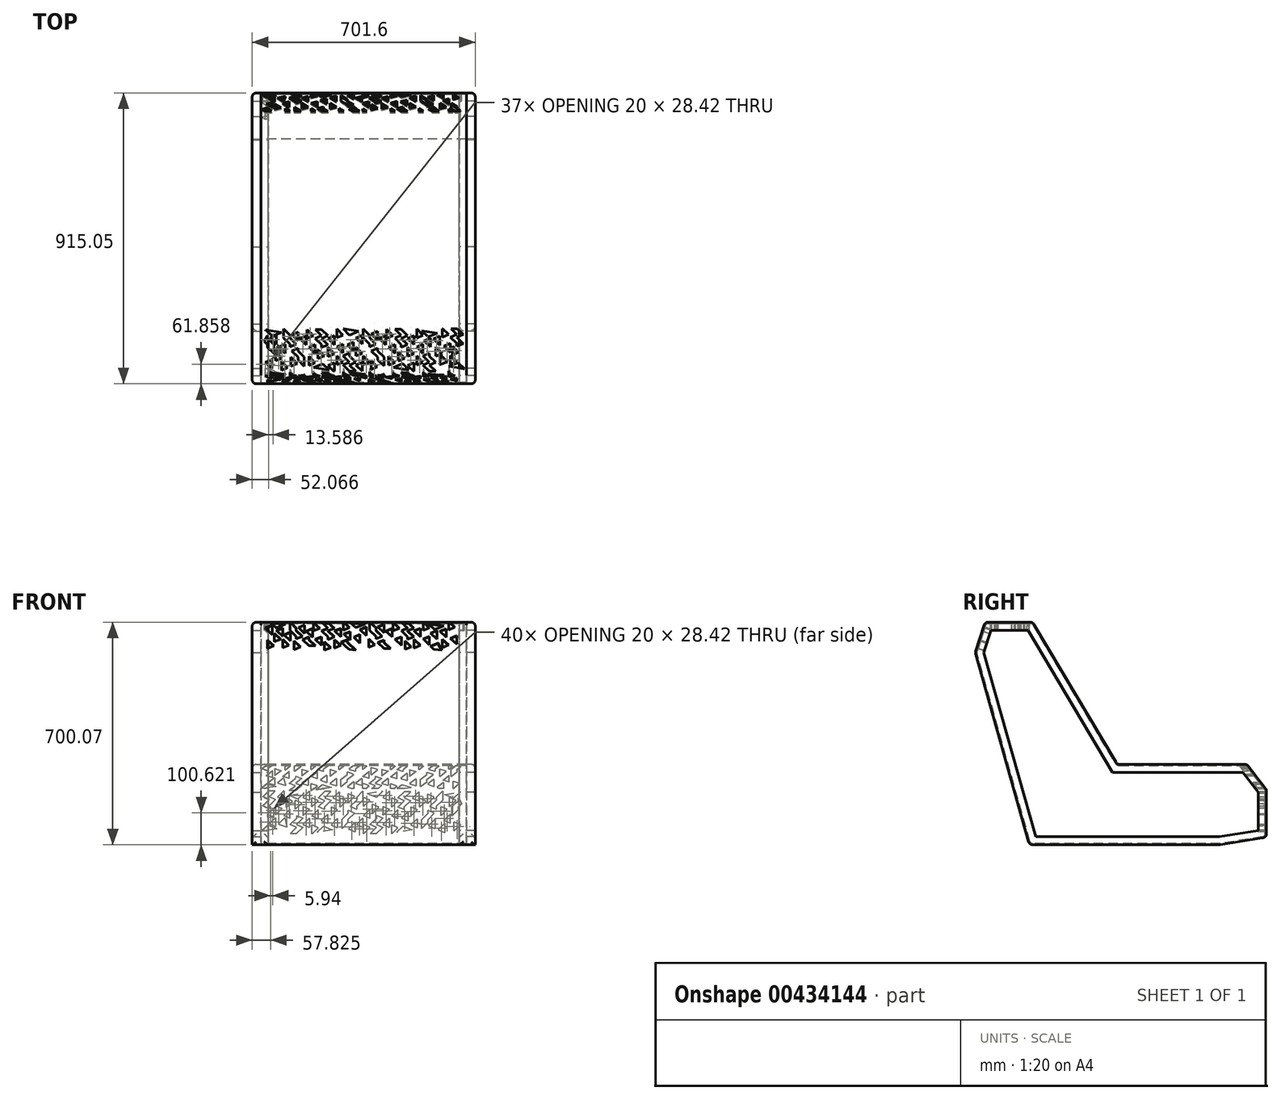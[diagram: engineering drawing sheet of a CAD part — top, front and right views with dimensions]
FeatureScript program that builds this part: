
annotation { "Feature Type Name" : "Feature", "Feature Type Description" : "" }
export const myFeature = defineFeature(function(context is Context, id is Id, definition is map)
    precondition{}
    {
        {
            var Q0;
            Q0=qCreatedBy(makeId("Right.planeOp"),FACE);
            var sketch = newSketch(context, id + "F0", { "sketchPlane" : qUnion([Q0])});
            skLineSegment(sketch, "E0", {"start": v(0, 0) * mm, "end": v(408.05, 0) * mm});
            skLineSegment(sketch, "E1", {"start": v(408.05, 0) * mm, "end": v(469.31, -79.04) * mm});
            skLineSegment(sketch, "E2", {"start": v(469.31, -79.04) * mm, "end": v(469.31, -229.04) * mm});
            skLineSegment(sketch, "E3", {"start": v(469.31, -229.04) * mm, "end": v(324.12, -252.64) * mm});
            skLineSegment(sketch, "E4", {"start": v(324.12, -252.64) * mm, "end": v(-275.88, -252.64) * mm});
            skLineSegment(sketch, "E5", {"start": v(-275.88, -252.64) * mm, "end": v(-446.19, 352.12) * mm});
            skLineSegment(sketch, "E6", {"start": v(-446.19, 352.12) * mm, "end": v(-415.7, 447.36) * mm});
            skLineSegment(sketch, "E7", {"start": v(-415.7, 447.36) * mm, "end": v(-265.7, 447.36) * mm});
            skLineSegment(sketch, "E8", {"start": v(-265.7, 447.36) * mm, "end": v(0, 0) * mm});
            skLineSegment(sketch, "E9.0", {"start": v(-419.67, 351.65) * mm, "end": v(-397.17, 421.96) * mm});
            skLineSegment(sketch, "E9.1", {"start": v(-256.64, -227.24) * mm, "end": v(-419.67, 351.65) * mm});
            skLineSegment(sketch, "E9.2", {"start": v(-397.17, 421.96) * mm, "end": v(-280.17, 421.96) * mm});
            skLineSegment(sketch, "E9.3", {"start": v(322.07, -227.24) * mm, "end": v(-256.64, -227.24) * mm});
            skLineSegment(sketch, "E9.4", {"start": v(443.91, -207.43) * mm, "end": v(322.07, -227.24) * mm});
            skLineSegment(sketch, "E9.5", {"start": v(-280.17, 421.96) * mm, "end": v(-14.46, -25.4) * mm});
            skLineSegment(sketch, "E9.6", {"start": v(-14.46, -25.4) * mm, "end": v(395.6, -25.4) * mm});
            skLineSegment(sketch, "E9.7", {"start": v(395.6, -25.4) * mm, "end": v(443.91, -87.73) * mm});
            skLineSegment(sketch, "E9.8", {"start": v(443.91, -87.73) * mm, "end": v(443.91, -207.43) * mm});
            skSolve(sketch);
        }
        {
            var Q0;
            Q0=makeQuery(id+"F0.imprint","IMPRINT",FACE,{"disambiguationData":[TD([[makeQuery(id+"F0.imprint","IMPRINT",EDGE,{"derivedFrom":sQuery(id+"F0.wireOp",EDGE,"E0")}),-1.0]])]});
            extrude(context, id + "F1", {"entities" : qUnion([Q0]), "depth" : 50.8 * mm});
        }
        {
            var Q0;
            Q0=makeQuery(id+"F1.opExtrude","SWEPT_FACE",FACE,{"disambiguationData":[OSD([sQuery(id+"F0.wireOp",EDGE,"E7")])]});
            var Q1;
            Q1=makeQuery(id+"F1.opExtrude","SWEPT_FACE",FACE,{"disambiguationData":[OSD([sQuery(id+"F0.wireOp",EDGE,"E8")])]});
            var Q2;
            Q2=makeQuery(id+"F1.opExtrude","SWEPT_FACE",FACE,{"disambiguationData":[OSD([sQuery(id+"F0.wireOp",EDGE,"E0")])]});
            var Q3;
            Q3=makeQuery(id+"F1.opExtrude","SWEPT_FACE",FACE,{"disambiguationData":[OSD([sQuery(id+"F0.wireOp",EDGE,"E1")])]});
            var Q4;
            Q4=makeQuery(id+"F1.opExtrude","SWEPT_FACE",FACE,{"disambiguationData":[OSD([sQuery(id+"F0.wireOp",EDGE,"E2")])]});
            var Q5;
            Q5=makeQuery(id+"F1.opExtrude","SWEPT_FACE",FACE,{"disambiguationData":[OSD([sQuery(id+"F0.wireOp",EDGE,"E5")])]});
            var Q6;
            Q6=makeQuery(id+"F1.opExtrude","SWEPT_FACE",FACE,{"disambiguationData":[OSD([sQuery(id+"F0.wireOp",EDGE,"E6")])]});
            fillet(context, id + "F2", {"entities" : qUnion([Q0, Q1, Q2, Q3, Q4, Q5, Q6]), "radius" : 12.7 * mm, "tangentPropagation" : true, "allowEdgeOverflow" : false});
        }
        {
            var Q0;
            Q0=qCreatedBy(makeId("Right.planeOp"),FACE);
            cPlane(context, id + "F3", {"entities" : qUnion([Q0]), "cplaneType" : CPlaneType.OFFSET, "offset" : 300 * mm, "oppositeDirection" : true, "width" : 152.4 * mm, "height" : 152.4 * mm});
        }
        {
            var Q0;
            Q0=makeQuery(id+"F1.opExtrude","SWEPT_BODY",BODY,{"disambiguationData":[OSD([sQuery(id+"F0.wireOp",EDGE,"E0"),sQuery(id+"F0.wireOp",EDGE,"E1"),sQuery(id+"F0.wireOp",EDGE,"E2"),sQuery(id+"F0.wireOp",EDGE,"E3"),sQuery(id+"F0.wireOp",EDGE,"E4"),sQuery(id+"F0.wireOp",EDGE,"E5"),sQuery(id+"F0.wireOp",EDGE,"E6"),sQuery(id+"F0.wireOp",EDGE,"E7"),sQuery(id+"F0.wireOp",EDGE,"E8"),sQuery(id+"F0.wireOp",EDGE,"E9.0"),sQuery(id+"F0.wireOp",EDGE,"E9.1"),sQuery(id+"F0.wireOp",EDGE,"E9.2"),sQuery(id+"F0.wireOp",EDGE,"E9.3"),sQuery(id+"F0.wireOp",EDGE,"E9.4"),sQuery(id+"F0.wireOp",EDGE,"E9.5"),sQuery(id+"F0.wireOp",EDGE,"E9.6"),sQuery(id+"F0.wireOp",EDGE,"E9.7"),sQuery(id+"F0.wireOp",EDGE,"E9.8")])]});
            var Q1;
            Q1=qCreatedBy(id+"F3.planeOp",FACE);
            mirror(context, id + "F4", {"entities" : qUnion([Q0]), "mirrorPlane" : qUnion([Q1])});
        }
        {
            var Q0;
            Q0=qCreatedBy(id+"F3.planeOp",FACE);
            var sketch = newSketch(context, id + "F5", { "sketchPlane" : qUnion([Q0])});
            skLineSegment(sketch, "E10.0", {"start": v(-406.34, 447.43) * mm, "end": v(-272.84, 447.43) * mm});
            skArc(sketch, "E11.0", {"start": v(-272.84, 447.43) * mm, "mid": v(-266.55, 445.77) * mm, "end": v(-261.92, 441.22) * mm});
            skLineSegment(sketch, "E12.0", {"start": v(-261.92, 441.22) * mm, "end": v(-3.59, 6.29) * mm});
            skArc(sketch, "E13.0", {"start": v(7.33, 0.07) * mm, "mid": v(1.05, 1.73) * mm, "end": v(-3.59, 6.29) * mm});
            skLineSegment(sketch, "E14.0", {"start": v(7.33, 0.07) * mm, "end": v(401.93, 0.07) * mm});
            skArc(sketch, "E15.0", {"start": v(411.97, -4.85) * mm, "mid": v(407.52, -1.23) * mm, "end": v(401.93, 0.07) * mm});
            skLineSegment(sketch, "E16.0", {"start": v(411.97, -4.85) * mm, "end": v(466.75, -75.53) * mm});
            skArc(sketch, "E17.0", {"start": v(469.42, -83.31) * mm, "mid": v(468.73, -79.2) * mm, "end": v(466.75, -75.53) * mm});
            skLineSegment(sketch, "E18.0", {"start": v(469.42, -83.31) * mm, "end": v(469.42, -218.16) * mm});
            skArc(sketch, "E19.0", {"start": v(458.75, -230.7) * mm, "mid": v(466.39, -226.4) * mm, "end": v(469.42, -218.16) * mm});
            skLineSegment(sketch, "E20.0", {"start": v(458.75, -230.7) * mm, "end": v(456.72, -231.03) * mm});
            skLineSegment(sketch, "E21.0", {"start": v(456.72, -231.03) * mm, "end": v(324.22, -252.57) * mm});
            skLineSegment(sketch, "E22.0", {"start": v(324.22, -252.57) * mm, "end": v(-262.58, -252.57) * mm});
            skLineSegment(sketch, "E23.0", {"start": v(-262.58, -252.57) * mm, "end": v(-266.16, -252.57) * mm});
            skArc(sketch, "E24.0", {"start": v(-278.38, -243.31) * mm, "mid": v(-273.83, -250) * mm, "end": v(-266.16, -252.57) * mm});
            skLineSegment(sketch, "E25.0", {"start": v(-278.38, -243.31) * mm, "end": v(-445.05, 348.51) * mm});
            skArc(sketch, "E26.0", {"start": v(-444.92, 355.83) * mm, "mid": v(-445.52, 352.18) * mm, "end": v(-445.05, 348.51) * mm});
            skLineSegment(sketch, "E27.0", {"start": v(-444.92, 355.83) * mm, "end": v(-418.43, 438.6) * mm});
            skArc(sketch, "E28.0", {"start": v(-406.34, 447.43) * mm, "mid": v(-413.82, 444.99) * mm, "end": v(-418.43, 438.6) * mm});
            skArc(sketch, "E29.0", {"start": v(-406.34, 443.62) * mm, "mid": v(-411.58, 441.91) * mm, "end": v(-414.8, 437.44) * mm});
            skLineSegment(sketch, "E29.1", {"start": v(-441.3, 354.67) * mm, "end": v(-414.8, 437.44) * mm});
            skArc(sketch, "E29.2", {"start": v(-441.3, 354.67) * mm, "mid": v(-441.71, 352.11) * mm, "end": v(-441.38, 349.55) * mm});
            skLineSegment(sketch, "E29.3", {"start": v(-274.72, -242.28) * mm, "end": v(-441.38, 349.55) * mm});
            skArc(sketch, "E29.4", {"start": v(-274.72, -242.28) * mm, "mid": v(-271.53, -246.96) * mm, "end": v(-266.16, -248.76) * mm});
            skLineSegment(sketch, "E29.5", {"start": v(-406.34, 443.62) * mm, "end": v(-272.84, 443.62) * mm});
            skLineSegment(sketch, "E29.6", {"start": v(-262.58, -248.76) * mm, "end": v(-266.16, -248.76) * mm});
            skLineSegment(sketch, "E29.7", {"start": v(323.92, -248.76) * mm, "end": v(-262.58, -248.76) * mm});
            skLineSegment(sketch, "E29.8", {"start": v(456.1, -227.27) * mm, "end": v(323.92, -248.76) * mm});
            skLineSegment(sketch, "E29.9", {"start": v(7.33, -3.74) * mm, "end": v(401.93, -3.74) * mm});
            skArc(sketch, "E29.10", {"start": v(7.33, -3.74) * mm, "mid": v(-0.84, -1.58) * mm, "end": v(-6.87, 4.34) * mm});
            skLineSegment(sketch, "E29.11", {"start": v(-265.2, 439.27) * mm, "end": v(-6.87, 4.34) * mm});
            skArc(sketch, "E29.12", {"start": v(-272.84, 443.62) * mm, "mid": v(-268.44, 442.46) * mm, "end": v(-265.2, 439.27) * mm});
            skArc(sketch, "E29.13", {"start": v(408.95, -7.18) * mm, "mid": v(405.84, -4.65) * mm, "end": v(401.93, -3.74) * mm});
            skLineSegment(sketch, "E29.14", {"start": v(408.95, -7.18) * mm, "end": v(463.74, -77.87) * mm});
            skArc(sketch, "E29.15", {"start": v(465.6, -83.31) * mm, "mid": v(465.13, -80.43) * mm, "end": v(463.74, -77.87) * mm});
            skLineSegment(sketch, "E29.16", {"start": v(465.6, -83.31) * mm, "end": v(465.6, -218.16) * mm});
            skArc(sketch, "E29.17", {"start": v(458.14, -226.94) * mm, "mid": v(463.49, -223.92) * mm, "end": v(465.6, -218.16) * mm});
            skLineSegment(sketch, "E29.18", {"start": v(458.14, -226.94) * mm, "end": v(456.1, -227.27) * mm});
            skSolve(sketch);
        }
        {
            var Q0;
            Q0 = qSketchRegion(id + "F5", true);
            extrude(context, id + "F6", {"entities" : qUnion([Q0]), "endBound" : BoundingType.SYMMETRIC, "depth" : 645.67 * mm});
        }
        {
            var Q0;
            Q0=makeQuery(id+"F6.opExtrude","SWEPT_FACE",FACE,{"disambiguationData":[OSD([sQuery(id+"F5.wireOp",EDGE,"E10.0")])]});
            var sketch = newSketch(context, id + "F7", { "sketchPlane" : qUnion([Q0])});
            skLineSegment(sketch, "E30", {"start": v(-607.6, -275.94) * mm, "end": v(-587.6, -295.74) * mm});
            skLineSegment(sketch, "E31", {"start": v(-588.73, -397.98) * mm, "end": v(-608.73, -378.18) * mm});
            skLineSegment(sketch, "E32", {"start": v(-608.73, -378.18) * mm, "end": v(-588.73, -369.56) * mm});
            skLineSegment(sketch, "E33", {"start": v(-576.96, -373.41) * mm, "end": v(-556.96, -364.79) * mm});
            skLineSegment(sketch, "E34", {"start": v(-556.96, -364.79) * mm, "end": v(-576.96, -344.99) * mm});
            skLineSegment(sketch, "E35", {"start": v(-547.5, -349.65) * mm, "end": v(-567.5, -329.84) * mm});
            skLineSegment(sketch, "E36", {"start": v(-567.5, -329.84) * mm, "end": v(-547.5, -321.22) * mm});
            skLineSegment(sketch, "E37", {"start": v(-588.73, -397.98) * mm, "end": v(-588.73, -369.56) * mm});
            skLineSegment(sketch, "E38", {"start": v(-576.96, -373.41) * mm, "end": v(-576.96, -344.99) * mm});
            skLineSegment(sketch, "E39", {"start": v(-547.5, -349.65) * mm, "end": v(-547.5, -321.22) * mm});
            skLineSegment(sketch, "E40", {"start": v(-575.15, -321.5) * mm, "end": v(-595.15, -301.7) * mm});
            skLineSegment(sketch, "E41", {"start": v(-595.15, -301.7) * mm, "end": v(-575.15, -293.08) * mm});
            skLineSegment(sketch, "E42", {"start": v(-575.15, -321.5) * mm, "end": v(-575.15, -293.08) * mm});
            skLineSegment(sketch, "E43", {"start": v(-552.39, -272.84) * mm, "end": v(-532.39, -292.64) * mm});
            skLineSegment(sketch, "E44", {"start": v(-552.39, -301.26) * mm, "end": v(-532.39, -321.06) * mm});
            skLineSegment(sketch, "E45", {"start": v(-558.92, -374.38) * mm, "end": v(-538.92, -394.19) * mm});
            skLineSegment(sketch, "E46", {"start": v(-538.92, -394.19) * mm, "end": v(-558.92, -402.8) * mm});
            skLineSegment(sketch, "E47", {"start": v(-552.39, -272.84) * mm, "end": v(-552.39, -301.26) * mm});
            skLineSegment(sketch, "E48", {"start": v(-532.39, -321.06) * mm, "end": v(-532.39, -329.68) * mm});
            skLineSegment(sketch, "E49", {"start": v(-558.92, -374.38) * mm, "end": v(-558.92, -402.8) * mm});
            skLineSegment(sketch, "E50", {"start": v(-532.39, -301.26) * mm, "end": v(-512.39, -321.06) * mm});
            skLineSegment(sketch, "E51", {"start": v(-512.39, -321.06) * mm, "end": v(-532.39, -329.68) * mm});
            skLineSegment(sketch, "E52", {"start": v(-528.78, -361.72) * mm, "end": v(-508.78, -381.52) * mm});
            skLineSegment(sketch, "E53", {"start": v(-508.78, -381.52) * mm, "end": v(-528.78, -390.14) * mm});
            skLineSegment(sketch, "E54", {"start": v(-532.39, -292.64) * mm, "end": v(-532.39, -301.26) * mm});
            skLineSegment(sketch, "E55", {"start": v(-528.78, -361.72) * mm, "end": v(-528.78, -390.14) * mm});
            skLineSegment(sketch, "E56", {"start": v(-587.6, -295.74) * mm, "end": v(-558.27, -283.53) * mm});
            skLineSegment(sketch, "E57", {"start": v(-558.27, -283.53) * mm, "end": v(-607.6, -275.94) * mm});
            skLineSegment(sketch, "E58", {"start": v(-392.44, -407.94) * mm, "end": v(-412.44, -388.14) * mm});
            skLineSegment(sketch, "E59", {"start": v(-412.44, -388.14) * mm, "end": v(-392.44, -379.52) * mm});
            skLineSegment(sketch, "E60", {"start": v(-412.44, -359.71) * mm, "end": v(-392.44, -351.1) * mm});
            skLineSegment(sketch, "E61", {"start": v(-392.44, -351.1) * mm, "end": v(-412.44, -331.29) * mm});
            skLineSegment(sketch, "E62", {"start": v(-392.44, -322.67) * mm, "end": v(-412.44, -302.86) * mm});
            skLineSegment(sketch, "E63", {"start": v(-412.44, -302.86) * mm, "end": v(-392.44, -294.24) * mm});
            skLineSegment(sketch, "E64", {"start": v(-392.44, -407.94) * mm, "end": v(-392.44, -379.52) * mm});
            skLineSegment(sketch, "E65", {"start": v(-412.44, -359.71) * mm, "end": v(-412.44, -331.29) * mm});
            skLineSegment(sketch, "E66", {"start": v(-392.44, -322.67) * mm, "end": v(-392.44, -294.24) * mm});
            skLineSegment(sketch, "E67", {"start": v(-408.39, -402.37) * mm, "end": v(-428.39, -382.57) * mm});
            skLineSegment(sketch, "E68", {"start": v(-432.44, -331.29) * mm, "end": v(-412.44, -322.67) * mm});
            skLineSegment(sketch, "E69", {"start": v(-412.44, -322.67) * mm, "end": v(-432.44, -302.86) * mm});
            skLineSegment(sketch, "E70", {"start": v(-432.44, -302.86) * mm, "end": v(-412.44, -294.24) * mm});
            skLineSegment(sketch, "E71", {"start": v(-412.44, -294.24) * mm, "end": v(-432.44, -274.44) * mm});
            skLineSegment(sketch, "E72", {"start": v(-478.2, -274.68) * mm, "end": v(-458.2, -294.48) * mm});
            skLineSegment(sketch, "E73", {"start": v(-458.2, -294.48) * mm, "end": v(-478.2, -303.1) * mm});
            skLineSegment(sketch, "E74", {"start": v(-452.57, -322.23) * mm, "end": v(-472.57, -330.85) * mm});
            skLineSegment(sketch, "E75", {"start": v(-472.57, -330.85) * mm, "end": v(-452.57, -350.65) * mm});
            skLineSegment(sketch, "E76", {"start": v(-472.57, -359.27) * mm, "end": v(-452.57, -379.08) * mm});
            skLineSegment(sketch, "E77", {"start": v(-452.57, -379.08) * mm, "end": v(-472.57, -387.7) * mm});
            skLineSegment(sketch, "E78", {"start": v(-478.2, -274.68) * mm, "end": v(-478.2, -303.1) * mm});
            skLineSegment(sketch, "E79", {"start": v(-452.57, -322.23) * mm, "end": v(-452.57, -350.65) * mm});
            skLineSegment(sketch, "E80", {"start": v(-472.57, -359.27) * mm, "end": v(-472.57, -387.7) * mm});
            skLineSegment(sketch, "E81", {"start": v(-452.16, -274.4) * mm, "end": v(-432.57, -293.8) * mm});
            skLineSegment(sketch, "E82", {"start": v(-432.57, -293.8) * mm, "end": v(-452.57, -302.43) * mm});
            skLineSegment(sketch, "E83", {"start": v(-452.57, -302.43) * mm, "end": v(-432.57, -322.23) * mm});
            skLineSegment(sketch, "E84", {"start": v(-444, -338.07) * mm, "end": v(-424, -357.88) * mm});
            skLineSegment(sketch, "E85", {"start": v(-424, -357.88) * mm, "end": v(-444, -366.5) * mm});
            skLineSegment(sketch, "E86", {"start": v(-444, -338.07) * mm, "end": v(-444, -366.5) * mm});
            skLineSegment(sketch, "E87", {"start": v(-486.83, -390.35) * mm, "end": v(-506.83, -370.54) * mm});
            skLineSegment(sketch, "E88", {"start": v(-486.83, -361.92) * mm, "end": v(-506.83, -342.12) * mm});
            skLineSegment(sketch, "E89", {"start": v(-480.97, -323.34) * mm, "end": v(-500.97, -303.54) * mm});
            skLineSegment(sketch, "E90", {"start": v(-500.97, -303.54) * mm, "end": v(-480.97, -294.92) * mm});
            skLineSegment(sketch, "E91", {"start": v(-486.83, -390.35) * mm, "end": v(-486.83, -361.92) * mm});
            skLineSegment(sketch, "E92", {"start": v(-506.83, -342.12) * mm, "end": v(-506.83, -333.5) * mm});
            skLineSegment(sketch, "E93", {"start": v(-480.97, -323.34) * mm, "end": v(-480.97, -294.92) * mm});
            skLineSegment(sketch, "E94", {"start": v(-506.83, -361.92) * mm, "end": v(-526.83, -342.12) * mm});
            skLineSegment(sketch, "E95", {"start": v(-526.83, -342.12) * mm, "end": v(-506.83, -333.5) * mm});
            skLineSegment(sketch, "E96", {"start": v(-505.93, -311.16) * mm, "end": v(-525.93, -291.36) * mm});
            skLineSegment(sketch, "E97", {"start": v(-525.93, -291.36) * mm, "end": v(-505.93, -282.74) * mm});
            skLineSegment(sketch, "E98", {"start": v(-506.83, -370.54) * mm, "end": v(-506.83, -361.92) * mm});
            skLineSegment(sketch, "E99", {"start": v(-505.93, -311.16) * mm, "end": v(-505.93, -282.74) * mm});
            skLineSegment(sketch, "E100", {"start": v(-452.16, -274.4) * mm, "end": v(-432.44, -274.44) * mm});
            skLineSegment(sketch, "E101", {"start": v(-432.44, -331.29) * mm, "end": v(-432.57, -322.23) * mm});
            skLineSegment(sketch, "E102", {"start": v(-428.39, -382.57) * mm, "end": v(-457.7, -394.78) * mm});
            skLineSegment(sketch, "E103", {"start": v(-457.7, -394.78) * mm, "end": v(-408.39, -402.37) * mm});
            skLineSegment(sketch, "E104", {"start": v(-384.82, -272.4) * mm, "end": v(-364.82, -292.21) * mm});
            skLineSegment(sketch, "E105", {"start": v(-364.82, -292.21) * mm, "end": v(-384.82, -300.83) * mm});
            skLineSegment(sketch, "E106", {"start": v(-364.82, -320.64) * mm, "end": v(-384.82, -329.26) * mm});
            skLineSegment(sketch, "E107", {"start": v(-384.82, -329.26) * mm, "end": v(-364.82, -349.06) * mm});
            skLineSegment(sketch, "E108", {"start": v(-384.82, -357.68) * mm, "end": v(-364.82, -377.49) * mm});
            skLineSegment(sketch, "E109", {"start": v(-364.82, -377.49) * mm, "end": v(-384.82, -386.1) * mm});
            skLineSegment(sketch, "E110", {"start": v(-384.82, -272.4) * mm, "end": v(-384.82, -300.83) * mm});
            skLineSegment(sketch, "E111", {"start": v(-364.82, -320.64) * mm, "end": v(-364.82, -349.06) * mm});
            skLineSegment(sketch, "E112", {"start": v(-384.82, -357.68) * mm, "end": v(-384.82, -386.1) * mm});
            skLineSegment(sketch, "E113", {"start": v(-364.82, -272.4) * mm, "end": v(-344.82, -292.21) * mm});
            skLineSegment(sketch, "E114", {"start": v(-344.82, -349.06) * mm, "end": v(-364.82, -357.68) * mm});
            skLineSegment(sketch, "E115", {"start": v(-364.82, -357.68) * mm, "end": v(-344.82, -377.49) * mm});
            skLineSegment(sketch, "E116", {"start": v(-344.82, -377.49) * mm, "end": v(-364.82, -386.1) * mm});
            skLineSegment(sketch, "E117", {"start": v(-364.82, -386.1) * mm, "end": v(-344.82, -405.91) * mm});
            skLineSegment(sketch, "E118", {"start": v(-364.82, -272.4) * mm, "end": v(-364.82, -272.42) * mm});
            skLineSegment(sketch, "E119", {"start": v(-304.68, -406.35) * mm, "end": v(-324.68, -386.55) * mm});
            skLineSegment(sketch, "E120", {"start": v(-324.68, -386.55) * mm, "end": v(-304.68, -377.92) * mm});
            skLineSegment(sketch, "E121", {"start": v(-324.68, -358.12) * mm, "end": v(-304.68, -349.5) * mm});
            skLineSegment(sketch, "E122", {"start": v(-304.68, -349.5) * mm, "end": v(-324.68, -329.7) * mm});
            skLineSegment(sketch, "E123", {"start": v(-304.68, -321.07) * mm, "end": v(-324.68, -301.27) * mm});
            skLineSegment(sketch, "E124", {"start": v(-324.68, -301.27) * mm, "end": v(-304.68, -292.65) * mm});
            skLineSegment(sketch, "E125", {"start": v(-304.68, -406.35) * mm, "end": v(-304.68, -377.92) * mm});
            skLineSegment(sketch, "E126", {"start": v(-324.68, -358.12) * mm, "end": v(-324.68, -329.7) * mm});
            skLineSegment(sketch, "E127", {"start": v(-304.68, -321.07) * mm, "end": v(-304.68, -292.65) * mm});
            skLineSegment(sketch, "E128", {"start": v(-325.1, -405.94) * mm, "end": v(-344.68, -386.55) * mm});
            skLineSegment(sketch, "E129", {"start": v(-344.68, -386.55) * mm, "end": v(-324.68, -377.92) * mm});
            skLineSegment(sketch, "E130", {"start": v(-324.68, -377.92) * mm, "end": v(-344.68, -358.12) * mm});
            skLineSegment(sketch, "E131", {"start": v(-331.9, -343.18) * mm, "end": v(-351.9, -323.37) * mm});
            skLineSegment(sketch, "E132", {"start": v(-351.9, -323.37) * mm, "end": v(-331.9, -314.75) * mm});
            skLineSegment(sketch, "E133", {"start": v(-331.9, -343.18) * mm, "end": v(-331.9, -314.75) * mm});
            skLineSegment(sketch, "E134", {"start": v(-301.93, -272.4) * mm, "end": v(-281.93, -292.21) * mm});
            skLineSegment(sketch, "E135", {"start": v(-301.93, -300.83) * mm, "end": v(-281.93, -320.64) * mm});
            skLineSegment(sketch, "E136", {"start": v(-301.93, -357.68) * mm, "end": v(-281.93, -377.49) * mm});
            skLineSegment(sketch, "E137", {"start": v(-281.93, -377.49) * mm, "end": v(-301.93, -386.1) * mm});
            skLineSegment(sketch, "E138", {"start": v(-301.93, -272.4) * mm, "end": v(-301.93, -300.83) * mm});
            skLineSegment(sketch, "E139", {"start": v(-281.93, -320.64) * mm, "end": v(-281.93, -329.26) * mm});
            skLineSegment(sketch, "E140", {"start": v(-301.93, -357.68) * mm, "end": v(-301.93, -386.1) * mm});
            skLineSegment(sketch, "E141", {"start": v(-281.93, -300.83) * mm, "end": v(-261.93, -320.64) * mm});
            skLineSegment(sketch, "E142", {"start": v(-261.93, -320.64) * mm, "end": v(-281.93, -329.26) * mm});
            skLineSegment(sketch, "E143", {"start": v(-276.96, -371.67) * mm, "end": v(-256.96, -391.47) * mm});
            skLineSegment(sketch, "E144", {"start": v(-256.96, -391.47) * mm, "end": v(-276.96, -400.1) * mm});
            skLineSegment(sketch, "E145", {"start": v(-281.93, -292.21) * mm, "end": v(-281.93, -300.83) * mm});
            skLineSegment(sketch, "E146", {"start": v(-276.96, -371.67) * mm, "end": v(-276.96, -400.1) * mm});
            skLineSegment(sketch, "E147", {"start": v(-325.1, -405.94) * mm, "end": v(-344.82, -405.91) * mm});
            skLineSegment(sketch, "E148", {"start": v(-344.82, -349.06) * mm, "end": v(-344.68, -358.12) * mm});
            skLineSegment(sketch, "E149", {"start": v(-344.82, -292.21) * mm, "end": v(-315.5, -280) * mm});
            skLineSegment(sketch, "E150", {"start": v(-315.5, -280) * mm, "end": v(-364.82, -272.4) * mm});
            skLineSegment(sketch, "E151", {"start": v(-141.97, -407.51) * mm, "end": v(-161.97, -387.71) * mm});
            skLineSegment(sketch, "E152", {"start": v(-161.97, -387.71) * mm, "end": v(-141.97, -379.09) * mm});
            skLineSegment(sketch, "E153", {"start": v(-161.97, -359.29) * mm, "end": v(-141.97, -350.66) * mm});
            skLineSegment(sketch, "E154", {"start": v(-141.97, -350.66) * mm, "end": v(-161.97, -330.86) * mm});
            skLineSegment(sketch, "E155", {"start": v(-141.97, -322.24) * mm, "end": v(-161.97, -302.44) * mm});
            skLineSegment(sketch, "E156", {"start": v(-161.97, -302.44) * mm, "end": v(-141.97, -293.82) * mm});
            skLineSegment(sketch, "E157", {"start": v(-141.97, -407.51) * mm, "end": v(-141.97, -379.09) * mm});
            skLineSegment(sketch, "E158", {"start": v(-161.97, -359.29) * mm, "end": v(-161.97, -330.86) * mm});
            skLineSegment(sketch, "E159", {"start": v(-141.97, -322.24) * mm, "end": v(-141.97, -293.82) * mm});
            skLineSegment(sketch, "E160", {"start": v(-157.92, -401.94) * mm, "end": v(-177.92, -382.14) * mm});
            skLineSegment(sketch, "E161", {"start": v(-181.97, -330.86) * mm, "end": v(-161.97, -322.24) * mm});
            skLineSegment(sketch, "E162", {"start": v(-161.97, -322.24) * mm, "end": v(-181.97, -302.44) * mm});
            skLineSegment(sketch, "E163", {"start": v(-181.97, -302.44) * mm, "end": v(-161.97, -293.82) * mm});
            skLineSegment(sketch, "E164", {"start": v(-161.97, -293.82) * mm, "end": v(-181.97, -274.01) * mm});
            skLineSegment(sketch, "E165", {"start": v(-227.74, -274.25) * mm, "end": v(-207.74, -294.05) * mm});
            skLineSegment(sketch, "E166", {"start": v(-207.74, -294.05) * mm, "end": v(-227.74, -302.68) * mm});
            skLineSegment(sketch, "E167", {"start": v(-202.1, -321.8) * mm, "end": v(-222.1, -330.42) * mm});
            skLineSegment(sketch, "E168", {"start": v(-222.1, -330.42) * mm, "end": v(-202.1, -350.23) * mm});
            skLineSegment(sketch, "E169", {"start": v(-222.1, -358.85) * mm, "end": v(-202.1, -378.65) * mm});
            skLineSegment(sketch, "E170", {"start": v(-202.1, -378.65) * mm, "end": v(-222.1, -387.27) * mm});
            skLineSegment(sketch, "E171", {"start": v(-227.74, -274.25) * mm, "end": v(-227.74, -302.68) * mm});
            skLineSegment(sketch, "E172", {"start": v(-202.1, -321.8) * mm, "end": v(-202.1, -350.23) * mm});
            skLineSegment(sketch, "E173", {"start": v(-222.1, -358.85) * mm, "end": v(-222.1, -387.27) * mm});
            skLineSegment(sketch, "E174", {"start": v(-201.7, -273.98) * mm, "end": v(-182.1, -293.38) * mm});
            skLineSegment(sketch, "E175", {"start": v(-182.1, -293.38) * mm, "end": v(-202.1, -302) * mm});
            skLineSegment(sketch, "E176", {"start": v(-202.1, -302) * mm, "end": v(-182.1, -321.8) * mm});
            skLineSegment(sketch, "E177", {"start": v(-191.28, -345.32) * mm, "end": v(-171.28, -365.12) * mm});
            skLineSegment(sketch, "E178", {"start": v(-171.28, -365.12) * mm, "end": v(-191.28, -373.74) * mm});
            skLineSegment(sketch, "E179", {"start": v(-191.28, -345.32) * mm, "end": v(-191.28, -373.74) * mm});
            skLineSegment(sketch, "E180", {"start": v(-236.37, -389.92) * mm, "end": v(-256.37, -370.12) * mm});
            skLineSegment(sketch, "E181", {"start": v(-236.37, -361.5) * mm, "end": v(-256.37, -341.7) * mm});
            skLineSegment(sketch, "E182", {"start": v(-230.5, -322.92) * mm, "end": v(-250.5, -303.11) * mm});
            skLineSegment(sketch, "E183", {"start": v(-250.5, -303.11) * mm, "end": v(-230.5, -294.5) * mm});
            skLineSegment(sketch, "E184", {"start": v(-236.37, -389.92) * mm, "end": v(-236.37, -361.5) * mm});
            skLineSegment(sketch, "E185", {"start": v(-256.37, -341.7) * mm, "end": v(-256.37, -333.07) * mm});
            skLineSegment(sketch, "E186", {"start": v(-230.5, -322.92) * mm, "end": v(-230.5, -294.5) * mm});
            skLineSegment(sketch, "E187", {"start": v(-256.37, -361.5) * mm, "end": v(-276.37, -341.7) * mm});
            skLineSegment(sketch, "E188", {"start": v(-276.37, -341.7) * mm, "end": v(-256.37, -333.07) * mm});
            skLineSegment(sketch, "E189", {"start": v(-256.37, -308.93) * mm, "end": v(-276.37, -289.13) * mm});
            skLineSegment(sketch, "E190", {"start": v(-276.37, -289.13) * mm, "end": v(-256.37, -280.5) * mm});
            skLineSegment(sketch, "E191", {"start": v(-256.37, -370.12) * mm, "end": v(-256.37, -361.5) * mm});
            skLineSegment(sketch, "E192", {"start": v(-256.37, -308.93) * mm, "end": v(-256.37, -280.5) * mm});
            skLineSegment(sketch, "E193", {"start": v(-201.7, -273.98) * mm, "end": v(-181.97, -274.01) * mm});
            skLineSegment(sketch, "E194", {"start": v(-181.97, -330.86) * mm, "end": v(-182.1, -321.8) * mm});
            skLineSegment(sketch, "E195", {"start": v(-177.92, -382.14) * mm, "end": v(-207.24, -394.35) * mm});
            skLineSegment(sketch, "E196", {"start": v(-207.24, -394.35) * mm, "end": v(-157.92, -401.94) * mm});
            skLineSegment(sketch, "E197", {"start": v(-133.47, -272.64) * mm, "end": v(-113.47, -292.45) * mm});
            skLineSegment(sketch, "E198", {"start": v(-113.47, -292.45) * mm, "end": v(-133.47, -301.07) * mm});
            skLineSegment(sketch, "E199", {"start": v(-113.47, -320.87) * mm, "end": v(-133.47, -329.5) * mm});
            skLineSegment(sketch, "E200", {"start": v(-133.47, -329.5) * mm, "end": v(-113.47, -349.3) * mm});
            skLineSegment(sketch, "E201", {"start": v(-133.47, -357.92) * mm, "end": v(-113.47, -377.72) * mm});
            skLineSegment(sketch, "E202", {"start": v(-113.47, -377.72) * mm, "end": v(-133.47, -386.34) * mm});
            skLineSegment(sketch, "E203", {"start": v(-133.47, -272.64) * mm, "end": v(-133.47, -301.07) * mm});
            skLineSegment(sketch, "E204", {"start": v(-113.47, -320.87) * mm, "end": v(-113.47, -349.3) * mm});
            skLineSegment(sketch, "E205", {"start": v(-133.47, -357.92) * mm, "end": v(-133.47, -386.34) * mm});
            skLineSegment(sketch, "E206", {"start": v(-117.52, -278.21) * mm, "end": v(-97.52, -298.01) * mm});
            skLineSegment(sketch, "E207", {"start": v(-93.47, -349.3) * mm, "end": v(-113.47, -357.92) * mm});
            skLineSegment(sketch, "E208", {"start": v(-113.47, -357.92) * mm, "end": v(-93.47, -377.72) * mm});
            skLineSegment(sketch, "E209", {"start": v(-93.47, -377.72) * mm, "end": v(-113.47, -386.34) * mm});
            skLineSegment(sketch, "E210", {"start": v(-113.47, -386.34) * mm, "end": v(-93.47, -406.14) * mm});
            skLineSegment(sketch, "E211", {"start": v(-73.34, -358.35) * mm, "end": v(-53.34, -349.73) * mm});
            skLineSegment(sketch, "E212", {"start": v(-53.34, -349.73) * mm, "end": v(-73.34, -329.93) * mm});
            skLineSegment(sketch, "E213", {"start": v(-61, -324.01) * mm, "end": v(-81, -304.21) * mm});
            skLineSegment(sketch, "E214", {"start": v(-81, -304.21) * mm, "end": v(-61, -295.59) * mm});
            skLineSegment(sketch, "E215", {"start": v(-73.34, -358.35) * mm, "end": v(-73.34, -329.93) * mm});
            skLineSegment(sketch, "E216", {"start": v(-61, -324.01) * mm, "end": v(-61, -295.59) * mm});
            skLineSegment(sketch, "E217", {"start": v(-73.75, -406.17) * mm, "end": v(-93.34, -386.78) * mm});
            skLineSegment(sketch, "E218", {"start": v(-93.34, -386.78) * mm, "end": v(-73.34, -378.16) * mm});
            skLineSegment(sketch, "E219", {"start": v(-73.34, -378.16) * mm, "end": v(-93.34, -358.35) * mm});
            skLineSegment(sketch, "E220", {"start": v(-90.03, -329.88) * mm, "end": v(-110.03, -310.08) * mm});
            skLineSegment(sketch, "E221", {"start": v(-110.03, -310.08) * mm, "end": v(-90.03, -301.45) * mm});
            skLineSegment(sketch, "E222", {"start": v(-90.03, -329.88) * mm, "end": v(-90.03, -301.45) * mm});
            skLineSegment(sketch, "E223", {"start": v(-73.75, -406.17) * mm, "end": v(-93.47, -406.14) * mm});
            skLineSegment(sketch, "E224", {"start": v(-93.47, -349.3) * mm, "end": v(-93.34, -358.35) * mm});
            skLineSegment(sketch, "E225", {"start": v(-97.52, -298.01) * mm, "end": v(-68.2, -285.8) * mm});
            skLineSegment(sketch, "E226", {"start": v(-68.2, -285.8) * mm, "end": v(-117.52, -278.21) * mm});
            skLineSegment(sketch, "E227", {"start": v(-21.76, -354.94) * mm, "end": v(-1.76, -346.32) * mm});
            skLineSegment(sketch, "E228", {"start": v(-1.76, -346.32) * mm, "end": v(-21.76, -326.52) * mm});
            skLineSegment(sketch, "E229", {"start": v(-21.76, -354.94) * mm, "end": v(-21.76, -326.52) * mm});
            skLineSegment(sketch, "E230", {"start": v(16.48, -398.74) * mm, "end": v(-3.52, -378.94) * mm});
            skLineSegment(sketch, "E231", {"start": v(-7.57, -327.66) * mm, "end": v(12.43, -319.04) * mm});
            skLineSegment(sketch, "E232", {"start": v(12.43, -319.04) * mm, "end": v(-7.57, -299.24) * mm});
            skLineSegment(sketch, "E233", {"start": v(-7.57, -299.24) * mm, "end": v(12.43, -290.62) * mm});
            skLineSegment(sketch, "E234", {"start": v(12.43, -290.62) * mm, "end": v(-7.57, -270.81) * mm});
            skLineSegment(sketch, "E235", {"start": v(-53.34, -271.05) * mm, "end": v(-33.34, -290.85) * mm});
            skLineSegment(sketch, "E236", {"start": v(-33.34, -290.85) * mm, "end": v(-53.34, -299.48) * mm});
            skLineSegment(sketch, "E237", {"start": v(-27.7, -318.6) * mm, "end": v(-47.7, -327.22) * mm});
            skLineSegment(sketch, "E238", {"start": v(-47.7, -327.22) * mm, "end": v(-27.7, -347.03) * mm});
            skLineSegment(sketch, "E239", {"start": v(-56.27, -356.55) * mm, "end": v(-36.27, -376.35) * mm});
            skLineSegment(sketch, "E240", {"start": v(-36.27, -376.35) * mm, "end": v(-62.14, -384.97) * mm});
            skLineSegment(sketch, "E241", {"start": v(-53.34, -271.05) * mm, "end": v(-53.34, -299.48) * mm});
            skLineSegment(sketch, "E242", {"start": v(-27.7, -318.6) * mm, "end": v(-27.7, -347.03) * mm});
            skLineSegment(sketch, "E243", {"start": v(-56.27, -356.55) * mm, "end": v(-62.14, -384.97) * mm});
            skLineSegment(sketch, "E244", {"start": v(-27.29, -270.78) * mm, "end": v(-7.7, -290.18) * mm});
            skLineSegment(sketch, "E245", {"start": v(-7.7, -290.18) * mm, "end": v(-27.7, -298.8) * mm});
            skLineSegment(sketch, "E246", {"start": v(-27.7, -298.8) * mm, "end": v(-7.7, -318.6) * mm});
            skLineSegment(sketch, "E247", {"start": v(-27.7, -355.65) * mm, "end": v(-7.7, -375.45) * mm});
            skLineSegment(sketch, "E248", {"start": v(-7.7, -375.45) * mm, "end": v(-27.7, -384.07) * mm});
            skLineSegment(sketch, "E249", {"start": v(-27.7, -355.65) * mm, "end": v(-27.7, -384.07) * mm});
            skLineSegment(sketch, "E250", {"start": v(-27.29, -270.78) * mm, "end": v(-7.57, -270.81) * mm});
            skLineSegment(sketch, "E251", {"start": v(-7.57, -327.66) * mm, "end": v(-7.7, -318.6) * mm});
            skLineSegment(sketch, "E252", {"start": v(-3.52, -378.94) * mm, "end": v(-32.84, -391.15) * mm});
            skLineSegment(sketch, "E253", {"start": v(-32.84, -391.15) * mm, "end": v(16.48, -398.74) * mm});
            skLineSegment(sketch, "E254", {"start": v(-582.7, -350.4) * mm, "end": v(-602.7, -330.6) * mm});
            skLineSegment(sketch, "E255", {"start": v(-582.7, -321.98) * mm, "end": v(-602.7, -302.18) * mm});
            skLineSegment(sketch, "E256", {"start": v(-582.7, -350.4) * mm, "end": v(-582.7, -321.98) * mm});
            skLineSegment(sketch, "E257", {"start": v(-602.7, -302.18) * mm, "end": v(-602.7, -293.55) * mm});
            skLineSegment(sketch, "E258", {"start": v(-602.7, -321.98) * mm, "end": v(-612.7, -312.08) * mm});
            skLineSegment(sketch, "E259", {"start": v(-602.7, -330.6) * mm, "end": v(-602.7, -321.98) * mm});
            skLineSegment(sketch, "E260", {"start": v(-602.7, -293.55) * mm, "end": v(-612.7, -312.08) * mm});
            skPoint(sketch, "E261.orphan", {"position": v(-622.7, -302.18) * mm});
            skSolve(sketch);
        }
        {
            var Q0;
            Q0=makeQuery(id+"F6.opExtrude","SWEPT_FACE",FACE,{"disambiguationData":[OSD([sQuery(id+"F5.wireOp",EDGE,"E27.0")])]});
            var sketch = newSketch(context, id + "F8", { "sketchPlane" : qUnion([Q0])});
            skLineSegment(sketch, "E262", {"start": v(-595.1, 300.96) * mm, "end": v(-575.1, 281.16) * mm});
            skLineSegment(sketch, "E263", {"start": v(-595.1, 300.96) * mm, "end": v(-595.1, 300.94) * mm});
            skLineSegment(sketch, "E264", {"start": v(-554.96, 215.25) * mm, "end": v(-534.96, 223.87) * mm});
            skLineSegment(sketch, "E265", {"start": v(-534.96, 223.87) * mm, "end": v(-554.96, 243.67) * mm});
            skLineSegment(sketch, "E266", {"start": v(-530.9, 238.3) * mm, "end": v(-550.9, 258.11) * mm});
            skLineSegment(sketch, "E267", {"start": v(-550.9, 258.11) * mm, "end": v(-530.9, 266.73) * mm});
            skLineSegment(sketch, "E268", {"start": v(-554.96, 215.25) * mm, "end": v(-554.96, 243.67) * mm});
            skLineSegment(sketch, "E269", {"start": v(-530.9, 238.3) * mm, "end": v(-530.9, 266.73) * mm});
            skLineSegment(sketch, "E270", {"start": v(-554.96, 252.3) * mm, "end": v(-574.96, 272.1) * mm});
            skLineSegment(sketch, "E271", {"start": v(-574.96, 272.1) * mm, "end": v(-554.96, 280.72) * mm});
            skLineSegment(sketch, "E272", {"start": v(-554.96, 252.3) * mm, "end": v(-554.96, 280.72) * mm});
            skLineSegment(sketch, "E273", {"start": v(-532.2, 300.96) * mm, "end": v(-512.2, 281.16) * mm});
            skLineSegment(sketch, "E274", {"start": v(-532.2, 272.53) * mm, "end": v(-512.2, 252.73) * mm});
            skLineSegment(sketch, "E275", {"start": v(-532.2, 300.96) * mm, "end": v(-532.2, 272.53) * mm});
            skLineSegment(sketch, "E276", {"start": v(-512.2, 252.73) * mm, "end": v(-512.2, 244.1) * mm});
            skLineSegment(sketch, "E277", {"start": v(-512.2, 272.53) * mm, "end": v(-492.2, 252.73) * mm});
            skLineSegment(sketch, "E278", {"start": v(-492.2, 252.73) * mm, "end": v(-512.2, 244.1) * mm});
            skLineSegment(sketch, "E279", {"start": v(-581.25, 263.28) * mm, "end": v(-561.25, 243.48) * mm});
            skLineSegment(sketch, "E280", {"start": v(-561.25, 243.48) * mm, "end": v(-581.25, 234.86) * mm});
            skLineSegment(sketch, "E281", {"start": v(-512.2, 281.16) * mm, "end": v(-512.2, 272.53) * mm});
            skLineSegment(sketch, "E282", {"start": v(-581.25, 263.28) * mm, "end": v(-581.25, 234.86) * mm});
            skLineSegment(sketch, "E283", {"start": v(-575.1, 281.16) * mm, "end": v(-545.77, 293.37) * mm});
            skLineSegment(sketch, "E284", {"start": v(-545.77, 293.37) * mm, "end": v(-595.1, 300.96) * mm});
            skLineSegment(sketch, "E285", {"start": v(-392.25, 214.08) * mm, "end": v(-372.25, 222.7) * mm});
            skLineSegment(sketch, "E286", {"start": v(-372.25, 222.7) * mm, "end": v(-392.25, 242.5) * mm});
            skLineSegment(sketch, "E287", {"start": v(-372.25, 251.13) * mm, "end": v(-392.25, 270.93) * mm});
            skLineSegment(sketch, "E288", {"start": v(-392.25, 270.93) * mm, "end": v(-372.25, 279.55) * mm});
            skLineSegment(sketch, "E289", {"start": v(-392.25, 214.08) * mm, "end": v(-392.25, 242.5) * mm});
            skLineSegment(sketch, "E290", {"start": v(-372.25, 251.13) * mm, "end": v(-372.25, 279.55) * mm});
            skLineSegment(sketch, "E291", {"start": v(-412.25, 242.5) * mm, "end": v(-392.25, 251.13) * mm});
            skLineSegment(sketch, "E292", {"start": v(-392.25, 251.13) * mm, "end": v(-412.25, 270.93) * mm});
            skLineSegment(sketch, "E293", {"start": v(-412.25, 270.93) * mm, "end": v(-392.25, 279.55) * mm});
            skLineSegment(sketch, "E294", {"start": v(-392.25, 279.55) * mm, "end": v(-412.25, 299.36) * mm});
            skLineSegment(sketch, "E295", {"start": v(-458.02, 299.12) * mm, "end": v(-438.02, 279.31) * mm});
            skLineSegment(sketch, "E296", {"start": v(-438.02, 279.31) * mm, "end": v(-458.02, 270.7) * mm});
            skLineSegment(sketch, "E297", {"start": v(-432.38, 251.57) * mm, "end": v(-452.38, 242.94) * mm});
            skLineSegment(sketch, "E298", {"start": v(-452.38, 242.94) * mm, "end": v(-432.38, 223.14) * mm});
            skLineSegment(sketch, "E299", {"start": v(-518.82, 237.54) * mm, "end": v(-498.82, 217.74) * mm});
            skLineSegment(sketch, "E300", {"start": v(-498.82, 217.74) * mm, "end": v(-518.82, 209.12) * mm});
            skLineSegment(sketch, "E301", {"start": v(-458.02, 299.12) * mm, "end": v(-458.02, 270.7) * mm});
            skLineSegment(sketch, "E302", {"start": v(-432.38, 251.57) * mm, "end": v(-432.38, 223.14) * mm});
            skLineSegment(sketch, "E303", {"start": v(-518.82, 237.54) * mm, "end": v(-518.82, 209.12) * mm});
            skLineSegment(sketch, "E304", {"start": v(-431.97, 299.39) * mm, "end": v(-412.38, 280) * mm});
            skLineSegment(sketch, "E305", {"start": v(-412.38, 280) * mm, "end": v(-432.38, 271.37) * mm});
            skLineSegment(sketch, "E306", {"start": v(-432.38, 271.37) * mm, "end": v(-412.38, 251.57) * mm});
            skLineSegment(sketch, "E307", {"start": v(-423.8, 235.72) * mm, "end": v(-403.8, 215.92) * mm});
            skLineSegment(sketch, "E308", {"start": v(-403.8, 215.92) * mm, "end": v(-423.8, 207.3) * mm});
            skLineSegment(sketch, "E309", {"start": v(-423.8, 235.72) * mm, "end": v(-423.8, 207.3) * mm});
            skLineSegment(sketch, "E310", {"start": v(-452.24, 222.52) * mm, "end": v(-472.24, 242.33) * mm});
            skLineSegment(sketch, "E311", {"start": v(-460.78, 250.45) * mm, "end": v(-480.78, 270.25) * mm});
            skLineSegment(sketch, "E312", {"start": v(-480.78, 270.25) * mm, "end": v(-460.78, 278.88) * mm});
            skLineSegment(sketch, "E313", {"start": v(-472.24, 242.33) * mm, "end": v(-472.24, 250.95) * mm});
            skLineSegment(sketch, "E314", {"start": v(-460.78, 250.45) * mm, "end": v(-460.78, 278.88) * mm});
            skLineSegment(sketch, "E315", {"start": v(-472.24, 222.52) * mm, "end": v(-492.24, 242.33) * mm});
            skLineSegment(sketch, "E316", {"start": v(-492.24, 242.33) * mm, "end": v(-472.24, 250.95) * mm});
            skLineSegment(sketch, "E317", {"start": v(-485.74, 262.63) * mm, "end": v(-505.74, 282.43) * mm});
            skLineSegment(sketch, "E318", {"start": v(-505.74, 282.43) * mm, "end": v(-485.74, 291.06) * mm});
            skLineSegment(sketch, "E319", {"start": v(-485.74, 262.63) * mm, "end": v(-485.74, 291.06) * mm});
            skLineSegment(sketch, "E320", {"start": v(-431.97, 299.39) * mm, "end": v(-412.25, 299.36) * mm});
            skLineSegment(sketch, "E321", {"start": v(-412.25, 242.5) * mm, "end": v(-412.38, 251.57) * mm});
            skLineSegment(sketch, "E322", {"start": v(-364.63, 301.39) * mm, "end": v(-344.63, 281.58) * mm});
            skLineSegment(sketch, "E323", {"start": v(-344.63, 281.58) * mm, "end": v(-364.63, 272.96) * mm});
            skLineSegment(sketch, "E324", {"start": v(-343.16, 268.97) * mm, "end": v(-363.16, 260.35) * mm});
            skLineSegment(sketch, "E325", {"start": v(-363.16, 260.35) * mm, "end": v(-343.16, 240.55) * mm});
            skLineSegment(sketch, "E326", {"start": v(-364.63, 301.39) * mm, "end": v(-364.63, 272.96) * mm});
            skLineSegment(sketch, "E327", {"start": v(-343.16, 268.97) * mm, "end": v(-343.16, 240.55) * mm});
            skLineSegment(sketch, "E328", {"start": v(-344.63, 301.39) * mm, "end": v(-324.63, 281.58) * mm});
            skLineSegment(sketch, "E329", {"start": v(-351.45, 242.48) * mm, "end": v(-371.45, 233.86) * mm});
            skLineSegment(sketch, "E330", {"start": v(-371.45, 233.86) * mm, "end": v(-346.71, 209.37) * mm});
            skLineSegment(sketch, "E331", {"start": v(-344.63, 301.39) * mm, "end": v(-344.63, 301.37) * mm});
            skLineSegment(sketch, "E332", {"start": v(-284.73, 216.04) * mm, "end": v(-264.73, 224.66) * mm});
            skLineSegment(sketch, "E333", {"start": v(-264.73, 224.66) * mm, "end": v(-284.73, 244.46) * mm});
            skLineSegment(sketch, "E334", {"start": v(-292.13, 255.63) * mm, "end": v(-312.13, 275.44) * mm});
            skLineSegment(sketch, "E335", {"start": v(-312.13, 275.44) * mm, "end": v(-292.13, 284.06) * mm});
            skLineSegment(sketch, "E336", {"start": v(-284.73, 216.04) * mm, "end": v(-284.73, 244.46) * mm});
            skLineSegment(sketch, "E337", {"start": v(-292.13, 255.63) * mm, "end": v(-292.13, 284.06) * mm});
            skLineSegment(sketch, "E338", {"start": v(-311.71, 230.62) * mm, "end": v(-331.71, 250.42) * mm});
            skLineSegment(sketch, "E339", {"start": v(-331.71, 250.42) * mm, "end": v(-311.71, 259.04) * mm});
            skLineSegment(sketch, "E340", {"start": v(-311.71, 230.62) * mm, "end": v(-311.71, 259.04) * mm});
            skLineSegment(sketch, "E341", {"start": v(-281.74, 301.39) * mm, "end": v(-261.74, 281.58) * mm});
            skLineSegment(sketch, "E342", {"start": v(-281.74, 272.96) * mm, "end": v(-261.74, 253.16) * mm});
            skLineSegment(sketch, "E343", {"start": v(-281.74, 301.39) * mm, "end": v(-281.74, 272.96) * mm});
            skLineSegment(sketch, "E344", {"start": v(-261.74, 253.16) * mm, "end": v(-261.74, 244.54) * mm});
            skLineSegment(sketch, "E345", {"start": v(-261.74, 272.96) * mm, "end": v(-241.74, 253.16) * mm});
            skLineSegment(sketch, "E346", {"start": v(-241.74, 253.16) * mm, "end": v(-261.74, 244.54) * mm});
            skLineSegment(sketch, "E347", {"start": v(-261.74, 281.58) * mm, "end": v(-261.74, 272.96) * mm});
            skLineSegment(sketch, "E348", {"start": v(-351.45, 242.48) * mm, "end": v(-351.32, 233.42) * mm});
            skLineSegment(sketch, "E349", {"start": v(-324.63, 281.58) * mm, "end": v(-295.3, 293.8) * mm});
            skLineSegment(sketch, "E350", {"start": v(-295.3, 293.8) * mm, "end": v(-344.63, 301.39) * mm});
            skLineSegment(sketch, "E351", {"start": v(-141.78, 214.5) * mm, "end": v(-121.78, 223.13) * mm});
            skLineSegment(sketch, "E352", {"start": v(-121.78, 223.13) * mm, "end": v(-141.78, 242.93) * mm});
            skLineSegment(sketch, "E353", {"start": v(-121.78, 251.55) * mm, "end": v(-141.78, 271.36) * mm});
            skLineSegment(sketch, "E354", {"start": v(-141.78, 271.36) * mm, "end": v(-121.78, 279.98) * mm});
            skLineSegment(sketch, "E355", {"start": v(-141.78, 214.5) * mm, "end": v(-141.78, 242.93) * mm});
            skLineSegment(sketch, "E356", {"start": v(-121.78, 251.55) * mm, "end": v(-121.78, 279.98) * mm});
            skLineSegment(sketch, "E357", {"start": v(-161.78, 242.93) * mm, "end": v(-141.78, 251.55) * mm});
            skLineSegment(sketch, "E358", {"start": v(-141.78, 251.55) * mm, "end": v(-161.78, 271.36) * mm});
            skLineSegment(sketch, "E359", {"start": v(-161.78, 271.36) * mm, "end": v(-141.78, 279.98) * mm});
            skLineSegment(sketch, "E360", {"start": v(-141.78, 279.98) * mm, "end": v(-161.78, 299.78) * mm});
            skLineSegment(sketch, "E361", {"start": v(-207.56, 299.54) * mm, "end": v(-187.56, 279.74) * mm});
            skLineSegment(sketch, "E362", {"start": v(-187.56, 279.74) * mm, "end": v(-207.56, 271.12) * mm});
            skLineSegment(sketch, "E363", {"start": v(-181.92, 252) * mm, "end": v(-201.92, 243.37) * mm});
            skLineSegment(sketch, "E364", {"start": v(-201.92, 243.37) * mm, "end": v(-181.92, 223.57) * mm});
            skLineSegment(sketch, "E365", {"start": v(-207.56, 299.54) * mm, "end": v(-207.56, 271.12) * mm});
            skLineSegment(sketch, "E366", {"start": v(-181.92, 252) * mm, "end": v(-181.92, 223.57) * mm});
            skLineSegment(sketch, "E367", {"start": v(-181.5, 299.81) * mm, "end": v(-161.92, 280.42) * mm});
            skLineSegment(sketch, "E368", {"start": v(-161.92, 280.42) * mm, "end": v(-181.92, 271.8) * mm});
            skLineSegment(sketch, "E369", {"start": v(-181.92, 271.8) * mm, "end": v(-161.92, 252) * mm});
            skLineSegment(sketch, "E370", {"start": v(-170.4, 238.3) * mm, "end": v(-150.4, 218.5) * mm});
            skLineSegment(sketch, "E371", {"start": v(-150.4, 218.5) * mm, "end": v(-170.4, 209.88) * mm});
            skLineSegment(sketch, "E372", {"start": v(-170.4, 238.3) * mm, "end": v(-170.4, 209.88) * mm});
            skLineSegment(sketch, "E373", {"start": v(-216.18, 212.3) * mm, "end": v(-236.18, 232.1) * mm});
            skLineSegment(sketch, "E374", {"start": v(-210.31, 250.88) * mm, "end": v(-230.31, 270.68) * mm});
            skLineSegment(sketch, "E375", {"start": v(-230.31, 270.68) * mm, "end": v(-210.31, 279.3) * mm});
            skLineSegment(sketch, "E376", {"start": v(-236.18, 232.1) * mm, "end": v(-236.18, 240.72) * mm});
            skLineSegment(sketch, "E377", {"start": v(-210.31, 250.88) * mm, "end": v(-210.31, 279.3) * mm});
            skLineSegment(sketch, "E378", {"start": v(-236.18, 212.3) * mm, "end": v(-256.18, 232.1) * mm});
            skLineSegment(sketch, "E379", {"start": v(-256.18, 232.1) * mm, "end": v(-236.18, 240.72) * mm});
            skLineSegment(sketch, "E380", {"start": v(-236.18, 264.86) * mm, "end": v(-256.18, 284.66) * mm});
            skLineSegment(sketch, "E381", {"start": v(-256.18, 284.66) * mm, "end": v(-236.18, 293.29) * mm});
            skLineSegment(sketch, "E382", {"start": v(-236.18, 264.86) * mm, "end": v(-236.18, 293.29) * mm});
            skLineSegment(sketch, "E383", {"start": v(-181.5, 299.81) * mm, "end": v(-161.78, 299.78) * mm});
            skLineSegment(sketch, "E384", {"start": v(-161.78, 242.93) * mm, "end": v(-161.92, 252) * mm});
            skLineSegment(sketch, "E385", {"start": v(-113.28, 301.15) * mm, "end": v(-93.28, 281.35) * mm});
            skLineSegment(sketch, "E386", {"start": v(-93.28, 281.35) * mm, "end": v(-113.28, 272.73) * mm});
            skLineSegment(sketch, "E387", {"start": v(-93.28, 252.92) * mm, "end": v(-113.28, 244.3) * mm});
            skLineSegment(sketch, "E388", {"start": v(-113.28, 244.3) * mm, "end": v(-93.28, 224.5) * mm});
            skLineSegment(sketch, "E389", {"start": v(-113.28, 301.15) * mm, "end": v(-113.28, 272.73) * mm});
            skLineSegment(sketch, "E390", {"start": v(-93.28, 252.92) * mm, "end": v(-93.28, 224.5) * mm});
            skLineSegment(sketch, "E391", {"start": v(-97.33, 295.58) * mm, "end": v(-77.33, 275.78) * mm});
            skLineSegment(sketch, "E392", {"start": v(-64.96, 231.42) * mm, "end": v(-90.34, 220.48) * mm});
            skLineSegment(sketch, "E393", {"start": v(-53.15, 215.44) * mm, "end": v(-33.15, 224.06) * mm});
            skLineSegment(sketch, "E394", {"start": v(-33.15, 224.06) * mm, "end": v(-53.15, 243.87) * mm});
            skLineSegment(sketch, "E395", {"start": v(-40.82, 249.78) * mm, "end": v(-60.82, 269.58) * mm});
            skLineSegment(sketch, "E396", {"start": v(-60.82, 269.58) * mm, "end": v(-40.82, 278.2) * mm});
            skLineSegment(sketch, "E397", {"start": v(-53.15, 215.44) * mm, "end": v(-53.15, 243.87) * mm});
            skLineSegment(sketch, "E398", {"start": v(-40.82, 249.78) * mm, "end": v(-40.82, 278.2) * mm});
            skLineSegment(sketch, "E399", {"start": v(-69.84, 243.92) * mm, "end": v(-89.84, 263.72) * mm});
            skLineSegment(sketch, "E400", {"start": v(-89.84, 263.72) * mm, "end": v(-69.84, 272.34) * mm});
            skLineSegment(sketch, "E401", {"start": v(-69.84, 243.92) * mm, "end": v(-69.84, 272.34) * mm});
            skLineSegment(sketch, "E402", {"start": v(-64.96, 231.42) * mm, "end": v(-64.87, 225.38) * mm});
            skLineSegment(sketch, "E403", {"start": v(-77.33, 275.78) * mm, "end": v(-48.01, 287.99) * mm});
            skLineSegment(sketch, "E404", {"start": v(-48.01, 287.99) * mm, "end": v(-97.33, 295.58) * mm});
            skLineSegment(sketch, "E405", {"start": v(-33.15, 302.74) * mm, "end": v(-13.15, 282.94) * mm});
            skLineSegment(sketch, "E406", {"start": v(-13.15, 282.94) * mm, "end": v(-33.15, 274.32) * mm});
            skLineSegment(sketch, "E407", {"start": v(-7.51, 255.2) * mm, "end": v(-27.51, 246.57) * mm});
            skLineSegment(sketch, "E408", {"start": v(-27.51, 246.57) * mm, "end": v(-7.51, 226.77) * mm});
            skLineSegment(sketch, "E409", {"start": v(-33.15, 302.74) * mm, "end": v(-33.15, 274.32) * mm});
            skLineSegment(sketch, "E410", {"start": v(-7.51, 255.2) * mm, "end": v(-7.51, 226.77) * mm});
            skLineSegment(sketch, "E411", {"start": v(-602.62, 212.74) * mm, "end": v(-582.62, 221.36) * mm});
            skLineSegment(sketch, "E412", {"start": v(-582.62, 221.36) * mm, "end": v(-602.62, 241.17) * mm});
            skLineSegment(sketch, "E413", {"start": v(-602.62, 212.74) * mm, "end": v(-602.62, 241.17) * mm});
            skLineSegment(sketch, "E414", {"start": v(-588, 258.17) * mm, "end": v(-610.21, 280.17) * mm});
            skLineSegment(sketch, "E415", {"start": v(-610.21, 280.17) * mm, "end": v(-588, 289.74) * mm});
            skLineSegment(sketch, "E416", {"start": v(-588, 258.17) * mm, "end": v(-588, 289.74) * mm});
            skLineSegment(sketch, "E417", {"start": v(-346.71, 209.37) * mm, "end": v(-324.85, 207.2) * mm});
            skLineSegment(sketch, "E418", {"start": v(-351.32, 233.42) * mm, "end": v(-324.85, 207.2) * mm});
            skLineSegment(sketch, "E419", {"start": v(-472.24, 222.52) * mm, "end": v(-452.24, 222.52) * mm});
            skLineSegment(sketch, "E420", {"start": v(-236.18, 212.3) * mm, "end": v(-216.18, 212.3) * mm});
            skLineSegment(sketch, "E421", {"start": v(-90.34, 220.48) * mm, "end": v(-80.03, 209.7) * mm});
            skLineSegment(sketch, "E422", {"start": v(-80.03, 209.7) * mm, "end": v(-54.02, 206.8) * mm});
            skLineSegment(sketch, "E423", {"start": v(-54.02, 206.8) * mm, "end": v(-64.87, 225.38) * mm});
            skSolve(sketch);
        }
        {
            var Q0;
            Q0=makeQuery(id+"F8.imprint","IMPRINT",FACE,{"disambiguationData":[TD([[makeQuery(id+"F8.imprint","IMPRINT",EDGE,{"derivedFrom":sQuery(id+"F8.wireOp",EDGE,"E414")}),-1.0]])]});
            var Q1;
            {var subQ0=sQuery(id+"F8.wireOp",EDGE,"E283");var subQ1=sQuery(id+"F8.wireOp",EDGE,"E262");var subQ2=makeQuery(id+"F8.imprint","INTERSECT",VERTEX,{"derivedFrom":[subQ1,subQ0]});Q1=makeQuery(id+"F8.imprint","IMPRINT",FACE,{"disambiguationData":[TD([[makeQuery(id+"F8.imprint","IMPRINT",EDGE,{"disambiguationData":[TD([[subQ2,1.0]])],"derivedFrom":subQ1}),1.0]])]});}
            var Q2;
            {var subQ0=sQuery(id+"F8.wireOp",EDGE,"E284");Q2=makeQuery(id+"F8.imprint","IMPRINT",FACE,{"disambiguationData":[TD([[makeQuery(id+"F8.imprint","IMPRINT",EDGE,{"derivedFrom":subQ0}),1.0]])]});}
            var Q3;
            Q3=makeQuery(id+"F8.imprint","IMPRINT",FACE,{"disambiguationData":[TD([[makeQuery(id+"F8.imprint","IMPRINT",EDGE,{"derivedFrom":sQuery(id+"F8.wireOp",EDGE,"E270")}),-1.0]])]});
            var Q4;
            Q4=makeQuery(id+"F8.imprint","IMPRINT",FACE,{"disambiguationData":[TD([[makeQuery(id+"F8.imprint","IMPRINT",EDGE,{"derivedFrom":sQuery(id+"F8.wireOp",EDGE,"E279")}),-1.0]])]});
            var Q5;
            Q5=makeQuery(id+"F8.imprint","IMPRINT",FACE,{"disambiguationData":[TD([[makeQuery(id+"F8.imprint","IMPRINT",EDGE,{"derivedFrom":sQuery(id+"F8.wireOp",EDGE,"E411")}),1.0]])]});
            var Q6;
            Q6=makeQuery(id+"F8.imprint","IMPRINT",FACE,{"disambiguationData":[TD([[makeQuery(id+"F8.imprint","IMPRINT",EDGE,{"derivedFrom":sQuery(id+"F8.wireOp",EDGE,"E264")}),1.0]])]});
            var Q7;
            Q7=makeQuery(id+"F8.imprint","IMPRINT",FACE,{"disambiguationData":[TD([[makeQuery(id+"F8.imprint","IMPRINT",EDGE,{"derivedFrom":sQuery(id+"F8.wireOp",EDGE,"E266")}),-1.0]])]});
            var Q8;
            {var subQ1=sQuery(id+"F8.wireOp",EDGE,"E274");Q8=makeQuery(id+"F8.imprint","IMPRINT",FACE,{"disambiguationData":[TD([[makeQuery(id+"F8.imprint","IMPRINT",EDGE,{"derivedFrom":subQ1}),1.0]])]});}
            var Q9;
            {var subQ0=sQuery(id+"F8.wireOp",EDGE,"E275");var subQ1=sQuery(id+"F8.wireOp",EDGE,"E273");var subQ2=makeQuery(id+"F8.imprint","INTERSECT",VERTEX,{"derivedFrom":[subQ1,subQ0]});Q9=makeQuery(id+"F8.imprint","IMPRINT",FACE,{"disambiguationData":[TD([[makeQuery(id+"F8.imprint","IMPRINT",EDGE,{"disambiguationData":[TD([[subQ2,-1.0]])],"derivedFrom":subQ1}),-1.0]])]});}
            var Q10;
            {var subQ0=sQuery(id+"F8.wireOp",EDGE,"E317");Q10=makeQuery(id+"F8.imprint","IMPRINT",FACE,{"disambiguationData":[TD([[makeQuery(id+"F8.imprint","IMPRINT",EDGE,{"derivedFrom":subQ0}),-1.0]])]});}
            var Q11;
            Q11=makeQuery(id+"F8.imprint","IMPRINT",FACE,{"disambiguationData":[TD([[makeQuery(id+"F8.imprint","IMPRINT",EDGE,{"derivedFrom":sQuery(id+"F8.wireOp",EDGE,"E299")}),-1.0]])]});
            var Q12;
            Q12=makeQuery(id+"F8.imprint","IMPRINT",FACE,{"disambiguationData":[TD([[makeQuery(id+"F8.imprint","IMPRINT",EDGE,{"derivedFrom":sQuery(id+"F8.wireOp",EDGE,"E310")}),1.0]])]});
            var Q13;
            Q13=makeQuery(id+"F8.imprint","IMPRINT",FACE,{"disambiguationData":[TD([[makeQuery(id+"F8.imprint","IMPRINT",EDGE,{"derivedFrom":sQuery(id+"F8.wireOp",EDGE,"E311")}),-1.0]])]});
            var Q14;
            {var subQ0=sQuery(id+"F8.wireOp",EDGE,"E296");Q14=makeQuery(id+"F8.imprint","IMPRINT",FACE,{"disambiguationData":[TD([[makeQuery(id+"F8.imprint","IMPRINT",EDGE,{"derivedFrom":subQ0}),-1.0]])]});}
            var Q15;
            {var subQ0=sQuery(id+"F8.wireOp",EDGE,"E301");var subQ1=sQuery(id+"F8.wireOp",EDGE,"E295");var subQ2=makeQuery(id+"F8.imprint","INTERSECT",VERTEX,{"derivedFrom":[subQ1,subQ0]});Q15=makeQuery(id+"F8.imprint","IMPRINT",FACE,{"disambiguationData":[TD([[makeQuery(id+"F8.imprint","IMPRINT",EDGE,{"disambiguationData":[TD([[subQ2,-1.0]])],"derivedFrom":subQ1}),-1.0]])]});}
            var Q16;
            {var subQ0=sQuery(id+"F8.wireOp",EDGE,"E320");Q16=makeQuery(id+"F8.imprint","IMPRINT",FACE,{"disambiguationData":[TD([[makeQuery(id+"F8.imprint","IMPRINT",EDGE,{"derivedFrom":subQ0}),-1.0]])]});}
            var Q17;
            Q17=makeQuery(id+"F8.imprint","IMPRINT",FACE,{"disambiguationData":[TD([[makeQuery(id+"F8.imprint","IMPRINT",EDGE,{"derivedFrom":sQuery(id+"F8.wireOp",EDGE,"E291")}),1.0]])]});
            var Q18;
            Q18=makeQuery(id+"F8.imprint","IMPRINT",FACE,{"disambiguationData":[TD([[makeQuery(id+"F8.imprint","IMPRINT",EDGE,{"derivedFrom":sQuery(id+"F8.wireOp",EDGE,"E297")}),1.0]])]});
            var Q19;
            Q19=makeQuery(id+"F8.imprint","IMPRINT",FACE,{"disambiguationData":[TD([[makeQuery(id+"F8.imprint","IMPRINT",EDGE,{"derivedFrom":sQuery(id+"F8.wireOp",EDGE,"E307")}),-1.0]])]});
            var Q20;
            Q20=makeQuery(id+"F8.imprint","IMPRINT",FACE,{"disambiguationData":[TD([[makeQuery(id+"F8.imprint","IMPRINT",EDGE,{"derivedFrom":sQuery(id+"F8.wireOp",EDGE,"E285")}),1.0]])]});
            var Q21;
            Q21=makeQuery(id+"F8.imprint","IMPRINT",FACE,{"disambiguationData":[TD([[makeQuery(id+"F8.imprint","IMPRINT",EDGE,{"derivedFrom":sQuery(id+"F8.wireOp",EDGE,"E287")}),-1.0]])]});
            var Q22;
            {var subQ0=sQuery(id+"F8.wireOp",EDGE,"E323");Q22=makeQuery(id+"F8.imprint","IMPRINT",FACE,{"disambiguationData":[TD([[makeQuery(id+"F8.imprint","IMPRINT",EDGE,{"derivedFrom":subQ0}),-1.0]])]});}
            var Q23;
            {var subQ0=sQuery(id+"F8.wireOp",EDGE,"E326");var subQ1=sQuery(id+"F8.wireOp",EDGE,"E322");var subQ2=makeQuery(id+"F8.imprint","INTERSECT",VERTEX,{"derivedFrom":[subQ1,subQ0]});Q23=makeQuery(id+"F8.imprint","IMPRINT",FACE,{"disambiguationData":[TD([[makeQuery(id+"F8.imprint","IMPRINT",EDGE,{"disambiguationData":[TD([[subQ2,-1.0]])],"derivedFrom":subQ1}),-1.0]])]});}
            var Q24;
            {var subQ0=sQuery(id+"F8.wireOp",EDGE,"E350");Q24=makeQuery(id+"F8.imprint","IMPRINT",FACE,{"disambiguationData":[TD([[makeQuery(id+"F8.imprint","IMPRINT",EDGE,{"derivedFrom":subQ0}),1.0]])]});}
            var Q25;
            {var subQ0=sQuery(id+"F8.wireOp",EDGE,"E349");var subQ1=sQuery(id+"F8.wireOp",EDGE,"E328");var subQ2=makeQuery(id+"F8.imprint","INTERSECT",VERTEX,{"derivedFrom":[subQ1,subQ0]});Q25=makeQuery(id+"F8.imprint","IMPRINT",FACE,{"disambiguationData":[TD([[makeQuery(id+"F8.imprint","IMPRINT",EDGE,{"disambiguationData":[TD([[subQ2,1.0]])],"derivedFrom":subQ1}),1.0]])]});}
            var Q26;
            Q26=makeQuery(id+"F8.imprint","IMPRINT",FACE,{"disambiguationData":[TD([[makeQuery(id+"F8.imprint","IMPRINT",EDGE,{"derivedFrom":sQuery(id+"F8.wireOp",EDGE,"E324")}),1.0]])]});
            var Q27;
            Q27=makeQuery(id+"F8.imprint","IMPRINT",FACE,{"disambiguationData":[TD([[makeQuery(id+"F8.imprint","IMPRINT",EDGE,{"derivedFrom":sQuery(id+"F8.wireOp",EDGE,"E329")}),1.0]])]});
            var Q28;
            Q28=makeQuery(id+"F8.imprint","IMPRINT",FACE,{"disambiguationData":[TD([[makeQuery(id+"F8.imprint","IMPRINT",EDGE,{"derivedFrom":sQuery(id+"F8.wireOp",EDGE,"E338")}),-1.0]])]});
            var Q29;
            Q29=makeQuery(id+"F8.imprint","IMPRINT",FACE,{"disambiguationData":[TD([[makeQuery(id+"F8.imprint","IMPRINT",EDGE,{"derivedFrom":sQuery(id+"F8.wireOp",EDGE,"E334")}),-1.0]])]});
            var Q30;
            {var subQ1=sQuery(id+"F8.wireOp",EDGE,"E342");Q30=makeQuery(id+"F8.imprint","IMPRINT",FACE,{"disambiguationData":[TD([[makeQuery(id+"F8.imprint","IMPRINT",EDGE,{"derivedFrom":subQ1}),1.0]])]});}
            var Q31;
            {var subQ0=sQuery(id+"F8.wireOp",EDGE,"E343");var subQ1=sQuery(id+"F8.wireOp",EDGE,"E341");var subQ2=makeQuery(id+"F8.imprint","INTERSECT",VERTEX,{"derivedFrom":[subQ1,subQ0]});Q31=makeQuery(id+"F8.imprint","IMPRINT",FACE,{"disambiguationData":[TD([[makeQuery(id+"F8.imprint","IMPRINT",EDGE,{"disambiguationData":[TD([[subQ2,-1.0]])],"derivedFrom":subQ1}),-1.0]])]});}
            var Q32;
            Q32=makeQuery(id+"F8.imprint","IMPRINT",FACE,{"disambiguationData":[TD([[makeQuery(id+"F8.imprint","IMPRINT",EDGE,{"derivedFrom":sQuery(id+"F8.wireOp",EDGE,"E332")}),1.0]])]});
            var Q33;
            Q33=makeQuery(id+"F8.imprint","IMPRINT",FACE,{"disambiguationData":[TD([[makeQuery(id+"F8.imprint","IMPRINT",EDGE,{"derivedFrom":sQuery(id+"F8.wireOp",EDGE,"E373")}),1.0]])]});
            var Q34;
            {var subQ0=sQuery(id+"F8.wireOp",EDGE,"E380");Q34=makeQuery(id+"F8.imprint","IMPRINT",FACE,{"disambiguationData":[TD([[makeQuery(id+"F8.imprint","IMPRINT",EDGE,{"derivedFrom":subQ0}),-1.0]])]});}
            var Q35;
            {var subQ0=sQuery(id+"F8.wireOp",EDGE,"E382");var subQ1=sQuery(id+"F8.wireOp",EDGE,"E381");var subQ2=makeQuery(id+"F8.imprint","INTERSECT",VERTEX,{"derivedFrom":[subQ1,subQ0]});Q35=makeQuery(id+"F8.imprint","IMPRINT",FACE,{"disambiguationData":[TD([[makeQuery(id+"F8.imprint","IMPRINT",EDGE,{"disambiguationData":[TD([[subQ2,1.0]])],"derivedFrom":subQ1}),-1.0]])]});}
            var Q36;
            {var subQ0=sQuery(id+"F8.wireOp",EDGE,"E365");var subQ1=sQuery(id+"F8.wireOp",EDGE,"E361");var subQ2=makeQuery(id+"F8.imprint","INTERSECT",VERTEX,{"derivedFrom":[subQ1,subQ0]});Q36=makeQuery(id+"F8.imprint","IMPRINT",FACE,{"disambiguationData":[TD([[makeQuery(id+"F8.imprint","IMPRINT",EDGE,{"disambiguationData":[TD([[subQ2,-1.0]])],"derivedFrom":subQ1}),-1.0]])]});}
            var Q37;
            {var subQ0=sQuery(id+"F8.wireOp",EDGE,"E362");Q37=makeQuery(id+"F8.imprint","IMPRINT",FACE,{"disambiguationData":[TD([[makeQuery(id+"F8.imprint","IMPRINT",EDGE,{"derivedFrom":subQ0}),-1.0]])]});}
            var Q38;
            Q38=makeQuery(id+"F8.imprint","IMPRINT",FACE,{"disambiguationData":[TD([[makeQuery(id+"F8.imprint","IMPRINT",EDGE,{"derivedFrom":sQuery(id+"F8.wireOp",EDGE,"E374")}),-1.0]])]});
            var Q39;
            Q39=makeQuery(id+"F8.imprint","IMPRINT",FACE,{"disambiguationData":[TD([[makeQuery(id+"F8.imprint","IMPRINT",EDGE,{"derivedFrom":sQuery(id+"F8.wireOp",EDGE,"E363")}),1.0]])]});
            var Q40;
            Q40=makeQuery(id+"F8.imprint","IMPRINT",FACE,{"disambiguationData":[TD([[makeQuery(id+"F8.imprint","IMPRINT",EDGE,{"derivedFrom":sQuery(id+"F8.wireOp",EDGE,"E370")}),-1.0]])]});
            var Q41;
            Q41=makeQuery(id+"F8.imprint","IMPRINT",FACE,{"disambiguationData":[TD([[makeQuery(id+"F8.imprint","IMPRINT",EDGE,{"derivedFrom":sQuery(id+"F8.wireOp",EDGE,"E357")}),1.0]])]});
            var Q42;
            {var subQ0=sQuery(id+"F8.wireOp",EDGE,"E383");Q42=makeQuery(id+"F8.imprint","IMPRINT",FACE,{"disambiguationData":[TD([[makeQuery(id+"F8.imprint","IMPRINT",EDGE,{"derivedFrom":subQ0}),-1.0]])]});}
            var Q43;
            {var subQ0=sQuery(id+"F8.wireOp",EDGE,"E389");var subQ1=sQuery(id+"F8.wireOp",EDGE,"E385");var subQ2=makeQuery(id+"F8.imprint","INTERSECT",VERTEX,{"derivedFrom":[subQ1,subQ0]});Q43=makeQuery(id+"F8.imprint","IMPRINT",FACE,{"disambiguationData":[TD([[makeQuery(id+"F8.imprint","IMPRINT",EDGE,{"disambiguationData":[TD([[subQ2,-1.0]])],"derivedFrom":subQ1}),-1.0]])]});}
            var Q44;
            {var subQ0=sQuery(id+"F8.wireOp",EDGE,"E386");Q44=makeQuery(id+"F8.imprint","IMPRINT",FACE,{"disambiguationData":[TD([[makeQuery(id+"F8.imprint","IMPRINT",EDGE,{"derivedFrom":subQ0}),-1.0]])]});}
            var Q45;
            Q45=makeQuery(id+"F8.imprint","IMPRINT",FACE,{"disambiguationData":[TD([[makeQuery(id+"F8.imprint","IMPRINT",EDGE,{"derivedFrom":sQuery(id+"F8.wireOp",EDGE,"E353")}),-1.0]])]});
            var Q46;
            Q46=makeQuery(id+"F8.imprint","IMPRINT",FACE,{"disambiguationData":[TD([[makeQuery(id+"F8.imprint","IMPRINT",EDGE,{"derivedFrom":sQuery(id+"F8.wireOp",EDGE,"E387")}),1.0]])]});
            var Q47;
            Q47=makeQuery(id+"F8.imprint","IMPRINT",FACE,{"disambiguationData":[TD([[makeQuery(id+"F8.imprint","IMPRINT",EDGE,{"derivedFrom":sQuery(id+"F8.wireOp",EDGE,"E351")}),1.0]])]});
            var Q48;
            Q48=makeQuery(id+"F8.imprint","IMPRINT",FACE,{"disambiguationData":[TD([[makeQuery(id+"F8.imprint","IMPRINT",EDGE,{"derivedFrom":sQuery(id+"F8.wireOp",EDGE,"E392")}),1.0]])]});
            var Q49;
            Q49=makeQuery(id+"F8.imprint","IMPRINT",FACE,{"disambiguationData":[TD([[makeQuery(id+"F8.imprint","IMPRINT",EDGE,{"derivedFrom":sQuery(id+"F8.wireOp",EDGE,"E393")}),1.0]])]});
            var Q50;
            Q50=makeQuery(id+"F8.imprint","IMPRINT",FACE,{"disambiguationData":[TD([[makeQuery(id+"F8.imprint","IMPRINT",EDGE,{"derivedFrom":sQuery(id+"F8.wireOp",EDGE,"E407")}),1.0]])]});
            var Q51;
            Q51=makeQuery(id+"F8.imprint","IMPRINT",FACE,{"disambiguationData":[TD([[makeQuery(id+"F8.imprint","IMPRINT",EDGE,{"derivedFrom":sQuery(id+"F8.wireOp",EDGE,"E395")}),-1.0]])]});
            var Q52;
            Q52=makeQuery(id+"F8.imprint","IMPRINT",FACE,{"disambiguationData":[TD([[makeQuery(id+"F8.imprint","IMPRINT",EDGE,{"derivedFrom":sQuery(id+"F8.wireOp",EDGE,"E399")}),-1.0]])]});
            var Q53;
            {var subQ0=sQuery(id+"F8.wireOp",EDGE,"E403");Q53=makeQuery(id+"F8.imprint","IMPRINT",FACE,{"disambiguationData":[TD([[makeQuery(id+"F8.imprint","IMPRINT",EDGE,{"derivedFrom":subQ0}),1.0]])]});}
            var Q54;
            {var subQ0=sQuery(id+"F8.wireOp",EDGE,"E404");var subQ1=sQuery(id+"F8.wireOp",EDGE,"E391");var subQ2=makeQuery(id+"F8.imprint","INTERSECT",VERTEX,{"derivedFrom":[subQ1,subQ0]});Q54=makeQuery(id+"F8.imprint","IMPRINT",FACE,{"disambiguationData":[TD([[makeQuery(id+"F8.imprint","IMPRINT",EDGE,{"disambiguationData":[TD([[subQ2,-1.0]])],"derivedFrom":subQ1}),1.0]])]});}
            var Q55;
            {var subQ0=sQuery(id+"F8.wireOp",EDGE,"E409");var subQ1=sQuery(id+"F8.wireOp",EDGE,"E405");var subQ2=makeQuery(id+"F8.imprint","INTERSECT",VERTEX,{"derivedFrom":[subQ1,subQ0]});Q55=makeQuery(id+"F8.imprint","IMPRINT",FACE,{"disambiguationData":[TD([[makeQuery(id+"F8.imprint","IMPRINT",EDGE,{"disambiguationData":[TD([[subQ2,-1.0]])],"derivedFrom":subQ1}),-1.0]])]});}
            var Q56;
            {var subQ0=sQuery(id+"F8.wireOp",EDGE,"E406");Q56=makeQuery(id+"F8.imprint","IMPRINT",FACE,{"disambiguationData":[TD([[makeQuery(id+"F8.imprint","IMPRINT",EDGE,{"derivedFrom":subQ0}),-1.0]])]});}
            extrude(context, id + "F9", {"entities" : qUnion([Q0, Q1, Q2, Q3, Q4, Q5, Q6, Q7, Q8, Q9, Q10, Q11, Q12, Q13, Q14, Q15, Q16, Q17, Q18, Q19, Q20, Q21, Q22, Q23, Q24, Q25, Q26, Q27, Q28, Q29, Q30, Q31, Q32, Q33, Q34, Q35, Q36, Q37, Q38, Q39, Q40, Q41, Q42, Q43, Q44, Q45, Q46, Q47, Q48, Q49, Q50, Q51, Q52, Q53, Q54, Q55, Q56]), "operationType" : NewBodyOperationType.REMOVE, "oppositeDirection" : true, "depth" : 25.4 * mm});
        }
        {
            var Q0;
            Q0=makeQuery(id+"F7.imprint","IMPRINT",FACE,{"disambiguationData":[TD([[makeQuery(id+"F7.imprint","IMPRINT",EDGE,{"derivedFrom":sQuery(id+"F7.wireOp",EDGE,"E30")}),1.0]])]});
            var Q1;
            Q1=makeQuery(id+"F7.imprint","IMPRINT",FACE,{"disambiguationData":[TD([[makeQuery(id+"F7.imprint","IMPRINT",EDGE,{"derivedFrom":sQuery(id+"F7.wireOp",EDGE,"E254")}),-1.0]])]});
            var Q2;
            Q2=makeQuery(id+"F7.imprint","IMPRINT",FACE,{"disambiguationData":[TD([[makeQuery(id+"F7.imprint","IMPRINT",EDGE,{"derivedFrom":sQuery(id+"F7.wireOp",EDGE,"E40")}),-1.0]])]});
            var Q3;
            Q3=makeQuery(id+"F7.imprint","IMPRINT",FACE,{"disambiguationData":[TD([[makeQuery(id+"F7.imprint","IMPRINT",EDGE,{"derivedFrom":sQuery(id+"F7.wireOp",EDGE,"E31")}),-1.0]])]});
            var Q4;
            Q4=makeQuery(id+"F7.imprint","IMPRINT",FACE,{"disambiguationData":[TD([[makeQuery(id+"F7.imprint","IMPRINT",EDGE,{"derivedFrom":sQuery(id+"F7.wireOp",EDGE,"E33")}),1.0]])]});
            var Q5;
            Q5=makeQuery(id+"F7.imprint","IMPRINT",FACE,{"disambiguationData":[TD([[makeQuery(id+"F7.imprint","IMPRINT",EDGE,{"derivedFrom":sQuery(id+"F7.wireOp",EDGE,"E45")}),-1.0]])]});
            var Q6;
            Q6=makeQuery(id+"F7.imprint","IMPRINT",FACE,{"disambiguationData":[TD([[makeQuery(id+"F7.imprint","IMPRINT",EDGE,{"derivedFrom":sQuery(id+"F7.wireOp",EDGE,"E35")}),-1.0]])]});
            var Q7;
            Q7=makeQuery(id+"F7.imprint","IMPRINT",FACE,{"disambiguationData":[TD([[makeQuery(id+"F7.imprint","IMPRINT",EDGE,{"derivedFrom":sQuery(id+"F7.wireOp",EDGE,"E43")}),-1.0]])]});
            var Q8;
            Q8=makeQuery(id+"F7.imprint","IMPRINT",FACE,{"disambiguationData":[TD([[makeQuery(id+"F7.imprint","IMPRINT",EDGE,{"derivedFrom":sQuery(id+"F7.wireOp",EDGE,"E96")}),-1.0]])]});
            var Q9;
            Q9=makeQuery(id+"F7.imprint","IMPRINT",FACE,{"disambiguationData":[TD([[makeQuery(id+"F7.imprint","IMPRINT",EDGE,{"derivedFrom":sQuery(id+"F7.wireOp",EDGE,"E89")}),-1.0]])]});
            var Q10;
            Q10=makeQuery(id+"F7.imprint","IMPRINT",FACE,{"disambiguationData":[TD([[makeQuery(id+"F7.imprint","IMPRINT",EDGE,{"derivedFrom":sQuery(id+"F7.wireOp",EDGE,"E87")}),-1.0]])]});
            var Q11;
            Q11=makeQuery(id+"F7.imprint","IMPRINT",FACE,{"disambiguationData":[TD([[makeQuery(id+"F7.imprint","IMPRINT",EDGE,{"derivedFrom":sQuery(id+"F7.wireOp",EDGE,"E52")}),-1.0]])]});
            var Q12;
            Q12=makeQuery(id+"F7.imprint","IMPRINT",FACE,{"disambiguationData":[TD([[makeQuery(id+"F7.imprint","IMPRINT",EDGE,{"derivedFrom":sQuery(id+"F7.wireOp",EDGE,"E74")}),1.0]])]});
            var Q13;
            Q13=makeQuery(id+"F7.imprint","IMPRINT",FACE,{"disambiguationData":[TD([[makeQuery(id+"F7.imprint","IMPRINT",EDGE,{"derivedFrom":sQuery(id+"F7.wireOp",EDGE,"E76")}),-1.0]])]});
            var Q14;
            Q14=makeQuery(id+"F7.imprint","IMPRINT",FACE,{"disambiguationData":[TD([[makeQuery(id+"F7.imprint","IMPRINT",EDGE,{"derivedFrom":sQuery(id+"F7.wireOp",EDGE,"E72")}),-1.0]])]});
            var Q15;
            Q15=makeQuery(id+"F7.imprint","IMPRINT",FACE,{"disambiguationData":[TD([[makeQuery(id+"F7.imprint","IMPRINT",EDGE,{"derivedFrom":sQuery(id+"F7.wireOp",EDGE,"E68")}),1.0]])]});
            var Q16;
            Q16=makeQuery(id+"F7.imprint","IMPRINT",FACE,{"disambiguationData":[TD([[makeQuery(id+"F7.imprint","IMPRINT",EDGE,{"derivedFrom":sQuery(id+"F7.wireOp",EDGE,"E84")}),-1.0]])]});
            var Q17;
            Q17=makeQuery(id+"F7.imprint","IMPRINT",FACE,{"disambiguationData":[TD([[makeQuery(id+"F7.imprint","IMPRINT",EDGE,{"derivedFrom":sQuery(id+"F7.wireOp",EDGE,"E67")}),1.0]])]});
            var Q18;
            {var subQ0=sQuery(id+"F7.wireOp",EDGE,"E59");Q18=makeQuery(id+"F7.imprint","IMPRINT",FACE,{"disambiguationData":[TD([[makeQuery(id+"F7.imprint","IMPRINT",EDGE,{"derivedFrom":subQ0}),-1.0]])]});}
            var Q19;
            Q19=makeQuery(id+"F7.imprint","IMPRINT",FACE,{"disambiguationData":[TD([[makeQuery(id+"F7.imprint","IMPRINT",EDGE,{"derivedFrom":sQuery(id+"F7.wireOp",EDGE,"E60")}),1.0]])]});
            var Q20;
            Q20=makeQuery(id+"F7.imprint","IMPRINT",FACE,{"disambiguationData":[TD([[makeQuery(id+"F7.imprint","IMPRINT",EDGE,{"derivedFrom":sQuery(id+"F7.wireOp",EDGE,"E62")}),-1.0]])]});
            var Q21;
            {var subQ0=sQuery(id+"F7.wireOp",EDGE,"E105");Q21=makeQuery(id+"F7.imprint","IMPRINT",FACE,{"disambiguationData":[TD([[makeQuery(id+"F7.imprint","IMPRINT",EDGE,{"derivedFrom":subQ0}),-1.0]])]});}
            var Q22;
            Q22=makeQuery(id+"F7.imprint","IMPRINT",FACE,{"disambiguationData":[TD([[makeQuery(id+"F7.imprint","IMPRINT",EDGE,{"derivedFrom":sQuery(id+"F7.wireOp",EDGE,"E106")}),1.0]])]});
            var Q23;
            Q23=makeQuery(id+"F7.imprint","IMPRINT",FACE,{"disambiguationData":[TD([[makeQuery(id+"F7.imprint","IMPRINT",EDGE,{"derivedFrom":sQuery(id+"F7.wireOp",EDGE,"E108")}),-1.0]])]});
            var Q24;
            Q24=makeQuery(id+"F7.imprint","IMPRINT",FACE,{"disambiguationData":[TD([[makeQuery(id+"F7.imprint","IMPRINT",EDGE,{"derivedFrom":sQuery(id+"F7.wireOp",EDGE,"E114")}),1.0]])]});
            var Q25;
            {var subQ0=sQuery(id+"F7.wireOp",EDGE,"E149");Q25=makeQuery(id+"F7.imprint","IMPRINT",FACE,{"disambiguationData":[TD([[makeQuery(id+"F7.imprint","IMPRINT",EDGE,{"derivedFrom":subQ0}),1.0]])]});}
            var Q26;
            Q26=makeQuery(id+"F7.imprint","IMPRINT",FACE,{"disambiguationData":[TD([[makeQuery(id+"F7.imprint","IMPRINT",EDGE,{"derivedFrom":sQuery(id+"F7.wireOp",EDGE,"E123")}),-1.0]])]});
            var Q27;
            Q27=makeQuery(id+"F7.imprint","IMPRINT",FACE,{"disambiguationData":[TD([[makeQuery(id+"F7.imprint","IMPRINT",EDGE,{"derivedFrom":sQuery(id+"F7.wireOp",EDGE,"E121")}),1.0]])]});
            var Q28;
            {var subQ0=sQuery(id+"F7.wireOp",EDGE,"E120");Q28=makeQuery(id+"F7.imprint","IMPRINT",FACE,{"disambiguationData":[TD([[makeQuery(id+"F7.imprint","IMPRINT",EDGE,{"derivedFrom":subQ0}),-1.0]])]});}
            var Q29;
            Q29=makeQuery(id+"F7.imprint","IMPRINT",FACE,{"disambiguationData":[TD([[makeQuery(id+"F7.imprint","IMPRINT",EDGE,{"derivedFrom":sQuery(id+"F7.wireOp",EDGE,"E136")}),-1.0]])]});
            var Q30;
            Q30=makeQuery(id+"F7.imprint","IMPRINT",FACE,{"disambiguationData":[TD([[makeQuery(id+"F7.imprint","IMPRINT",EDGE,{"derivedFrom":sQuery(id+"F7.wireOp",EDGE,"E143")}),-1.0]])]});
            var Q31;
            Q31=makeQuery(id+"F7.imprint","IMPRINT",FACE,{"disambiguationData":[TD([[makeQuery(id+"F7.imprint","IMPRINT",EDGE,{"derivedFrom":sQuery(id+"F7.wireOp",EDGE,"E180")}),-1.0]])]});
            var Q32;
            {var subQ0=sQuery(id+"F7.wireOp",EDGE,"E135");Q32=makeQuery(id+"F7.imprint","IMPRINT",FACE,{"disambiguationData":[TD([[makeQuery(id+"F7.imprint","IMPRINT",EDGE,{"derivedFrom":subQ0}),1.0]])]});}
            var Q33;
            Q33=makeQuery(id+"F7.imprint","IMPRINT",FACE,{"disambiguationData":[TD([[makeQuery(id+"F7.imprint","IMPRINT",EDGE,{"derivedFrom":sQuery(id+"F7.wireOp",EDGE,"E189")}),-1.0]])]});
            var Q34;
            Q34=makeQuery(id+"F7.imprint","IMPRINT",FACE,{"disambiguationData":[TD([[makeQuery(id+"F7.imprint","IMPRINT",EDGE,{"derivedFrom":sQuery(id+"F7.wireOp",EDGE,"E182")}),-1.0]])]});
            var Q35;
            Q35=makeQuery(id+"F7.imprint","IMPRINT",FACE,{"disambiguationData":[TD([[makeQuery(id+"F7.imprint","IMPRINT",EDGE,{"derivedFrom":sQuery(id+"F7.wireOp",EDGE,"E165")}),-1.0]])]});
            var Q36;
            Q36=makeQuery(id+"F7.imprint","IMPRINT",FACE,{"disambiguationData":[TD([[makeQuery(id+"F7.imprint","IMPRINT",EDGE,{"derivedFrom":sQuery(id+"F7.wireOp",EDGE,"E167")}),1.0]])]});
            var Q37;
            Q37=makeQuery(id+"F7.imprint","IMPRINT",FACE,{"disambiguationData":[TD([[makeQuery(id+"F7.imprint","IMPRINT",EDGE,{"derivedFrom":sQuery(id+"F7.wireOp",EDGE,"E169")}),-1.0]])]});
            var Q38;
            Q38=makeQuery(id+"F7.imprint","IMPRINT",FACE,{"disambiguationData":[TD([[makeQuery(id+"F7.imprint","IMPRINT",EDGE,{"derivedFrom":sQuery(id+"F7.wireOp",EDGE,"E177")}),-1.0]])]});
            var Q39;
            Q39=makeQuery(id+"F7.imprint","IMPRINT",FACE,{"disambiguationData":[TD([[makeQuery(id+"F7.imprint","IMPRINT",EDGE,{"derivedFrom":sQuery(id+"F7.wireOp",EDGE,"E160")}),1.0]])]});
            var Q40;
            Q40=makeQuery(id+"F7.imprint","IMPRINT",FACE,{"disambiguationData":[TD([[makeQuery(id+"F7.imprint","IMPRINT",EDGE,{"derivedFrom":sQuery(id+"F7.wireOp",EDGE,"E161")}),1.0]])]});
            var Q41;
            Q41=makeQuery(id+"F7.imprint","IMPRINT",FACE,{"disambiguationData":[TD([[makeQuery(id+"F7.imprint","IMPRINT",EDGE,{"derivedFrom":sQuery(id+"F7.wireOp",EDGE,"E155")}),-1.0]])]});
            var Q42;
            {var subQ0=sQuery(id+"F7.wireOp",EDGE,"E198");Q42=makeQuery(id+"F7.imprint","IMPRINT",FACE,{"disambiguationData":[TD([[makeQuery(id+"F7.imprint","IMPRINT",EDGE,{"derivedFrom":subQ0}),-1.0]])]});}
            var Q43;
            Q43=makeQuery(id+"F7.imprint","IMPRINT",FACE,{"disambiguationData":[TD([[makeQuery(id+"F7.imprint","IMPRINT",EDGE,{"derivedFrom":sQuery(id+"F7.wireOp",EDGE,"E199")}),1.0]])]});
            var Q44;
            Q44=makeQuery(id+"F7.imprint","IMPRINT",FACE,{"disambiguationData":[TD([[makeQuery(id+"F7.imprint","IMPRINT",EDGE,{"derivedFrom":sQuery(id+"F7.wireOp",EDGE,"E201")}),-1.0]])]});
            var Q45;
            Q45=makeQuery(id+"F7.imprint","IMPRINT",FACE,{"disambiguationData":[TD([[makeQuery(id+"F7.imprint","IMPRINT",EDGE,{"derivedFrom":sQuery(id+"F7.wireOp",EDGE,"E207")}),1.0]])]});
            var Q46;
            Q46=makeQuery(id+"F7.imprint","IMPRINT",FACE,{"disambiguationData":[TD([[makeQuery(id+"F7.imprint","IMPRINT",EDGE,{"derivedFrom":sQuery(id+"F7.wireOp",EDGE,"E220")}),-1.0]])]});
            var Q47;
            Q47=makeQuery(id+"F7.imprint","IMPRINT",FACE,{"disambiguationData":[TD([[makeQuery(id+"F7.imprint","IMPRINT",EDGE,{"derivedFrom":sQuery(id+"F7.wireOp",EDGE,"E206")}),1.0]])]});
            var Q48;
            Q48=makeQuery(id+"F7.imprint","IMPRINT",FACE,{"disambiguationData":[TD([[makeQuery(id+"F7.imprint","IMPRINT",EDGE,{"derivedFrom":sQuery(id+"F7.wireOp",EDGE,"E213")}),-1.0]])]});
            var Q49;
            Q49=makeQuery(id+"F7.imprint","IMPRINT",FACE,{"disambiguationData":[TD([[makeQuery(id+"F7.imprint","IMPRINT",EDGE,{"derivedFrom":sQuery(id+"F7.wireOp",EDGE,"E211")}),1.0]])]});
            var Q50;
            Q50=makeQuery(id+"F7.imprint","IMPRINT",FACE,{"disambiguationData":[TD([[makeQuery(id+"F7.imprint","IMPRINT",EDGE,{"derivedFrom":sQuery(id+"F7.wireOp",EDGE,"E239")}),-1.0]])]});
            var Q51;
            Q51=makeQuery(id+"F7.imprint","IMPRINT",FACE,{"disambiguationData":[TD([[makeQuery(id+"F7.imprint","IMPRINT",EDGE,{"derivedFrom":sQuery(id+"F7.wireOp",EDGE,"E247")}),-1.0]])]});
            var Q52;
            Q52=makeQuery(id+"F7.imprint","IMPRINT",FACE,{"disambiguationData":[TD([[makeQuery(id+"F7.imprint","IMPRINT",EDGE,{"derivedFrom":sQuery(id+"F7.wireOp",EDGE,"E230")}),1.0]])]});
            var Q53;
            Q53=makeQuery(id+"F7.imprint","IMPRINT",FACE,{"disambiguationData":[TD([[makeQuery(id+"F7.imprint","IMPRINT",EDGE,{"derivedFrom":sQuery(id+"F7.wireOp",EDGE,"E227")}),1.0]])]});
            var Q54;
            Q54=makeQuery(id+"F7.imprint","IMPRINT",FACE,{"disambiguationData":[TD([[makeQuery(id+"F7.imprint","IMPRINT",EDGE,{"derivedFrom":sQuery(id+"F7.wireOp",EDGE,"E237")}),1.0]])]});
            var Q55;
            {var subQ0=sQuery(id+"F7.wireOp",EDGE,"E236");Q55=makeQuery(id+"F7.imprint","IMPRINT",FACE,{"disambiguationData":[TD([[makeQuery(id+"F7.imprint","IMPRINT",EDGE,{"derivedFrom":subQ0}),-1.0]])]});}
            var Q56;
            Q56=makeQuery(id+"F7.imprint","IMPRINT",FACE,{"disambiguationData":[TD([[makeQuery(id+"F7.imprint","IMPRINT",EDGE,{"derivedFrom":sQuery(id+"F7.wireOp",EDGE,"E231")}),1.0]])]});
            var Q57;
            Q57=makeQuery(id+"F7.imprint","IMPRINT",FACE,{"disambiguationData":[TD([[makeQuery(id+"F7.imprint","IMPRINT",EDGE,{"derivedFrom":sQuery(id+"F7.wireOp",EDGE,"E131")}),-1.0]])]});
            var Q58;
            Q58=makeQuery(id+"F7.imprint","IMPRINT",FACE,{"disambiguationData":[TD([[makeQuery(id+"F7.imprint","IMPRINT",EDGE,{"derivedFrom":sQuery(id+"F7.wireOp",EDGE,"E153")}),1.0]])]});
            var Q59;
            {var subQ0=sQuery(id+"F7.wireOp",EDGE,"E152");Q59=makeQuery(id+"F7.imprint","IMPRINT",FACE,{"disambiguationData":[TD([[makeQuery(id+"F7.imprint","IMPRINT",EDGE,{"derivedFrom":subQ0}),-1.0]])]});}
            extrude(context, id + "F10", {"entities" : qUnion([Q0, Q1, Q2, Q3, Q4, Q5, Q6, Q7, Q8, Q9, Q10, Q11, Q12, Q13, Q14, Q15, Q16, Q17, Q18, Q19, Q20, Q21, Q22, Q23, Q24, Q25, Q26, Q27, Q28, Q29, Q30, Q31, Q32, Q33, Q34, Q35, Q36, Q37, Q38, Q39, Q40, Q41, Q42, Q43, Q44, Q45, Q46, Q47, Q48, Q49, Q50, Q51, Q52, Q53, Q54, Q55, Q56, Q57, Q58, Q59]), "operationType" : NewBodyOperationType.REMOVE, "oppositeDirection" : true, "depth" : 25.4 * mm});
        }
        {
            var Q0;
            Q0=makeQuery(id+"F6.opExtrude","SWEPT_FACE",FACE,{"disambiguationData":[OSD([sQuery(id+"F5.wireOp",EDGE,"E18.0")])]});
            var sketch = newSketch(context, id + "F11", { "sketchPlane" : qUnion([Q0])});
            skLineSegment(sketch, "E424", {"start": v(-2.86, -87.23) * mm, "end": v(17.14, -107.03) * mm});
            skLineSegment(sketch, "E425", {"start": v(16, -209.27) * mm, "end": v(-4, -189.47) * mm});
            skLineSegment(sketch, "E426", {"start": v(-4, -189.47) * mm, "end": v(16, -180.85) * mm});
            skLineSegment(sketch, "E427", {"start": v(27.78, -184.7) * mm, "end": v(47.78, -176.08) * mm});
            skLineSegment(sketch, "E428", {"start": v(47.78, -176.08) * mm, "end": v(27.78, -156.28) * mm});
            skLineSegment(sketch, "E429", {"start": v(57.24, -160.94) * mm, "end": v(37.24, -141.13) * mm});
            skLineSegment(sketch, "E430", {"start": v(37.24, -141.13) * mm, "end": v(57.24, -132.51) * mm});
            skLineSegment(sketch, "E431", {"start": v(16, -209.27) * mm, "end": v(16, -180.85) * mm});
            skLineSegment(sketch, "E432", {"start": v(27.78, -184.7) * mm, "end": v(27.78, -156.28) * mm});
            skLineSegment(sketch, "E433", {"start": v(57.24, -160.94) * mm, "end": v(57.24, -132.51) * mm});
            skLineSegment(sketch, "E434", {"start": v(29.59, -132.8) * mm, "end": v(9.59, -112.99) * mm});
            skLineSegment(sketch, "E435", {"start": v(9.59, -112.99) * mm, "end": v(29.59, -104.37) * mm});
            skLineSegment(sketch, "E436", {"start": v(29.59, -132.8) * mm, "end": v(29.59, -104.37) * mm});
            skLineSegment(sketch, "E437", {"start": v(52.35, -84.13) * mm, "end": v(72.35, -103.93) * mm});
            skLineSegment(sketch, "E438", {"start": v(52.35, -112.55) * mm, "end": v(72.35, -132.35) * mm});
            skLineSegment(sketch, "E439", {"start": v(45.82, -185.67) * mm, "end": v(65.82, -205.48) * mm});
            skLineSegment(sketch, "E440", {"start": v(65.82, -205.48) * mm, "end": v(45.82, -214.1) * mm});
            skLineSegment(sketch, "E441", {"start": v(52.35, -84.13) * mm, "end": v(52.35, -112.55) * mm});
            skLineSegment(sketch, "E442", {"start": v(72.35, -132.35) * mm, "end": v(72.35, -140.97) * mm});
            skLineSegment(sketch, "E443", {"start": v(45.82, -185.67) * mm, "end": v(45.82, -214.1) * mm});
            skLineSegment(sketch, "E444", {"start": v(72.35, -112.55) * mm, "end": v(92.35, -132.35) * mm});
            skLineSegment(sketch, "E445", {"start": v(92.35, -132.35) * mm, "end": v(72.35, -140.97) * mm});
            skLineSegment(sketch, "E446", {"start": v(75.96, -173) * mm, "end": v(95.96, -192.81) * mm});
            skLineSegment(sketch, "E447", {"start": v(95.96, -192.81) * mm, "end": v(75.96, -201.43) * mm});
            skLineSegment(sketch, "E448", {"start": v(72.35, -103.93) * mm, "end": v(72.35, -112.55) * mm});
            skLineSegment(sketch, "E449", {"start": v(75.96, -173) * mm, "end": v(75.96, -201.43) * mm});
            skLineSegment(sketch, "E450", {"start": v(17.14, -107.03) * mm, "end": v(46.46, -94.82) * mm});
            skLineSegment(sketch, "E451", {"start": v(46.46, -94.82) * mm, "end": v(-2.86, -87.23) * mm});
            skLineSegment(sketch, "E452", {"start": v(212.3, -219.23) * mm, "end": v(192.3, -199.43) * mm});
            skLineSegment(sketch, "E453", {"start": v(192.3, -199.43) * mm, "end": v(212.3, -190.8) * mm});
            skLineSegment(sketch, "E454", {"start": v(192.3, -171) * mm, "end": v(212.3, -162.38) * mm});
            skLineSegment(sketch, "E455", {"start": v(212.3, -162.38) * mm, "end": v(192.3, -142.58) * mm});
            skLineSegment(sketch, "E456", {"start": v(212.3, -133.96) * mm, "end": v(192.3, -114.15) * mm});
            skLineSegment(sketch, "E457", {"start": v(192.3, -114.15) * mm, "end": v(212.3, -105.53) * mm});
            skLineSegment(sketch, "E458", {"start": v(212.3, -219.23) * mm, "end": v(212.3, -190.8) * mm});
            skLineSegment(sketch, "E459", {"start": v(192.3, -171) * mm, "end": v(192.3, -142.58) * mm});
            skLineSegment(sketch, "E460", {"start": v(212.3, -133.96) * mm, "end": v(212.3, -105.53) * mm});
            skLineSegment(sketch, "E461", {"start": v(196.35, -213.66) * mm, "end": v(176.35, -193.86) * mm});
            skLineSegment(sketch, "E462", {"start": v(172.3, -142.58) * mm, "end": v(192.3, -133.96) * mm});
            skLineSegment(sketch, "E463", {"start": v(192.3, -133.96) * mm, "end": v(172.3, -114.15) * mm});
            skLineSegment(sketch, "E464", {"start": v(172.3, -114.15) * mm, "end": v(192.3, -105.53) * mm});
            skLineSegment(sketch, "E465", {"start": v(192.3, -105.53) * mm, "end": v(172.3, -85.73) * mm});
            skLineSegment(sketch, "E466", {"start": v(126.53, -85.97) * mm, "end": v(146.53, -105.77) * mm});
            skLineSegment(sketch, "E467", {"start": v(146.53, -105.77) * mm, "end": v(126.53, -114.4) * mm});
            skLineSegment(sketch, "E468", {"start": v(152.17, -133.52) * mm, "end": v(132.17, -142.14) * mm});
            skLineSegment(sketch, "E469", {"start": v(132.17, -142.14) * mm, "end": v(152.17, -161.94) * mm});
            skLineSegment(sketch, "E470", {"start": v(132.17, -170.56) * mm, "end": v(152.17, -190.37) * mm});
            skLineSegment(sketch, "E471", {"start": v(152.17, -190.37) * mm, "end": v(132.17, -198.99) * mm});
            skLineSegment(sketch, "E472", {"start": v(126.53, -85.97) * mm, "end": v(126.53, -114.4) * mm});
            skLineSegment(sketch, "E473", {"start": v(152.17, -133.52) * mm, "end": v(152.17, -161.94) * mm});
            skLineSegment(sketch, "E474", {"start": v(132.17, -170.56) * mm, "end": v(132.17, -198.99) * mm});
            skLineSegment(sketch, "E475", {"start": v(152.58, -85.7) * mm, "end": v(172.17, -105.1) * mm});
            skLineSegment(sketch, "E476", {"start": v(172.17, -105.1) * mm, "end": v(152.17, -113.72) * mm});
            skLineSegment(sketch, "E477", {"start": v(152.17, -113.72) * mm, "end": v(172.17, -133.52) * mm});
            skLineSegment(sketch, "E478", {"start": v(160.74, -149.36) * mm, "end": v(180.74, -169.17) * mm});
            skLineSegment(sketch, "E479", {"start": v(180.74, -169.17) * mm, "end": v(160.74, -177.79) * mm});
            skLineSegment(sketch, "E480", {"start": v(160.74, -149.36) * mm, "end": v(160.74, -177.79) * mm});
            skLineSegment(sketch, "E481", {"start": v(117.9, -201.64) * mm, "end": v(97.9, -181.83) * mm});
            skLineSegment(sketch, "E482", {"start": v(117.9, -173.21) * mm, "end": v(97.9, -153.41) * mm});
            skLineSegment(sketch, "E483", {"start": v(123.77, -134.63) * mm, "end": v(103.77, -114.83) * mm});
            skLineSegment(sketch, "E484", {"start": v(103.77, -114.83) * mm, "end": v(123.77, -106.2) * mm});
            skLineSegment(sketch, "E485", {"start": v(117.9, -201.64) * mm, "end": v(117.9, -173.21) * mm});
            skLineSegment(sketch, "E486", {"start": v(97.9, -153.41) * mm, "end": v(97.9, -144.79) * mm});
            skLineSegment(sketch, "E487", {"start": v(123.77, -134.63) * mm, "end": v(123.77, -106.2) * mm});
            skLineSegment(sketch, "E488", {"start": v(97.9, -173.21) * mm, "end": v(77.9, -153.41) * mm});
            skLineSegment(sketch, "E489", {"start": v(77.9, -153.41) * mm, "end": v(97.9, -144.79) * mm});
            skLineSegment(sketch, "E490", {"start": v(98.8, -122.45) * mm, "end": v(78.8, -102.65) * mm});
            skLineSegment(sketch, "E491", {"start": v(78.8, -102.65) * mm, "end": v(98.8, -94.03) * mm});
            skLineSegment(sketch, "E492", {"start": v(97.9, -181.83) * mm, "end": v(97.9, -173.21) * mm});
            skLineSegment(sketch, "E493", {"start": v(98.8, -122.45) * mm, "end": v(98.8, -94.03) * mm});
            skLineSegment(sketch, "E494", {"start": v(152.58, -85.7) * mm, "end": v(172.3, -85.73) * mm});
            skLineSegment(sketch, "E495", {"start": v(172.3, -142.58) * mm, "end": v(172.17, -133.52) * mm});
            skLineSegment(sketch, "E496", {"start": v(176.35, -193.86) * mm, "end": v(147.03, -206.07) * mm});
            skLineSegment(sketch, "E497", {"start": v(147.03, -206.07) * mm, "end": v(196.35, -213.66) * mm});
            skLineSegment(sketch, "E498", {"start": v(219.92, -83.7) * mm, "end": v(239.92, -103.5) * mm});
            skLineSegment(sketch, "E499", {"start": v(239.92, -103.5) * mm, "end": v(219.92, -112.12) * mm});
            skLineSegment(sketch, "E500", {"start": v(239.92, -131.93) * mm, "end": v(219.92, -140.55) * mm});
            skLineSegment(sketch, "E501", {"start": v(219.92, -140.55) * mm, "end": v(239.92, -160.35) * mm});
            skLineSegment(sketch, "E502", {"start": v(219.92, -168.97) * mm, "end": v(239.92, -188.78) * mm});
            skLineSegment(sketch, "E503", {"start": v(239.92, -188.78) * mm, "end": v(219.92, -197.4) * mm});
            skLineSegment(sketch, "E504", {"start": v(219.92, -83.7) * mm, "end": v(219.92, -112.12) * mm});
            skLineSegment(sketch, "E505", {"start": v(239.92, -131.93) * mm, "end": v(239.92, -160.35) * mm});
            skLineSegment(sketch, "E506", {"start": v(219.92, -168.97) * mm, "end": v(219.92, -197.4) * mm});
            skLineSegment(sketch, "E507", {"start": v(239.92, -83.7) * mm, "end": v(259.92, -103.5) * mm});
            skLineSegment(sketch, "E508", {"start": v(259.92, -160.35) * mm, "end": v(239.92, -168.97) * mm});
            skLineSegment(sketch, "E509", {"start": v(239.92, -168.97) * mm, "end": v(259.92, -188.78) * mm});
            skLineSegment(sketch, "E510", {"start": v(259.92, -188.78) * mm, "end": v(239.92, -197.4) * mm});
            skLineSegment(sketch, "E511", {"start": v(239.92, -197.4) * mm, "end": v(259.92, -217.2) * mm});
            skLineSegment(sketch, "E512", {"start": v(239.92, -83.7) * mm, "end": v(239.92, -83.71) * mm});
            skLineSegment(sketch, "E513", {"start": v(300.05, -217.64) * mm, "end": v(280.05, -197.84) * mm});
            skLineSegment(sketch, "E514", {"start": v(280.05, -197.84) * mm, "end": v(300.05, -189.21) * mm});
            skLineSegment(sketch, "E515", {"start": v(280.05, -169.41) * mm, "end": v(300.05, -160.79) * mm});
            skLineSegment(sketch, "E516", {"start": v(300.05, -160.79) * mm, "end": v(280.05, -140.99) * mm});
            skLineSegment(sketch, "E517", {"start": v(300.05, -132.36) * mm, "end": v(280.05, -112.56) * mm});
            skLineSegment(sketch, "E518", {"start": v(280.05, -112.56) * mm, "end": v(300.05, -103.94) * mm});
            skLineSegment(sketch, "E519", {"start": v(300.05, -217.64) * mm, "end": v(300.05, -189.21) * mm});
            skLineSegment(sketch, "E520", {"start": v(280.05, -169.41) * mm, "end": v(280.05, -140.99) * mm});
            skLineSegment(sketch, "E521", {"start": v(300.05, -132.36) * mm, "end": v(300.05, -103.94) * mm});
            skLineSegment(sketch, "E522", {"start": v(279.64, -217.23) * mm, "end": v(260.05, -197.84) * mm});
            skLineSegment(sketch, "E523", {"start": v(260.05, -197.84) * mm, "end": v(280.05, -189.21) * mm});
            skLineSegment(sketch, "E524", {"start": v(280.05, -189.21) * mm, "end": v(260.05, -169.41) * mm});
            skLineSegment(sketch, "E525", {"start": v(272.83, -154.47) * mm, "end": v(252.83, -134.66) * mm});
            skLineSegment(sketch, "E526", {"start": v(252.83, -134.66) * mm, "end": v(272.83, -126.04) * mm});
            skLineSegment(sketch, "E527", {"start": v(272.83, -154.47) * mm, "end": v(272.83, -126.04) * mm});
            skLineSegment(sketch, "E528", {"start": v(302.81, -83.7) * mm, "end": v(322.81, -103.5) * mm});
            skLineSegment(sketch, "E529", {"start": v(302.81, -112.12) * mm, "end": v(322.81, -131.93) * mm});
            skLineSegment(sketch, "E530", {"start": v(302.81, -168.97) * mm, "end": v(322.81, -188.78) * mm});
            skLineSegment(sketch, "E531", {"start": v(322.81, -188.78) * mm, "end": v(302.81, -197.4) * mm});
            skLineSegment(sketch, "E532", {"start": v(302.81, -83.7) * mm, "end": v(302.81, -112.12) * mm});
            skLineSegment(sketch, "E533", {"start": v(322.81, -131.93) * mm, "end": v(322.81, -140.55) * mm});
            skLineSegment(sketch, "E534", {"start": v(302.81, -168.97) * mm, "end": v(302.81, -197.4) * mm});
            skLineSegment(sketch, "E535", {"start": v(322.81, -112.12) * mm, "end": v(342.81, -131.93) * mm});
            skLineSegment(sketch, "E536", {"start": v(342.81, -131.93) * mm, "end": v(322.81, -140.55) * mm});
            skLineSegment(sketch, "E537", {"start": v(327.77, -182.96) * mm, "end": v(347.77, -202.76) * mm});
            skLineSegment(sketch, "E538", {"start": v(347.77, -202.76) * mm, "end": v(327.77, -211.38) * mm});
            skLineSegment(sketch, "E539", {"start": v(322.81, -103.5) * mm, "end": v(322.81, -112.12) * mm});
            skLineSegment(sketch, "E540", {"start": v(327.77, -182.96) * mm, "end": v(327.77, -211.38) * mm});
            skLineSegment(sketch, "E541", {"start": v(279.64, -217.23) * mm, "end": v(259.92, -217.2) * mm});
            skLineSegment(sketch, "E542", {"start": v(259.92, -160.35) * mm, "end": v(260.05, -169.41) * mm});
            skLineSegment(sketch, "E543", {"start": v(259.92, -103.5) * mm, "end": v(289.24, -91.3) * mm});
            skLineSegment(sketch, "E544", {"start": v(289.24, -91.3) * mm, "end": v(239.92, -83.7) * mm});
            skLineSegment(sketch, "E545", {"start": v(462.76, -218.8) * mm, "end": v(442.76, -199) * mm});
            skLineSegment(sketch, "E546", {"start": v(442.76, -199) * mm, "end": v(462.76, -190.38) * mm});
            skLineSegment(sketch, "E547", {"start": v(442.76, -170.58) * mm, "end": v(462.76, -161.95) * mm});
            skLineSegment(sketch, "E548", {"start": v(462.76, -161.95) * mm, "end": v(442.76, -142.15) * mm});
            skLineSegment(sketch, "E549", {"start": v(462.76, -133.53) * mm, "end": v(442.76, -113.73) * mm});
            skLineSegment(sketch, "E550", {"start": v(442.76, -113.73) * mm, "end": v(462.76, -105.1) * mm});
            skLineSegment(sketch, "E551", {"start": v(462.76, -218.8) * mm, "end": v(462.76, -190.38) * mm});
            skLineSegment(sketch, "E552", {"start": v(442.76, -170.58) * mm, "end": v(442.76, -142.15) * mm});
            skLineSegment(sketch, "E553", {"start": v(462.76, -133.53) * mm, "end": v(462.76, -105.1) * mm});
            skLineSegment(sketch, "E554", {"start": v(446.81, -213.23) * mm, "end": v(426.81, -193.43) * mm});
            skLineSegment(sketch, "E555", {"start": v(422.76, -142.15) * mm, "end": v(442.76, -133.53) * mm});
            skLineSegment(sketch, "E556", {"start": v(442.76, -133.53) * mm, "end": v(422.76, -113.73) * mm});
            skLineSegment(sketch, "E557", {"start": v(422.76, -113.73) * mm, "end": v(442.76, -105.1) * mm});
            skLineSegment(sketch, "E558", {"start": v(442.76, -105.1) * mm, "end": v(422.76, -85.3) * mm});
            skLineSegment(sketch, "E559", {"start": v(377, -85.54) * mm, "end": v(397, -105.34) * mm});
            skLineSegment(sketch, "E560", {"start": v(397, -105.34) * mm, "end": v(377, -113.97) * mm});
            skLineSegment(sketch, "E561", {"start": v(402.63, -133.1) * mm, "end": v(382.63, -141.71) * mm});
            skLineSegment(sketch, "E562", {"start": v(382.63, -141.71) * mm, "end": v(402.63, -161.52) * mm});
            skLineSegment(sketch, "E563", {"start": v(382.63, -170.14) * mm, "end": v(402.63, -189.94) * mm});
            skLineSegment(sketch, "E564", {"start": v(402.63, -189.94) * mm, "end": v(382.63, -198.56) * mm});
            skLineSegment(sketch, "E565", {"start": v(377, -85.54) * mm, "end": v(377, -113.97) * mm});
            skLineSegment(sketch, "E566", {"start": v(402.63, -133.1) * mm, "end": v(402.63, -161.52) * mm});
            skLineSegment(sketch, "E567", {"start": v(382.63, -170.14) * mm, "end": v(382.63, -198.56) * mm});
            skLineSegment(sketch, "E568", {"start": v(403.04, -85.27) * mm, "end": v(422.63, -104.67) * mm});
            skLineSegment(sketch, "E569", {"start": v(422.63, -104.67) * mm, "end": v(402.63, -113.29) * mm});
            skLineSegment(sketch, "E570", {"start": v(402.63, -113.29) * mm, "end": v(422.63, -133.1) * mm});
            skLineSegment(sketch, "E571", {"start": v(413.46, -156.6) * mm, "end": v(433.46, -176.4) * mm});
            skLineSegment(sketch, "E572", {"start": v(433.46, -176.4) * mm, "end": v(413.46, -185.03) * mm});
            skLineSegment(sketch, "E573", {"start": v(413.46, -156.6) * mm, "end": v(413.46, -185.03) * mm});
            skLineSegment(sketch, "E574", {"start": v(368.37, -201.21) * mm, "end": v(348.37, -181.4) * mm});
            skLineSegment(sketch, "E575", {"start": v(368.37, -172.79) * mm, "end": v(348.37, -152.98) * mm});
            skLineSegment(sketch, "E576", {"start": v(374.23, -134.2) * mm, "end": v(354.23, -114.4) * mm});
            skLineSegment(sketch, "E577", {"start": v(354.23, -114.4) * mm, "end": v(374.23, -105.78) * mm});
            skLineSegment(sketch, "E578", {"start": v(368.37, -201.21) * mm, "end": v(368.37, -172.79) * mm});
            skLineSegment(sketch, "E579", {"start": v(348.37, -152.98) * mm, "end": v(348.37, -144.36) * mm});
            skLineSegment(sketch, "E580", {"start": v(374.23, -134.2) * mm, "end": v(374.23, -105.78) * mm});
            skLineSegment(sketch, "E581", {"start": v(348.37, -172.79) * mm, "end": v(328.37, -152.98) * mm});
            skLineSegment(sketch, "E582", {"start": v(328.37, -152.98) * mm, "end": v(348.37, -144.36) * mm});
            skLineSegment(sketch, "E583", {"start": v(348.37, -120.22) * mm, "end": v(328.37, -100.42) * mm});
            skLineSegment(sketch, "E584", {"start": v(328.37, -100.42) * mm, "end": v(348.37, -91.8) * mm});
            skLineSegment(sketch, "E585", {"start": v(348.37, -181.4) * mm, "end": v(348.37, -172.79) * mm});
            skLineSegment(sketch, "E586", {"start": v(348.37, -120.22) * mm, "end": v(348.37, -91.8) * mm});
            skLineSegment(sketch, "E587", {"start": v(403.04, -85.27) * mm, "end": v(422.76, -85.3) * mm});
            skLineSegment(sketch, "E588", {"start": v(422.76, -142.15) * mm, "end": v(422.63, -133.1) * mm});
            skLineSegment(sketch, "E589", {"start": v(426.81, -193.43) * mm, "end": v(397.5, -205.64) * mm});
            skLineSegment(sketch, "E590", {"start": v(397.5, -205.64) * mm, "end": v(446.81, -213.23) * mm});
            skLineSegment(sketch, "E591", {"start": v(471.26, -83.93) * mm, "end": v(491.26, -103.74) * mm});
            skLineSegment(sketch, "E592", {"start": v(491.26, -103.74) * mm, "end": v(471.26, -112.36) * mm});
            skLineSegment(sketch, "E593", {"start": v(491.26, -132.16) * mm, "end": v(471.26, -140.78) * mm});
            skLineSegment(sketch, "E594", {"start": v(471.26, -140.78) * mm, "end": v(491.26, -160.58) * mm});
            skLineSegment(sketch, "E595", {"start": v(471.26, -169.2) * mm, "end": v(491.26, -189) * mm});
            skLineSegment(sketch, "E596", {"start": v(491.26, -189) * mm, "end": v(471.26, -197.63) * mm});
            skLineSegment(sketch, "E597", {"start": v(471.26, -83.93) * mm, "end": v(471.26, -112.36) * mm});
            skLineSegment(sketch, "E598", {"start": v(491.26, -132.16) * mm, "end": v(491.26, -160.58) * mm});
            skLineSegment(sketch, "E599", {"start": v(471.26, -169.2) * mm, "end": v(471.26, -197.63) * mm});
            skLineSegment(sketch, "E600", {"start": v(487.21, -89.5) * mm, "end": v(507.21, -109.3) * mm});
            skLineSegment(sketch, "E601", {"start": v(511.26, -160.58) * mm, "end": v(491.26, -169.2) * mm});
            skLineSegment(sketch, "E602", {"start": v(491.26, -169.2) * mm, "end": v(511.26, -189) * mm});
            skLineSegment(sketch, "E603", {"start": v(511.26, -189) * mm, "end": v(491.26, -197.63) * mm});
            skLineSegment(sketch, "E604", {"start": v(491.26, -197.63) * mm, "end": v(511.26, -217.43) * mm});
            skLineSegment(sketch, "E605", {"start": v(531.4, -169.64) * mm, "end": v(551.4, -161.02) * mm});
            skLineSegment(sketch, "E606", {"start": v(551.4, -161.02) * mm, "end": v(531.4, -141.22) * mm});
            skLineSegment(sketch, "E607", {"start": v(543.73, -135.3) * mm, "end": v(523.73, -115.5) * mm});
            skLineSegment(sketch, "E608", {"start": v(523.73, -115.5) * mm, "end": v(543.73, -106.88) * mm});
            skLineSegment(sketch, "E609", {"start": v(531.4, -169.64) * mm, "end": v(531.4, -141.22) * mm});
            skLineSegment(sketch, "E610", {"start": v(543.73, -135.3) * mm, "end": v(543.73, -106.88) * mm});
            skLineSegment(sketch, "E611", {"start": v(530.98, -217.46) * mm, "end": v(511.4, -198.07) * mm});
            skLineSegment(sketch, "E612", {"start": v(511.4, -198.07) * mm, "end": v(531.4, -189.45) * mm});
            skLineSegment(sketch, "E613", {"start": v(531.4, -189.45) * mm, "end": v(511.4, -169.64) * mm});
            skLineSegment(sketch, "E614", {"start": v(514.7, -141.17) * mm, "end": v(494.7, -121.37) * mm});
            skLineSegment(sketch, "E615", {"start": v(494.7, -121.37) * mm, "end": v(514.7, -112.74) * mm});
            skLineSegment(sketch, "E616", {"start": v(514.7, -141.17) * mm, "end": v(514.7, -112.74) * mm});
            skLineSegment(sketch, "E617", {"start": v(530.98, -217.46) * mm, "end": v(511.26, -217.43) * mm});
            skLineSegment(sketch, "E618", {"start": v(511.26, -160.58) * mm, "end": v(511.4, -169.64) * mm});
            skLineSegment(sketch, "E619", {"start": v(507.21, -109.3) * mm, "end": v(536.54, -97.1) * mm});
            skLineSegment(sketch, "E620", {"start": v(536.54, -97.1) * mm, "end": v(487.21, -89.5) * mm});
            skLineSegment(sketch, "E621", {"start": v(582.97, -166.23) * mm, "end": v(602.97, -157.6) * mm});
            skLineSegment(sketch, "E622", {"start": v(602.97, -157.6) * mm, "end": v(582.97, -137.8) * mm});
            skLineSegment(sketch, "E623", {"start": v(582.97, -166.23) * mm, "end": v(582.97, -137.8) * mm});
            skLineSegment(sketch, "E624", {"start": v(621.22, -210.03) * mm, "end": v(601.22, -190.23) * mm});
            skLineSegment(sketch, "E625", {"start": v(597.17, -138.95) * mm, "end": v(617.17, -130.33) * mm});
            skLineSegment(sketch, "E626", {"start": v(617.17, -130.33) * mm, "end": v(597.17, -110.53) * mm});
            skLineSegment(sketch, "E627", {"start": v(597.17, -110.53) * mm, "end": v(617.17, -101.9) * mm});
            skLineSegment(sketch, "E628", {"start": v(617.17, -101.9) * mm, "end": v(597.17, -82.1) * mm});
            skLineSegment(sketch, "E629", {"start": v(551.4, -82.34) * mm, "end": v(571.4, -102.14) * mm});
            skLineSegment(sketch, "E630", {"start": v(571.4, -102.14) * mm, "end": v(551.4, -110.77) * mm});
            skLineSegment(sketch, "E631", {"start": v(577.03, -129.9) * mm, "end": v(557.03, -138.51) * mm});
            skLineSegment(sketch, "E632", {"start": v(557.03, -138.51) * mm, "end": v(577.03, -158.32) * mm});
            skLineSegment(sketch, "E633", {"start": v(548.46, -167.84) * mm, "end": v(568.46, -187.64) * mm});
            skLineSegment(sketch, "E634", {"start": v(568.46, -187.64) * mm, "end": v(542.6, -196.26) * mm});
            skLineSegment(sketch, "E635", {"start": v(551.4, -82.34) * mm, "end": v(551.4, -110.77) * mm});
            skLineSegment(sketch, "E636", {"start": v(577.03, -129.9) * mm, "end": v(577.03, -158.32) * mm});
            skLineSegment(sketch, "E637", {"start": v(548.46, -167.84) * mm, "end": v(542.6, -196.26) * mm});
            skLineSegment(sketch, "E638", {"start": v(577.45, -82.07) * mm, "end": v(597.03, -101.47) * mm});
            skLineSegment(sketch, "E639", {"start": v(597.03, -101.47) * mm, "end": v(577.03, -110.09) * mm});
            skLineSegment(sketch, "E640", {"start": v(577.03, -110.09) * mm, "end": v(597.03, -129.9) * mm});
            skLineSegment(sketch, "E641", {"start": v(577.03, -166.94) * mm, "end": v(597.03, -186.74) * mm});
            skLineSegment(sketch, "E642", {"start": v(597.03, -186.74) * mm, "end": v(577.03, -195.36) * mm});
            skLineSegment(sketch, "E643", {"start": v(577.03, -166.94) * mm, "end": v(577.03, -195.36) * mm});
            skLineSegment(sketch, "E644", {"start": v(577.45, -82.07) * mm, "end": v(597.17, -82.1) * mm});
            skLineSegment(sketch, "E645", {"start": v(597.17, -138.95) * mm, "end": v(597.03, -129.9) * mm});
            skLineSegment(sketch, "E646", {"start": v(601.22, -190.23) * mm, "end": v(571.9, -202.44) * mm});
            skLineSegment(sketch, "E647", {"start": v(571.9, -202.44) * mm, "end": v(621.22, -210.03) * mm});
            skLineSegment(sketch, "E648", {"start": v(22.04, -161.7) * mm, "end": v(2.04, -141.89) * mm});
            skLineSegment(sketch, "E649", {"start": v(22.04, -133.27) * mm, "end": v(2.04, -113.47) * mm});
            skLineSegment(sketch, "E650", {"start": v(22.04, -161.7) * mm, "end": v(22.04, -133.27) * mm});
            skLineSegment(sketch, "E651", {"start": v(2.04, -113.47) * mm, "end": v(2.04, -104.84) * mm});
            skLineSegment(sketch, "E652", {"start": v(2.04, -133.27) * mm, "end": v(-7.96, -123.37) * mm});
            skLineSegment(sketch, "E653", {"start": v(2.04, -141.89) * mm, "end": v(2.04, -133.27) * mm});
            skLineSegment(sketch, "E654", {"start": v(2.04, -104.84) * mm, "end": v(-7.96, -123.37) * mm});
            skPoint(sketch, "E655.orphan", {"position": v(-17.96, -113.47) * mm});
            skSolve(sketch);
        }
        {
            var Q0;
            Q0=makeQuery(id+"F6.opExtrude","SWEPT_FACE",FACE,{"disambiguationData":[OSD([sQuery(id+"F5.wireOp",EDGE,"E16.0")])]});
            var sketch = newSketch(context, id + "F12", { "sketchPlane" : qUnion([Q0])});
            skLineSegment(sketch, "E656", {"start": v(0.47, -223.6) * mm, "end": v(20.47, -243.4) * mm});
            skLineSegment(sketch, "E657", {"start": v(19.33, -345.64) * mm, "end": v(-0.67, -325.84) * mm});
            skLineSegment(sketch, "E658", {"start": v(-0.67, -325.84) * mm, "end": v(19.33, -317.22) * mm});
            skLineSegment(sketch, "E659", {"start": v(31.1, -321.07) * mm, "end": v(51.1, -312.45) * mm});
            skLineSegment(sketch, "E660", {"start": v(51.1, -312.45) * mm, "end": v(31.1, -292.65) * mm});
            skLineSegment(sketch, "E661", {"start": v(60.57, -297.3) * mm, "end": v(40.57, -277.5) * mm});
            skLineSegment(sketch, "E662", {"start": v(40.57, -277.5) * mm, "end": v(60.57, -268.88) * mm});
            skLineSegment(sketch, "E663", {"start": v(19.33, -345.64) * mm, "end": v(19.33, -317.22) * mm});
            skLineSegment(sketch, "E664", {"start": v(31.1, -321.07) * mm, "end": v(31.1, -292.65) * mm});
            skLineSegment(sketch, "E665", {"start": v(60.57, -297.3) * mm, "end": v(60.57, -268.88) * mm});
            skLineSegment(sketch, "E666", {"start": v(32.92, -269.16) * mm, "end": v(12.92, -249.36) * mm});
            skLineSegment(sketch, "E667", {"start": v(12.92, -249.36) * mm, "end": v(32.92, -240.74) * mm});
            skLineSegment(sketch, "E668", {"start": v(32.92, -269.16) * mm, "end": v(32.92, -240.74) * mm});
            skLineSegment(sketch, "E669", {"start": v(55.68, -220.5) * mm, "end": v(75.68, -240.3) * mm});
            skLineSegment(sketch, "E670", {"start": v(55.68, -248.92) * mm, "end": v(75.68, -268.72) * mm});
            skLineSegment(sketch, "E671", {"start": v(49.15, -322.04) * mm, "end": v(69.15, -341.85) * mm});
            skLineSegment(sketch, "E672", {"start": v(69.15, -341.85) * mm, "end": v(49.15, -350.47) * mm});
            skLineSegment(sketch, "E673", {"start": v(55.68, -220.5) * mm, "end": v(55.68, -248.92) * mm});
            skLineSegment(sketch, "E674", {"start": v(75.68, -268.72) * mm, "end": v(75.68, -277.35) * mm});
            skLineSegment(sketch, "E675", {"start": v(49.15, -322.04) * mm, "end": v(49.15, -350.47) * mm});
            skLineSegment(sketch, "E676", {"start": v(75.68, -248.92) * mm, "end": v(95.68, -268.72) * mm});
            skLineSegment(sketch, "E677", {"start": v(95.68, -268.72) * mm, "end": v(75.68, -277.35) * mm});
            skLineSegment(sketch, "E678", {"start": v(79.28, -309.38) * mm, "end": v(99.28, -329.18) * mm});
            skLineSegment(sketch, "E679", {"start": v(99.28, -329.18) * mm, "end": v(79.28, -337.8) * mm});
            skLineSegment(sketch, "E680", {"start": v(75.68, -240.3) * mm, "end": v(75.68, -248.92) * mm});
            skLineSegment(sketch, "E681", {"start": v(79.28, -309.38) * mm, "end": v(79.28, -337.8) * mm});
            skLineSegment(sketch, "E682", {"start": v(20.47, -243.4) * mm, "end": v(49.8, -231.2) * mm});
            skLineSegment(sketch, "E683", {"start": v(49.8, -231.2) * mm, "end": v(0.47, -223.6) * mm});
            skLineSegment(sketch, "E684", {"start": v(215.63, -355.6) * mm, "end": v(195.63, -335.8) * mm});
            skLineSegment(sketch, "E685", {"start": v(195.63, -335.8) * mm, "end": v(215.63, -327.18) * mm});
            skLineSegment(sketch, "E686", {"start": v(195.63, -307.37) * mm, "end": v(215.63, -298.75) * mm});
            skLineSegment(sketch, "E687", {"start": v(215.63, -298.75) * mm, "end": v(195.63, -278.95) * mm});
            skLineSegment(sketch, "E688", {"start": v(215.63, -270.33) * mm, "end": v(195.63, -250.52) * mm});
            skLineSegment(sketch, "E689", {"start": v(195.63, -250.52) * mm, "end": v(215.63, -241.9) * mm});
            skLineSegment(sketch, "E690", {"start": v(215.63, -355.6) * mm, "end": v(215.63, -327.18) * mm});
            skLineSegment(sketch, "E691", {"start": v(195.63, -307.37) * mm, "end": v(195.63, -278.95) * mm});
            skLineSegment(sketch, "E692", {"start": v(215.63, -270.33) * mm, "end": v(215.63, -241.9) * mm});
            skLineSegment(sketch, "E693", {"start": v(199.68, -350.03) * mm, "end": v(179.68, -330.23) * mm});
            skLineSegment(sketch, "E694", {"start": v(175.63, -278.95) * mm, "end": v(195.63, -270.33) * mm});
            skLineSegment(sketch, "E695", {"start": v(195.63, -270.33) * mm, "end": v(175.63, -250.52) * mm});
            skLineSegment(sketch, "E696", {"start": v(175.63, -250.52) * mm, "end": v(195.63, -241.9) * mm});
            skLineSegment(sketch, "E697", {"start": v(195.63, -241.9) * mm, "end": v(175.63, -222.1) * mm});
            skLineSegment(sketch, "E698", {"start": v(129.86, -222.34) * mm, "end": v(149.86, -242.14) * mm});
            skLineSegment(sketch, "E699", {"start": v(149.86, -242.14) * mm, "end": v(129.86, -250.76) * mm});
            skLineSegment(sketch, "E700", {"start": v(155.5, -269.89) * mm, "end": v(135.5, -278.51) * mm});
            skLineSegment(sketch, "E701", {"start": v(135.5, -278.51) * mm, "end": v(155.5, -298.31) * mm});
            skLineSegment(sketch, "E702", {"start": v(135.5, -306.94) * mm, "end": v(155.5, -326.74) * mm});
            skLineSegment(sketch, "E703", {"start": v(155.5, -326.74) * mm, "end": v(135.5, -335.36) * mm});
            skLineSegment(sketch, "E704", {"start": v(129.86, -222.34) * mm, "end": v(129.86, -250.76) * mm});
            skLineSegment(sketch, "E705", {"start": v(155.5, -269.89) * mm, "end": v(155.5, -298.31) * mm});
            skLineSegment(sketch, "E706", {"start": v(135.5, -306.94) * mm, "end": v(135.5, -335.36) * mm});
            skLineSegment(sketch, "E707", {"start": v(155.9, -222.07) * mm, "end": v(175.5, -241.46) * mm});
            skLineSegment(sketch, "E708", {"start": v(175.5, -241.46) * mm, "end": v(155.5, -250.09) * mm});
            skLineSegment(sketch, "E709", {"start": v(155.5, -250.09) * mm, "end": v(175.5, -269.89) * mm});
            skLineSegment(sketch, "E710", {"start": v(164.07, -285.73) * mm, "end": v(184.07, -305.54) * mm});
            skLineSegment(sketch, "E711", {"start": v(184.07, -305.54) * mm, "end": v(164.07, -314.16) * mm});
            skLineSegment(sketch, "E712", {"start": v(164.07, -285.73) * mm, "end": v(164.07, -314.16) * mm});
            skLineSegment(sketch, "E713", {"start": v(121.23, -338) * mm, "end": v(101.23, -318.2) * mm});
            skLineSegment(sketch, "E714", {"start": v(121.23, -309.58) * mm, "end": v(101.23, -289.78) * mm});
            skLineSegment(sketch, "E715", {"start": v(127.1, -271) * mm, "end": v(107.1, -251.2) * mm});
            skLineSegment(sketch, "E716", {"start": v(107.1, -251.2) * mm, "end": v(127.1, -242.58) * mm});
            skLineSegment(sketch, "E717", {"start": v(121.23, -338) * mm, "end": v(121.23, -309.58) * mm});
            skLineSegment(sketch, "E718", {"start": v(101.23, -289.78) * mm, "end": v(101.23, -281.16) * mm});
            skLineSegment(sketch, "E719", {"start": v(127.1, -271) * mm, "end": v(127.1, -242.58) * mm});
            skLineSegment(sketch, "E720", {"start": v(101.23, -309.58) * mm, "end": v(81.23, -289.78) * mm});
            skLineSegment(sketch, "E721", {"start": v(81.23, -289.78) * mm, "end": v(101.23, -281.16) * mm});
            skLineSegment(sketch, "E722", {"start": v(102.14, -258.82) * mm, "end": v(82.14, -239.02) * mm});
            skLineSegment(sketch, "E723", {"start": v(82.14, -239.02) * mm, "end": v(102.14, -230.4) * mm});
            skLineSegment(sketch, "E724", {"start": v(101.23, -318.2) * mm, "end": v(101.23, -309.58) * mm});
            skLineSegment(sketch, "E725", {"start": v(102.14, -258.82) * mm, "end": v(102.14, -230.4) * mm});
            skLineSegment(sketch, "E726", {"start": v(155.9, -222.07) * mm, "end": v(175.63, -222.1) * mm});
            skLineSegment(sketch, "E727", {"start": v(175.63, -278.95) * mm, "end": v(175.5, -269.89) * mm});
            skLineSegment(sketch, "E728", {"start": v(179.68, -330.23) * mm, "end": v(150.36, -342.44) * mm});
            skLineSegment(sketch, "E729", {"start": v(150.36, -342.44) * mm, "end": v(199.68, -350.03) * mm});
            skLineSegment(sketch, "E730", {"start": v(223.25, -220.07) * mm, "end": v(243.25, -239.87) * mm});
            skLineSegment(sketch, "E731", {"start": v(243.25, -239.87) * mm, "end": v(223.25, -248.5) * mm});
            skLineSegment(sketch, "E732", {"start": v(243.25, -268.3) * mm, "end": v(223.25, -276.92) * mm});
            skLineSegment(sketch, "E733", {"start": v(223.25, -276.92) * mm, "end": v(243.25, -296.72) * mm});
            skLineSegment(sketch, "E734", {"start": v(223.25, -305.34) * mm, "end": v(243.25, -325.15) * mm});
            skLineSegment(sketch, "E735", {"start": v(243.25, -325.15) * mm, "end": v(223.25, -333.77) * mm});
            skLineSegment(sketch, "E736", {"start": v(223.25, -220.07) * mm, "end": v(223.25, -248.5) * mm});
            skLineSegment(sketch, "E737", {"start": v(243.25, -268.3) * mm, "end": v(243.25, -296.72) * mm});
            skLineSegment(sketch, "E738", {"start": v(223.25, -305.34) * mm, "end": v(223.25, -333.77) * mm});
            skLineSegment(sketch, "E739", {"start": v(243.25, -220.07) * mm, "end": v(263.25, -239.87) * mm});
            skLineSegment(sketch, "E740", {"start": v(263.25, -296.72) * mm, "end": v(243.25, -305.34) * mm});
            skLineSegment(sketch, "E741", {"start": v(243.25, -305.34) * mm, "end": v(263.25, -325.15) * mm});
            skLineSegment(sketch, "E742", {"start": v(263.25, -325.15) * mm, "end": v(243.25, -333.77) * mm});
            skLineSegment(sketch, "E743", {"start": v(243.25, -333.77) * mm, "end": v(263.25, -353.57) * mm});
            skLineSegment(sketch, "E744", {"start": v(243.25, -220.07) * mm, "end": v(243.25, -220.08) * mm});
            skLineSegment(sketch, "E745", {"start": v(303.38, -354) * mm, "end": v(283.38, -334.2) * mm});
            skLineSegment(sketch, "E746", {"start": v(283.38, -334.2) * mm, "end": v(303.38, -325.58) * mm});
            skLineSegment(sketch, "E747", {"start": v(283.38, -305.78) * mm, "end": v(303.38, -297.16) * mm});
            skLineSegment(sketch, "E748", {"start": v(303.38, -297.16) * mm, "end": v(283.38, -277.36) * mm});
            skLineSegment(sketch, "E749", {"start": v(303.38, -268.74) * mm, "end": v(283.38, -248.93) * mm});
            skLineSegment(sketch, "E750", {"start": v(283.38, -248.93) * mm, "end": v(303.38, -240.31) * mm});
            skLineSegment(sketch, "E751", {"start": v(303.38, -354) * mm, "end": v(303.38, -325.58) * mm});
            skLineSegment(sketch, "E752", {"start": v(283.38, -305.78) * mm, "end": v(283.38, -277.36) * mm});
            skLineSegment(sketch, "E753", {"start": v(303.38, -268.74) * mm, "end": v(303.38, -240.31) * mm});
            skLineSegment(sketch, "E754", {"start": v(282.97, -353.6) * mm, "end": v(263.38, -334.2) * mm});
            skLineSegment(sketch, "E755", {"start": v(263.38, -334.2) * mm, "end": v(283.38, -325.58) * mm});
            skLineSegment(sketch, "E756", {"start": v(283.38, -325.58) * mm, "end": v(263.38, -305.78) * mm});
            skLineSegment(sketch, "E757", {"start": v(276.16, -290.84) * mm, "end": v(256.16, -271.03) * mm});
            skLineSegment(sketch, "E758", {"start": v(256.16, -271.03) * mm, "end": v(276.16, -262.41) * mm});
            skLineSegment(sketch, "E759", {"start": v(276.16, -290.84) * mm, "end": v(276.16, -262.41) * mm});
            skLineSegment(sketch, "E760", {"start": v(306.14, -220.07) * mm, "end": v(326.14, -239.87) * mm});
            skLineSegment(sketch, "E761", {"start": v(306.14, -248.5) * mm, "end": v(326.14, -268.3) * mm});
            skLineSegment(sketch, "E762", {"start": v(306.14, -305.34) * mm, "end": v(326.14, -325.15) * mm});
            skLineSegment(sketch, "E763", {"start": v(326.14, -325.15) * mm, "end": v(306.14, -333.77) * mm});
            skLineSegment(sketch, "E764", {"start": v(306.14, -220.07) * mm, "end": v(306.14, -248.5) * mm});
            skLineSegment(sketch, "E765", {"start": v(326.14, -268.3) * mm, "end": v(326.14, -276.92) * mm});
            skLineSegment(sketch, "E766", {"start": v(306.14, -305.34) * mm, "end": v(306.14, -333.77) * mm});
            skLineSegment(sketch, "E767", {"start": v(326.14, -248.5) * mm, "end": v(346.14, -268.3) * mm});
            skLineSegment(sketch, "E768", {"start": v(346.14, -268.3) * mm, "end": v(326.14, -276.92) * mm});
            skLineSegment(sketch, "E769", {"start": v(331.1, -319.33) * mm, "end": v(351.1, -339.13) * mm});
            skLineSegment(sketch, "E770", {"start": v(351.1, -339.13) * mm, "end": v(331.1, -347.75) * mm});
            skLineSegment(sketch, "E771", {"start": v(326.14, -239.87) * mm, "end": v(326.14, -248.5) * mm});
            skLineSegment(sketch, "E772", {"start": v(331.1, -319.33) * mm, "end": v(331.1, -347.75) * mm});
            skLineSegment(sketch, "E773", {"start": v(282.97, -353.6) * mm, "end": v(263.25, -353.57) * mm});
            skLineSegment(sketch, "E774", {"start": v(263.25, -296.72) * mm, "end": v(263.38, -305.78) * mm});
            skLineSegment(sketch, "E775", {"start": v(263.25, -239.87) * mm, "end": v(292.57, -227.66) * mm});
            skLineSegment(sketch, "E776", {"start": v(292.57, -227.66) * mm, "end": v(243.25, -220.07) * mm});
            skLineSegment(sketch, "E777", {"start": v(466.1, -355.17) * mm, "end": v(446.1, -335.37) * mm});
            skLineSegment(sketch, "E778", {"start": v(446.1, -335.37) * mm, "end": v(466.1, -326.75) * mm});
            skLineSegment(sketch, "E779", {"start": v(446.1, -306.95) * mm, "end": v(466.1, -298.32) * mm});
            skLineSegment(sketch, "E780", {"start": v(466.1, -298.32) * mm, "end": v(446.1, -278.52) * mm});
            skLineSegment(sketch, "E781", {"start": v(466.1, -269.9) * mm, "end": v(446.1, -250.1) * mm});
            skLineSegment(sketch, "E782", {"start": v(446.1, -250.1) * mm, "end": v(466.1, -241.48) * mm});
            skLineSegment(sketch, "E783", {"start": v(466.1, -355.17) * mm, "end": v(466.1, -326.75) * mm});
            skLineSegment(sketch, "E784", {"start": v(446.1, -306.95) * mm, "end": v(446.1, -278.52) * mm});
            skLineSegment(sketch, "E785", {"start": v(466.1, -269.9) * mm, "end": v(466.1, -241.48) * mm});
            skLineSegment(sketch, "E786", {"start": v(450.14, -349.6) * mm, "end": v(430.14, -329.8) * mm});
            skLineSegment(sketch, "E787", {"start": v(426.1, -278.52) * mm, "end": v(446.1, -269.9) * mm});
            skLineSegment(sketch, "E788", {"start": v(446.1, -269.9) * mm, "end": v(426.1, -250.1) * mm});
            skLineSegment(sketch, "E789", {"start": v(426.1, -250.1) * mm, "end": v(446.1, -241.48) * mm});
            skLineSegment(sketch, "E790", {"start": v(446.1, -241.48) * mm, "end": v(426.1, -221.67) * mm});
            skLineSegment(sketch, "E791", {"start": v(380.32, -221.91) * mm, "end": v(400.32, -241.71) * mm});
            skLineSegment(sketch, "E792", {"start": v(400.32, -241.71) * mm, "end": v(380.32, -250.34) * mm});
            skLineSegment(sketch, "E793", {"start": v(405.96, -269.46) * mm, "end": v(385.96, -278.08) * mm});
            skLineSegment(sketch, "E794", {"start": v(385.96, -278.08) * mm, "end": v(405.96, -297.89) * mm});
            skLineSegment(sketch, "E795", {"start": v(385.96, -306.5) * mm, "end": v(405.96, -326.31) * mm});
            skLineSegment(sketch, "E796", {"start": v(405.96, -326.31) * mm, "end": v(385.96, -334.93) * mm});
            skLineSegment(sketch, "E797", {"start": v(380.32, -221.91) * mm, "end": v(380.32, -250.34) * mm});
            skLineSegment(sketch, "E798", {"start": v(405.96, -269.46) * mm, "end": v(405.96, -297.89) * mm});
            skLineSegment(sketch, "E799", {"start": v(385.96, -306.5) * mm, "end": v(385.96, -334.93) * mm});
            skLineSegment(sketch, "E800", {"start": v(406.37, -221.64) * mm, "end": v(425.96, -241.04) * mm});
            skLineSegment(sketch, "E801", {"start": v(425.96, -241.04) * mm, "end": v(405.96, -249.66) * mm});
            skLineSegment(sketch, "E802", {"start": v(405.96, -249.66) * mm, "end": v(425.96, -269.46) * mm});
            skLineSegment(sketch, "E803", {"start": v(416.79, -292.98) * mm, "end": v(436.79, -312.78) * mm});
            skLineSegment(sketch, "E804", {"start": v(436.79, -312.78) * mm, "end": v(416.79, -321.4) * mm});
            skLineSegment(sketch, "E805", {"start": v(416.79, -292.98) * mm, "end": v(416.79, -321.4) * mm});
            skLineSegment(sketch, "E806", {"start": v(371.7, -337.58) * mm, "end": v(351.7, -317.78) * mm});
            skLineSegment(sketch, "E807", {"start": v(371.7, -309.16) * mm, "end": v(351.7, -289.35) * mm});
            skLineSegment(sketch, "E808", {"start": v(377.56, -270.58) * mm, "end": v(357.56, -250.77) * mm});
            skLineSegment(sketch, "E809", {"start": v(357.56, -250.77) * mm, "end": v(377.56, -242.15) * mm});
            skLineSegment(sketch, "E810", {"start": v(371.7, -337.58) * mm, "end": v(371.7, -309.16) * mm});
            skLineSegment(sketch, "E811", {"start": v(351.7, -289.35) * mm, "end": v(351.7, -280.73) * mm});
            skLineSegment(sketch, "E812", {"start": v(377.56, -270.58) * mm, "end": v(377.56, -242.15) * mm});
            skLineSegment(sketch, "E813", {"start": v(351.7, -309.16) * mm, "end": v(331.7, -289.35) * mm});
            skLineSegment(sketch, "E814", {"start": v(331.7, -289.35) * mm, "end": v(351.7, -280.73) * mm});
            skLineSegment(sketch, "E815", {"start": v(351.7, -256.6) * mm, "end": v(331.7, -236.8) * mm});
            skLineSegment(sketch, "E816", {"start": v(331.7, -236.8) * mm, "end": v(351.7, -228.17) * mm});
            skLineSegment(sketch, "E817", {"start": v(351.7, -317.78) * mm, "end": v(351.7, -309.16) * mm});
            skLineSegment(sketch, "E818", {"start": v(351.7, -256.6) * mm, "end": v(351.7, -228.17) * mm});
            skLineSegment(sketch, "E819", {"start": v(406.37, -221.64) * mm, "end": v(426.1, -221.67) * mm});
            skLineSegment(sketch, "E820", {"start": v(426.1, -278.52) * mm, "end": v(425.96, -269.46) * mm});
            skLineSegment(sketch, "E821", {"start": v(430.14, -329.8) * mm, "end": v(400.82, -342.01) * mm});
            skLineSegment(sketch, "E822", {"start": v(400.82, -342.01) * mm, "end": v(450.14, -349.6) * mm});
            skLineSegment(sketch, "E823", {"start": v(474.6, -220.3) * mm, "end": v(494.6, -240.1) * mm});
            skLineSegment(sketch, "E824", {"start": v(494.6, -240.1) * mm, "end": v(474.6, -248.73) * mm});
            skLineSegment(sketch, "E825", {"start": v(494.6, -268.53) * mm, "end": v(474.6, -277.15) * mm});
            skLineSegment(sketch, "E826", {"start": v(474.6, -277.15) * mm, "end": v(494.6, -296.96) * mm});
            skLineSegment(sketch, "E827", {"start": v(474.6, -305.58) * mm, "end": v(494.6, -325.38) * mm});
            skLineSegment(sketch, "E828", {"start": v(494.6, -325.38) * mm, "end": v(474.6, -334) * mm});
            skLineSegment(sketch, "E829", {"start": v(474.6, -220.3) * mm, "end": v(474.6, -248.73) * mm});
            skLineSegment(sketch, "E830", {"start": v(494.6, -268.53) * mm, "end": v(494.6, -296.96) * mm});
            skLineSegment(sketch, "E831", {"start": v(474.6, -305.58) * mm, "end": v(474.6, -334) * mm});
            skLineSegment(sketch, "E832", {"start": v(490.54, -225.87) * mm, "end": v(510.54, -245.68) * mm});
            skLineSegment(sketch, "E833", {"start": v(514.6, -296.96) * mm, "end": v(494.6, -305.58) * mm});
            skLineSegment(sketch, "E834", {"start": v(494.6, -305.58) * mm, "end": v(514.6, -325.38) * mm});
            skLineSegment(sketch, "E835", {"start": v(514.6, -325.38) * mm, "end": v(494.6, -334) * mm});
            skLineSegment(sketch, "E836", {"start": v(494.6, -334) * mm, "end": v(514.6, -353.8) * mm});
            skLineSegment(sketch, "E837", {"start": v(534.72, -306.01) * mm, "end": v(554.72, -297.4) * mm});
            skLineSegment(sketch, "E838", {"start": v(554.72, -297.4) * mm, "end": v(534.72, -277.59) * mm});
            skLineSegment(sketch, "E839", {"start": v(547.06, -271.67) * mm, "end": v(527.06, -251.87) * mm});
            skLineSegment(sketch, "E840", {"start": v(527.06, -251.87) * mm, "end": v(547.06, -243.25) * mm});
            skLineSegment(sketch, "E841", {"start": v(534.72, -306.01) * mm, "end": v(534.72, -277.59) * mm});
            skLineSegment(sketch, "E842", {"start": v(547.06, -271.67) * mm, "end": v(547.06, -243.25) * mm});
            skLineSegment(sketch, "E843", {"start": v(534.31, -353.83) * mm, "end": v(514.72, -334.44) * mm});
            skLineSegment(sketch, "E844", {"start": v(514.72, -334.44) * mm, "end": v(534.72, -325.82) * mm});
            skLineSegment(sketch, "E845", {"start": v(534.72, -325.82) * mm, "end": v(514.72, -306.01) * mm});
            skLineSegment(sketch, "E846", {"start": v(518.03, -277.54) * mm, "end": v(498.03, -257.74) * mm});
            skLineSegment(sketch, "E847", {"start": v(498.03, -257.74) * mm, "end": v(518.03, -249.11) * mm});
            skLineSegment(sketch, "E848", {"start": v(518.03, -277.54) * mm, "end": v(518.03, -249.11) * mm});
            skLineSegment(sketch, "E849", {"start": v(534.31, -353.83) * mm, "end": v(514.6, -353.8) * mm});
            skLineSegment(sketch, "E850", {"start": v(514.6, -296.96) * mm, "end": v(514.72, -306.01) * mm});
            skLineSegment(sketch, "E851", {"start": v(510.54, -245.68) * mm, "end": v(539.86, -233.47) * mm});
            skLineSegment(sketch, "E852", {"start": v(539.86, -233.47) * mm, "end": v(490.54, -225.87) * mm});
            skLineSegment(sketch, "E853", {"start": v(586.3, -302.6) * mm, "end": v(606.3, -293.98) * mm});
            skLineSegment(sketch, "E854", {"start": v(606.3, -293.98) * mm, "end": v(586.3, -274.18) * mm});
            skLineSegment(sketch, "E855", {"start": v(586.3, -302.6) * mm, "end": v(586.3, -274.18) * mm});
            skLineSegment(sketch, "E856", {"start": v(624.55, -346.4) * mm, "end": v(604.55, -326.6) * mm});
            skLineSegment(sketch, "E857", {"start": v(600.5, -275.32) * mm, "end": v(620.5, -266.7) * mm});
            skLineSegment(sketch, "E858", {"start": v(620.5, -266.7) * mm, "end": v(600.5, -246.9) * mm});
            skLineSegment(sketch, "E859", {"start": v(600.5, -246.9) * mm, "end": v(620.5, -238.28) * mm});
            skLineSegment(sketch, "E860", {"start": v(620.5, -238.28) * mm, "end": v(600.5, -218.47) * mm});
            skLineSegment(sketch, "E861", {"start": v(554.72, -218.71) * mm, "end": v(574.72, -238.51) * mm});
            skLineSegment(sketch, "E862", {"start": v(574.72, -238.51) * mm, "end": v(554.72, -247.14) * mm});
            skLineSegment(sketch, "E863", {"start": v(580.36, -266.26) * mm, "end": v(560.36, -274.88) * mm});
            skLineSegment(sketch, "E864", {"start": v(560.36, -274.88) * mm, "end": v(580.36, -294.69) * mm});
            skLineSegment(sketch, "E865", {"start": v(551.8, -304.21) * mm, "end": v(571.8, -324.01) * mm});
            skLineSegment(sketch, "E866", {"start": v(571.8, -324.01) * mm, "end": v(545.93, -332.64) * mm});
            skLineSegment(sketch, "E867", {"start": v(554.72, -218.71) * mm, "end": v(554.72, -247.14) * mm});
            skLineSegment(sketch, "E868", {"start": v(580.36, -266.26) * mm, "end": v(580.36, -294.69) * mm});
            skLineSegment(sketch, "E869", {"start": v(551.8, -304.21) * mm, "end": v(545.93, -332.64) * mm});
            skLineSegment(sketch, "E870", {"start": v(580.78, -218.44) * mm, "end": v(600.36, -237.84) * mm});
            skLineSegment(sketch, "E871", {"start": v(600.36, -237.84) * mm, "end": v(580.36, -246.46) * mm});
            skLineSegment(sketch, "E872", {"start": v(580.36, -246.46) * mm, "end": v(600.36, -266.26) * mm});
            skLineSegment(sketch, "E873", {"start": v(580.36, -303.3) * mm, "end": v(600.36, -323.11) * mm});
            skLineSegment(sketch, "E874", {"start": v(600.36, -323.11) * mm, "end": v(580.36, -331.73) * mm});
            skLineSegment(sketch, "E875", {"start": v(580.36, -303.3) * mm, "end": v(580.36, -331.73) * mm});
            skLineSegment(sketch, "E876", {"start": v(580.78, -218.44) * mm, "end": v(600.5, -218.47) * mm});
            skLineSegment(sketch, "E877", {"start": v(600.5, -275.32) * mm, "end": v(600.36, -266.26) * mm});
            skLineSegment(sketch, "E878", {"start": v(604.55, -326.6) * mm, "end": v(575.22, -338.81) * mm});
            skLineSegment(sketch, "E879", {"start": v(575.22, -338.81) * mm, "end": v(624.55, -346.4) * mm});
            skLineSegment(sketch, "E880", {"start": v(25.37, -298.06) * mm, "end": v(5.37, -278.26) * mm});
            skLineSegment(sketch, "E881", {"start": v(25.37, -269.64) * mm, "end": v(5.37, -249.84) * mm});
            skLineSegment(sketch, "E882", {"start": v(25.37, -298.06) * mm, "end": v(25.37, -269.64) * mm});
            skLineSegment(sketch, "E883", {"start": v(5.37, -249.84) * mm, "end": v(5.37, -241.21) * mm});
            skLineSegment(sketch, "E884", {"start": v(5.37, -269.64) * mm, "end": v(-4.63, -259.74) * mm});
            skLineSegment(sketch, "E885", {"start": v(5.37, -278.26) * mm, "end": v(5.37, -269.64) * mm});
            skLineSegment(sketch, "E886", {"start": v(5.37, -241.21) * mm, "end": v(-4.63, -259.74) * mm});
            skPoint(sketch, "E887.orphan", {"position": v(-14.63, -249.84) * mm});
            skSolve(sketch);
        }
        {
            var Q0;
            Q0=makeQuery(id+"F11.imprint","IMPRINT",FACE,{"disambiguationData":[TD([[makeQuery(id+"F11.imprint","IMPRINT",EDGE,{"derivedFrom":sQuery(id+"F11.wireOp",EDGE,"E424")}),1.0]])]});
            var Q1;
            Q1=makeQuery(id+"F11.imprint","IMPRINT",FACE,{"disambiguationData":[TD([[makeQuery(id+"F11.imprint","IMPRINT",EDGE,{"derivedFrom":sQuery(id+"F11.wireOp",EDGE,"E434")}),-1.0]])]});
            var Q2;
            Q2=makeQuery(id+"F11.imprint","IMPRINT",FACE,{"disambiguationData":[TD([[makeQuery(id+"F11.imprint","IMPRINT",EDGE,{"derivedFrom":sQuery(id+"F11.wireOp",EDGE,"E648")}),-1.0]])]});
            var Q3;
            Q3=makeQuery(id+"F11.imprint","IMPRINT",FACE,{"disambiguationData":[TD([[makeQuery(id+"F11.imprint","IMPRINT",EDGE,{"derivedFrom":sQuery(id+"F11.wireOp",EDGE,"E429")}),-1.0]])]});
            var Q4;
            Q4=makeQuery(id+"F11.imprint","IMPRINT",FACE,{"disambiguationData":[TD([[makeQuery(id+"F11.imprint","IMPRINT",EDGE,{"derivedFrom":sQuery(id+"F11.wireOp",EDGE,"E427")}),1.0]])]});
            var Q5;
            Q5=makeQuery(id+"F11.imprint","IMPRINT",FACE,{"disambiguationData":[TD([[makeQuery(id+"F11.imprint","IMPRINT",EDGE,{"derivedFrom":sQuery(id+"F11.wireOp",EDGE,"E425")}),-1.0]])]});
            var Q6;
            Q6=makeQuery(id+"F11.imprint","IMPRINT",FACE,{"disambiguationData":[TD([[makeQuery(id+"F11.imprint","IMPRINT",EDGE,{"derivedFrom":sQuery(id+"F11.wireOp",EDGE,"E439")}),-1.0]])]});
            var Q7;
            Q7=makeQuery(id+"F11.imprint","IMPRINT",FACE,{"disambiguationData":[TD([[makeQuery(id+"F11.imprint","IMPRINT",EDGE,{"derivedFrom":sQuery(id+"F11.wireOp",EDGE,"E446")}),-1.0]])]});
            var Q8;
            Q8=makeQuery(id+"F11.imprint","IMPRINT",FACE,{"disambiguationData":[TD([[makeQuery(id+"F11.imprint","IMPRINT",EDGE,{"derivedFrom":sQuery(id+"F11.wireOp",EDGE,"E481")}),-1.0]])]});
            var Q9;
            Q9=makeQuery(id+"F11.imprint","IMPRINT",FACE,{"disambiguationData":[TD([[makeQuery(id+"F11.imprint","IMPRINT",EDGE,{"derivedFrom":sQuery(id+"F11.wireOp",EDGE,"E490")}),-1.0]])]});
            var Q10;
            Q10=makeQuery(id+"F11.imprint","IMPRINT",FACE,{"disambiguationData":[TD([[makeQuery(id+"F11.imprint","IMPRINT",EDGE,{"derivedFrom":sQuery(id+"F11.wireOp",EDGE,"E483")}),-1.0]])]});
            var Q11;
            Q11=makeQuery(id+"F11.imprint","IMPRINT",FACE,{"disambiguationData":[TD([[makeQuery(id+"F11.imprint","IMPRINT",EDGE,{"derivedFrom":sQuery(id+"F11.wireOp",EDGE,"E466")}),-1.0]])]});
            var Q12;
            Q12=makeQuery(id+"F11.imprint","IMPRINT",FACE,{"disambiguationData":[TD([[makeQuery(id+"F11.imprint","IMPRINT",EDGE,{"derivedFrom":sQuery(id+"F11.wireOp",EDGE,"E468")}),1.0]])]});
            var Q13;
            Q13=makeQuery(id+"F11.imprint","IMPRINT",FACE,{"disambiguationData":[TD([[makeQuery(id+"F11.imprint","IMPRINT",EDGE,{"derivedFrom":sQuery(id+"F11.wireOp",EDGE,"E470")}),-1.0]])]});
            var Q14;
            Q14=makeQuery(id+"F11.imprint","IMPRINT",FACE,{"disambiguationData":[TD([[makeQuery(id+"F11.imprint","IMPRINT",EDGE,{"derivedFrom":sQuery(id+"F11.wireOp",EDGE,"E478")}),-1.0]])]});
            var Q15;
            Q15=makeQuery(id+"F11.imprint","IMPRINT",FACE,{"disambiguationData":[TD([[makeQuery(id+"F11.imprint","IMPRINT",EDGE,{"derivedFrom":sQuery(id+"F11.wireOp",EDGE,"E461")}),1.0]])]});
            var Q16;
            {var subQ0=sQuery(id+"F11.wireOp",EDGE,"E453");Q16=makeQuery(id+"F11.imprint","IMPRINT",FACE,{"disambiguationData":[TD([[makeQuery(id+"F11.imprint","IMPRINT",EDGE,{"derivedFrom":subQ0}),-1.0]])]});}
            var Q17;
            Q17=makeQuery(id+"F11.imprint","IMPRINT",FACE,{"disambiguationData":[TD([[makeQuery(id+"F11.imprint","IMPRINT",EDGE,{"derivedFrom":sQuery(id+"F11.wireOp",EDGE,"E454")}),1.0]])]});
            var Q18;
            Q18=makeQuery(id+"F11.imprint","IMPRINT",FACE,{"disambiguationData":[TD([[makeQuery(id+"F11.imprint","IMPRINT",EDGE,{"derivedFrom":sQuery(id+"F11.wireOp",EDGE,"E462")}),1.0]])]});
            var Q19;
            Q19=makeQuery(id+"F11.imprint","IMPRINT",FACE,{"disambiguationData":[TD([[makeQuery(id+"F11.imprint","IMPRINT",EDGE,{"derivedFrom":sQuery(id+"F11.wireOp",EDGE,"E456")}),-1.0]])]});
            var Q20;
            Q20=makeQuery(id+"F11.imprint","IMPRINT",FACE,{"disambiguationData":[TD([[makeQuery(id+"F11.imprint","IMPRINT",EDGE,{"derivedFrom":sQuery(id+"F11.wireOp",EDGE,"E498")}),-1.0]])]});
            var Q21;
            Q21=makeQuery(id+"F11.imprint","IMPRINT",FACE,{"disambiguationData":[TD([[makeQuery(id+"F11.imprint","IMPRINT",EDGE,{"derivedFrom":sQuery(id+"F11.wireOp",EDGE,"E500")}),1.0]])]});
            var Q22;
            Q22=makeQuery(id+"F11.imprint","IMPRINT",FACE,{"disambiguationData":[TD([[makeQuery(id+"F11.imprint","IMPRINT",EDGE,{"derivedFrom":sQuery(id+"F11.wireOp",EDGE,"E502")}),-1.0]])]});
            var Q23;
            Q23=makeQuery(id+"F11.imprint","IMPRINT",FACE,{"disambiguationData":[TD([[makeQuery(id+"F11.imprint","IMPRINT",EDGE,{"derivedFrom":sQuery(id+"F11.wireOp",EDGE,"E508")}),1.0]])]});
            var Q24;
            Q24=makeQuery(id+"F11.imprint","IMPRINT",FACE,{"disambiguationData":[TD([[makeQuery(id+"F11.imprint","IMPRINT",EDGE,{"derivedFrom":sQuery(id+"F11.wireOp",EDGE,"E525")}),-1.0]])]});
            var Q25;
            Q25=makeQuery(id+"F11.imprint","IMPRINT",FACE,{"disambiguationData":[TD([[makeQuery(id+"F11.imprint","IMPRINT",EDGE,{"derivedFrom":sQuery(id+"F11.wireOp",EDGE,"E515")}),1.0]])]});
            var Q26;
            Q26=makeQuery(id+"F11.imprint","IMPRINT",FACE,{"disambiguationData":[TD([[makeQuery(id+"F11.imprint","IMPRINT",EDGE,{"derivedFrom":sQuery(id+"F11.wireOp",EDGE,"E517")}),-1.0]])]});
            var Q27;
            Q27=makeQuery(id+"F11.imprint","IMPRINT",FACE,{"disambiguationData":[TD([[makeQuery(id+"F11.imprint","IMPRINT",EDGE,{"derivedFrom":sQuery(id+"F11.wireOp",EDGE,"E507")}),1.0]])]});
            var Q28;
            Q28=makeQuery(id+"F11.imprint","IMPRINT",FACE,{"disambiguationData":[TD([[makeQuery(id+"F11.imprint","IMPRINT",EDGE,{"derivedFrom":sQuery(id+"F11.wireOp",EDGE,"E528")}),-1.0]])]});
            var Q29;
            Q29=makeQuery(id+"F11.imprint","IMPRINT",FACE,{"disambiguationData":[TD([[makeQuery(id+"F11.imprint","IMPRINT",EDGE,{"derivedFrom":sQuery(id+"F11.wireOp",EDGE,"E583")}),-1.0]])]});
            var Q30;
            Q30=makeQuery(id+"F11.imprint","IMPRINT",FACE,{"disambiguationData":[TD([[makeQuery(id+"F11.imprint","IMPRINT",EDGE,{"derivedFrom":sQuery(id+"F11.wireOp",EDGE,"E576")}),-1.0]])]});
            var Q31;
            Q31=makeQuery(id+"F11.imprint","IMPRINT",FACE,{"disambiguationData":[TD([[makeQuery(id+"F11.imprint","IMPRINT",EDGE,{"derivedFrom":sQuery(id+"F11.wireOp",EDGE,"E574")}),-1.0]])]});
            var Q32;
            Q32=makeQuery(id+"F11.imprint","IMPRINT",FACE,{"disambiguationData":[TD([[makeQuery(id+"F11.imprint","IMPRINT",EDGE,{"derivedFrom":sQuery(id+"F11.wireOp",EDGE,"E537")}),-1.0]])]});
            var Q33;
            Q33=makeQuery(id+"F11.imprint","IMPRINT",FACE,{"disambiguationData":[TD([[makeQuery(id+"F11.imprint","IMPRINT",EDGE,{"derivedFrom":sQuery(id+"F11.wireOp",EDGE,"E530")}),-1.0]])]});
            var Q34;
            Q34=makeQuery(id+"F11.imprint","IMPRINT",FACE,{"disambiguationData":[TD([[makeQuery(id+"F11.imprint","IMPRINT",EDGE,{"derivedFrom":sQuery(id+"F11.wireOp",EDGE,"E513")}),-1.0]])]});
            var Q35;
            Q35=makeQuery(id+"F11.imprint","IMPRINT",FACE,{"disambiguationData":[TD([[makeQuery(id+"F11.imprint","IMPRINT",EDGE,{"derivedFrom":sQuery(id+"F11.wireOp",EDGE,"E563")}),-1.0]])]});
            var Q36;
            Q36=makeQuery(id+"F11.imprint","IMPRINT",FACE,{"disambiguationData":[TD([[makeQuery(id+"F11.imprint","IMPRINT",EDGE,{"derivedFrom":sQuery(id+"F11.wireOp",EDGE,"E554")}),1.0]])]});
            var Q37;
            {var subQ0=sQuery(id+"F11.wireOp",EDGE,"E546");Q37=makeQuery(id+"F11.imprint","IMPRINT",FACE,{"disambiguationData":[TD([[makeQuery(id+"F11.imprint","IMPRINT",EDGE,{"derivedFrom":subQ0}),-1.0]])]});}
            var Q38;
            Q38=makeQuery(id+"F11.imprint","IMPRINT",FACE,{"disambiguationData":[TD([[makeQuery(id+"F11.imprint","IMPRINT",EDGE,{"derivedFrom":sQuery(id+"F11.wireOp",EDGE,"E571")}),-1.0]])]});
            var Q39;
            Q39=makeQuery(id+"F11.imprint","IMPRINT",FACE,{"disambiguationData":[TD([[makeQuery(id+"F11.imprint","IMPRINT",EDGE,{"derivedFrom":sQuery(id+"F11.wireOp",EDGE,"E561")}),1.0]])]});
            var Q40;
            Q40=makeQuery(id+"F11.imprint","IMPRINT",FACE,{"disambiguationData":[TD([[makeQuery(id+"F11.imprint","IMPRINT",EDGE,{"derivedFrom":sQuery(id+"F11.wireOp",EDGE,"E559")}),-1.0]])]});
            var Q41;
            Q41=makeQuery(id+"F11.imprint","IMPRINT",FACE,{"disambiguationData":[TD([[makeQuery(id+"F11.imprint","IMPRINT",EDGE,{"derivedFrom":sQuery(id+"F11.wireOp",EDGE,"E555")}),1.0]])]});
            var Q42;
            Q42=makeQuery(id+"F11.imprint","IMPRINT",FACE,{"disambiguationData":[TD([[makeQuery(id+"F11.imprint","IMPRINT",EDGE,{"derivedFrom":sQuery(id+"F11.wireOp",EDGE,"E591")}),-1.0]])]});
            var Q43;
            Q43=makeQuery(id+"F11.imprint","IMPRINT",FACE,{"disambiguationData":[TD([[makeQuery(id+"F11.imprint","IMPRINT",EDGE,{"derivedFrom":sQuery(id+"F11.wireOp",EDGE,"E593")}),1.0]])]});
            var Q44;
            Q44=makeQuery(id+"F11.imprint","IMPRINT",FACE,{"disambiguationData":[TD([[makeQuery(id+"F11.imprint","IMPRINT",EDGE,{"derivedFrom":sQuery(id+"F11.wireOp",EDGE,"E547")}),1.0]])]});
            var Q45;
            Q45=makeQuery(id+"F11.imprint","IMPRINT",FACE,{"disambiguationData":[TD([[makeQuery(id+"F11.imprint","IMPRINT",EDGE,{"derivedFrom":sQuery(id+"F11.wireOp",EDGE,"E595")}),-1.0]])]});
            var Q46;
            Q46=makeQuery(id+"F11.imprint","IMPRINT",FACE,{"disambiguationData":[TD([[makeQuery(id+"F11.imprint","IMPRINT",EDGE,{"derivedFrom":sQuery(id+"F11.wireOp",EDGE,"E601")}),1.0]])]});
            var Q47;
            Q47=makeQuery(id+"F11.imprint","IMPRINT",FACE,{"disambiguationData":[TD([[makeQuery(id+"F11.imprint","IMPRINT",EDGE,{"derivedFrom":sQuery(id+"F11.wireOp",EDGE,"E605")}),1.0]])]});
            var Q48;
            Q48=makeQuery(id+"F11.imprint","IMPRINT",FACE,{"disambiguationData":[TD([[makeQuery(id+"F11.imprint","IMPRINT",EDGE,{"derivedFrom":sQuery(id+"F11.wireOp",EDGE,"E633")}),-1.0]])]});
            var Q49;
            Q49=makeQuery(id+"F11.imprint","IMPRINT",FACE,{"disambiguationData":[TD([[makeQuery(id+"F11.imprint","IMPRINT",EDGE,{"derivedFrom":sQuery(id+"F11.wireOp",EDGE,"E600")}),1.0]])]});
            var Q50;
            Q50=makeQuery(id+"F11.imprint","IMPRINT",FACE,{"disambiguationData":[TD([[makeQuery(id+"F11.imprint","IMPRINT",EDGE,{"derivedFrom":sQuery(id+"F11.wireOp",EDGE,"E607")}),-1.0]])]});
            var Q51;
            {var subQ0=sQuery(id+"F11.wireOp",EDGE,"E630");Q51=makeQuery(id+"F11.imprint","IMPRINT",FACE,{"disambiguationData":[TD([[makeQuery(id+"F11.imprint","IMPRINT",EDGE,{"derivedFrom":subQ0}),-1.0]])]});}
            var Q52;
            Q52=makeQuery(id+"F11.imprint","IMPRINT",FACE,{"disambiguationData":[TD([[makeQuery(id+"F11.imprint","IMPRINT",EDGE,{"derivedFrom":sQuery(id+"F11.wireOp",EDGE,"E625")}),1.0]])]});
            var Q53;
            Q53=makeQuery(id+"F11.imprint","IMPRINT",FACE,{"disambiguationData":[TD([[makeQuery(id+"F11.imprint","IMPRINT",EDGE,{"derivedFrom":sQuery(id+"F11.wireOp",EDGE,"E631")}),1.0]])]});
            var Q54;
            Q54=makeQuery(id+"F11.imprint","IMPRINT",FACE,{"disambiguationData":[TD([[makeQuery(id+"F11.imprint","IMPRINT",EDGE,{"derivedFrom":sQuery(id+"F11.wireOp",EDGE,"E621")}),1.0]])]});
            var Q55;
            Q55=makeQuery(id+"F11.imprint","IMPRINT",FACE,{"disambiguationData":[TD([[makeQuery(id+"F11.imprint","IMPRINT",EDGE,{"derivedFrom":sQuery(id+"F11.wireOp",EDGE,"E641")}),-1.0]])]});
            var Q56;
            Q56=makeQuery(id+"F11.imprint","IMPRINT",FACE,{"disambiguationData":[TD([[makeQuery(id+"F11.imprint","IMPRINT",EDGE,{"derivedFrom":sQuery(id+"F11.wireOp",EDGE,"E624")}),1.0]])]});
            var Q57;
            {var subQ0=sQuery(id+"F12.wireOp",EDGE,"E878");Q57=makeQuery(id+"F12.imprint","IMPRINT",FACE,{"disambiguationData":[TD([[makeQuery(id+"F12.imprint","IMPRINT",EDGE,{"derivedFrom":subQ0}),1.0]])]});}
            var Q58;
            Q58=makeQuery(id+"F12.imprint","IMPRINT",FACE,{"disambiguationData":[TD([[makeQuery(id+"F12.imprint","IMPRINT",EDGE,{"derivedFrom":sQuery(id+"F12.wireOp",EDGE,"E873")}),-1.0]])]});
            var Q59;
            Q59=makeQuery(id+"F12.imprint","IMPRINT",FACE,{"disambiguationData":[TD([[makeQuery(id+"F12.imprint","IMPRINT",EDGE,{"derivedFrom":sQuery(id+"F12.wireOp",EDGE,"E853")}),1.0]])]});
            var Q60;
            Q60=makeQuery(id+"F12.imprint","IMPRINT",FACE,{"disambiguationData":[TD([[makeQuery(id+"F12.imprint","IMPRINT",EDGE,{"derivedFrom":sQuery(id+"F12.wireOp",EDGE,"E863")}),1.0]])]});
            var Q61;
            {var subQ1=sQuery(id+"F12.wireOp",EDGE,"E857");Q61=makeQuery(id+"F12.imprint","IMPRINT",FACE,{"disambiguationData":[TD([[makeQuery(id+"F12.imprint","IMPRINT",EDGE,{"derivedFrom":subQ1}),1.0]])]});}
            var Q62;
            {var subQ0=sQuery(id+"F12.wireOp",EDGE,"E842");var subQ1=sQuery(id+"F12.wireOp",EDGE,"E839");var subQ2=makeQuery(id+"F12.imprint","INTERSECT",VERTEX,{"derivedFrom":[subQ1,subQ0]});Q62=makeQuery(id+"F12.imprint","IMPRINT",FACE,{"disambiguationData":[TD([[makeQuery(id+"F12.imprint","IMPRINT",EDGE,{"disambiguationData":[TD([[subQ2,-1.0]])],"derivedFrom":subQ1}),-1.0]])]});}
            var Q63;
            Q63=makeQuery(id+"F12.imprint","IMPRINT",FACE,{"disambiguationData":[TD([[makeQuery(id+"F12.imprint","IMPRINT",EDGE,{"derivedFrom":sQuery(id+"F12.wireOp",EDGE,"E837")}),1.0]])]});
            var Q64;
            Q64=makeQuery(id+"F12.imprint","IMPRINT",FACE,{"disambiguationData":[TD([[makeQuery(id+"F12.imprint","IMPRINT",EDGE,{"derivedFrom":sQuery(id+"F12.wireOp",EDGE,"E865")}),-1.0]])]});
            var Q65;
            {var subQ0=sQuery(id+"F12.wireOp",EDGE,"E849");Q65=makeQuery(id+"F12.imprint","IMPRINT",FACE,{"disambiguationData":[TD([[makeQuery(id+"F12.imprint","IMPRINT",EDGE,{"derivedFrom":subQ0}),-1.0]])]});}
            var Q66;
            Q66=makeQuery(id+"F12.imprint","IMPRINT",FACE,{"disambiguationData":[TD([[makeQuery(id+"F12.imprint","IMPRINT",EDGE,{"derivedFrom":sQuery(id+"F12.wireOp",EDGE,"E833")}),1.0]])]});
            var Q67;
            {var subQ0=sQuery(id+"F12.wireOp",EDGE,"E778");Q67=makeQuery(id+"F12.imprint","IMPRINT",FACE,{"disambiguationData":[TD([[makeQuery(id+"F12.imprint","IMPRINT",EDGE,{"derivedFrom":subQ0}),-1.0]])]});}
            var Q68;
            {var subQ0=sQuery(id+"F12.wireOp",EDGE,"E783");var subQ1=sQuery(id+"F12.wireOp",EDGE,"E777");var subQ2=makeQuery(id+"F12.imprint","INTERSECT",VERTEX,{"derivedFrom":[subQ1,subQ0]});Q68=makeQuery(id+"F12.imprint","IMPRINT",FACE,{"disambiguationData":[TD([[makeQuery(id+"F12.imprint","IMPRINT",EDGE,{"disambiguationData":[TD([[subQ2,-1.0]])],"derivedFrom":subQ1}),-1.0]])]});}
            var Q69;
            Q69=makeQuery(id+"F12.imprint","IMPRINT",FACE,{"disambiguationData":[TD([[makeQuery(id+"F12.imprint","IMPRINT",EDGE,{"derivedFrom":sQuery(id+"F12.wireOp",EDGE,"E827")}),-1.0]])]});
            var Q70;
            {var subQ0=sQuery(id+"F12.wireOp",EDGE,"E821");Q70=makeQuery(id+"F12.imprint","IMPRINT",FACE,{"disambiguationData":[TD([[makeQuery(id+"F12.imprint","IMPRINT",EDGE,{"derivedFrom":subQ0}),1.0]])]});}
            var Q71;
            {var subQ0=sQuery(id+"F12.wireOp",EDGE,"E822");var subQ1=sQuery(id+"F12.wireOp",EDGE,"E786");var subQ2=makeQuery(id+"F12.imprint","INTERSECT",VERTEX,{"derivedFrom":[subQ1,subQ0]});Q71=makeQuery(id+"F12.imprint","IMPRINT",FACE,{"disambiguationData":[TD([[makeQuery(id+"F12.imprint","IMPRINT",EDGE,{"disambiguationData":[TD([[subQ2,-1.0]])],"derivedFrom":subQ1}),1.0]])]});}
            var Q72;
            {var subQ0=sQuery(id+"F12.wireOp",EDGE,"E769");Q72=makeQuery(id+"F12.imprint","IMPRINT",FACE,{"disambiguationData":[TD([[makeQuery(id+"F12.imprint","IMPRINT",EDGE,{"derivedFrom":subQ0}),-1.0]])]});}
            var Q73;
            {var subQ0=sQuery(id+"F12.wireOp",EDGE,"E746");Q73=makeQuery(id+"F12.imprint","IMPRINT",FACE,{"disambiguationData":[TD([[makeQuery(id+"F12.imprint","IMPRINT",EDGE,{"derivedFrom":subQ0}),-1.0]])]});}
            var Q74;
            Q74=makeQuery(id+"F12.imprint","IMPRINT",FACE,{"disambiguationData":[TD([[makeQuery(id+"F12.imprint","IMPRINT",EDGE,{"derivedFrom":sQuery(id+"F12.wireOp",EDGE,"E740")}),1.0]])]});
            var Q75;
            {var subQ0=sQuery(id+"F12.wireOp",EDGE,"E685");Q75=makeQuery(id+"F12.imprint","IMPRINT",FACE,{"disambiguationData":[TD([[makeQuery(id+"F12.imprint","IMPRINT",EDGE,{"derivedFrom":subQ0}),-1.0]])]});}
            var Q76;
            {var subQ0=sQuery(id+"F12.wireOp",EDGE,"E728");Q76=makeQuery(id+"F12.imprint","IMPRINT",FACE,{"disambiguationData":[TD([[makeQuery(id+"F12.imprint","IMPRINT",EDGE,{"derivedFrom":subQ0}),1.0]])]});}
            var Q77;
            Q77=makeQuery(id+"F12.imprint","IMPRINT",FACE,{"disambiguationData":[TD([[makeQuery(id+"F12.imprint","IMPRINT",EDGE,{"derivedFrom":sQuery(id+"F12.wireOp",EDGE,"E734")}),-1.0]])]});
            var Q78;
            Q78=makeQuery(id+"F12.imprint","IMPRINT",FACE,{"disambiguationData":[TD([[makeQuery(id+"F12.imprint","IMPRINT",EDGE,{"derivedFrom":sQuery(id+"F12.wireOp",EDGE,"E702")}),-1.0]])]});
            var Q79;
            Q79=makeQuery(id+"F12.imprint","IMPRINT",FACE,{"disambiguationData":[TD([[makeQuery(id+"F12.imprint","IMPRINT",EDGE,{"derivedFrom":sQuery(id+"F12.wireOp",EDGE,"E713")}),-1.0]])]});
            var Q80;
            Q80=makeQuery(id+"F12.imprint","IMPRINT",FACE,{"disambiguationData":[TD([[makeQuery(id+"F12.imprint","IMPRINT",EDGE,{"derivedFrom":sQuery(id+"F12.wireOp",EDGE,"E678")}),-1.0]])]});
            var Q81;
            {var subQ0=sQuery(id+"F12.wireOp",EDGE,"E671");Q81=makeQuery(id+"F12.imprint","IMPRINT",FACE,{"disambiguationData":[TD([[makeQuery(id+"F12.imprint","IMPRINT",EDGE,{"derivedFrom":subQ0}),-1.0]])]});}
            var Q82;
            Q82=makeQuery(id+"F12.imprint","IMPRINT",FACE,{"disambiguationData":[TD([[makeQuery(id+"F12.imprint","IMPRINT",EDGE,{"derivedFrom":sQuery(id+"F12.wireOp",EDGE,"E657")}),-1.0]])]});
            var Q83;
            Q83=makeQuery(id+"F12.imprint","IMPRINT",FACE,{"disambiguationData":[TD([[makeQuery(id+"F12.imprint","IMPRINT",EDGE,{"derivedFrom":sQuery(id+"F12.wireOp",EDGE,"E659")}),1.0]])]});
            var Q84;
            Q84=makeQuery(id+"F12.imprint","IMPRINT",FACE,{"disambiguationData":[TD([[makeQuery(id+"F12.imprint","IMPRINT",EDGE,{"derivedFrom":sQuery(id+"F12.wireOp",EDGE,"E880")}),-1.0]])]});
            var Q85;
            Q85=makeQuery(id+"F12.imprint","IMPRINT",FACE,{"disambiguationData":[TD([[makeQuery(id+"F12.imprint","IMPRINT",EDGE,{"derivedFrom":sQuery(id+"F12.wireOp",EDGE,"E661")}),-1.0]])]});
            var Q86;
            {var subQ0=sQuery(id+"F12.wireOp",EDGE,"E668");var subQ1=sQuery(id+"F12.wireOp",EDGE,"E666");var subQ2=makeQuery(id+"F12.imprint","INTERSECT",VERTEX,{"derivedFrom":[subQ1,subQ0]});Q86=makeQuery(id+"F12.imprint","IMPRINT",FACE,{"disambiguationData":[TD([[makeQuery(id+"F12.imprint","IMPRINT",EDGE,{"disambiguationData":[TD([[subQ2,-1.0]])],"derivedFrom":subQ1}),-1.0]])]});}
            var Q87;
            {var subQ4=sQuery(id+"F12.wireOp",EDGE,"E674");Q87=makeQuery(id+"F12.imprint","IMPRINT",FACE,{"disambiguationData":[TD([[makeQuery(id+"F12.imprint","IMPRINT",EDGE,{"derivedFrom":subQ4}),1.0]])]});}
            var Q88;
            {var subQ0=sQuery(id+"F12.wireOp",EDGE,"E719");var subQ1=sQuery(id+"F12.wireOp",EDGE,"E715");var subQ2=makeQuery(id+"F12.imprint","INTERSECT",VERTEX,{"derivedFrom":[subQ1,subQ0]});Q88=makeQuery(id+"F12.imprint","IMPRINT",FACE,{"disambiguationData":[TD([[makeQuery(id+"F12.imprint","IMPRINT",EDGE,{"disambiguationData":[TD([[subQ2,-1.0]])],"derivedFrom":subQ1}),-1.0]])]});}
            var Q89;
            Q89=makeQuery(id+"F12.imprint","IMPRINT",FACE,{"disambiguationData":[TD([[makeQuery(id+"F12.imprint","IMPRINT",EDGE,{"derivedFrom":sQuery(id+"F12.wireOp",EDGE,"E700")}),1.0]])]});
            var Q90;
            Q90=makeQuery(id+"F12.imprint","IMPRINT",FACE,{"disambiguationData":[TD([[makeQuery(id+"F12.imprint","IMPRINT",EDGE,{"derivedFrom":sQuery(id+"F12.wireOp",EDGE,"E710")}),-1.0]])]});
            var Q91;
            Q91=makeQuery(id+"F12.imprint","IMPRINT",FACE,{"disambiguationData":[TD([[makeQuery(id+"F12.imprint","IMPRINT",EDGE,{"derivedFrom":sQuery(id+"F12.wireOp",EDGE,"E686")}),1.0]])]});
            var Q92;
            {var subQ5=sQuery(id+"F12.wireOp",EDGE,"E694");Q92=makeQuery(id+"F12.imprint","IMPRINT",FACE,{"disambiguationData":[TD([[makeQuery(id+"F12.imprint","IMPRINT",EDGE,{"derivedFrom":subQ5}),1.0]])]});}
            var Q93;
            {var subQ0=sQuery(id+"F12.wireOp",EDGE,"E692");var subQ1=sQuery(id+"F12.wireOp",EDGE,"E688");var subQ2=makeQuery(id+"F12.imprint","INTERSECT",VERTEX,{"derivedFrom":[subQ1,subQ0]});Q93=makeQuery(id+"F12.imprint","IMPRINT",FACE,{"disambiguationData":[TD([[makeQuery(id+"F12.imprint","IMPRINT",EDGE,{"disambiguationData":[TD([[subQ2,-1.0]])],"derivedFrom":subQ1}),-1.0]])]});}
            var Q94;
            {var subQ0=sQuery(id+"F12.wireOp",EDGE,"E753");var subQ1=sQuery(id+"F12.wireOp",EDGE,"E749");var subQ2=makeQuery(id+"F12.imprint","INTERSECT",VERTEX,{"derivedFrom":[subQ1,subQ0]});Q94=makeQuery(id+"F12.imprint","IMPRINT",FACE,{"disambiguationData":[TD([[makeQuery(id+"F12.imprint","IMPRINT",EDGE,{"disambiguationData":[TD([[subQ2,-1.0]])],"derivedFrom":subQ1}),-1.0]])]});}
            var Q95;
            Q95=makeQuery(id+"F12.imprint","IMPRINT",FACE,{"disambiguationData":[TD([[makeQuery(id+"F12.imprint","IMPRINT",EDGE,{"derivedFrom":sQuery(id+"F12.wireOp",EDGE,"E757")}),-1.0]])]});
            var Q96;
            Q96=makeQuery(id+"F12.imprint","IMPRINT",FACE,{"disambiguationData":[TD([[makeQuery(id+"F12.imprint","IMPRINT",EDGE,{"derivedFrom":sQuery(id+"F12.wireOp",EDGE,"E732")}),1.0]])]});
            var Q97;
            Q97=makeQuery(id+"F12.imprint","IMPRINT",FACE,{"disambiguationData":[TD([[makeQuery(id+"F12.imprint","IMPRINT",EDGE,{"derivedFrom":sQuery(id+"F12.wireOp",EDGE,"E747")}),1.0]])]});
            var Q98;
            Q98=makeQuery(id+"F12.imprint","IMPRINT",FACE,{"disambiguationData":[TD([[makeQuery(id+"F12.imprint","IMPRINT",EDGE,{"derivedFrom":sQuery(id+"F12.wireOp",EDGE,"E762")}),-1.0]])]});
            var Q99;
            Q99=makeQuery(id+"F12.imprint","IMPRINT",FACE,{"disambiguationData":[TD([[makeQuery(id+"F12.imprint","IMPRINT",EDGE,{"derivedFrom":sQuery(id+"F12.wireOp",EDGE,"E806")}),-1.0]])]});
            var Q100;
            {var subQ4=sQuery(id+"F12.wireOp",EDGE,"E765");Q100=makeQuery(id+"F12.imprint","IMPRINT",FACE,{"disambiguationData":[TD([[makeQuery(id+"F12.imprint","IMPRINT",EDGE,{"derivedFrom":subQ4}),1.0]])]});}
            var Q101;
            {var subQ0=sQuery(id+"F12.wireOp",EDGE,"E812");var subQ1=sQuery(id+"F12.wireOp",EDGE,"E808");var subQ2=makeQuery(id+"F12.imprint","INTERSECT",VERTEX,{"derivedFrom":[subQ1,subQ0]});Q101=makeQuery(id+"F12.imprint","IMPRINT",FACE,{"disambiguationData":[TD([[makeQuery(id+"F12.imprint","IMPRINT",EDGE,{"disambiguationData":[TD([[subQ2,-1.0]])],"derivedFrom":subQ1}),-1.0]])]});}
            var Q102;
            {var subQ5=sQuery(id+"F12.wireOp",EDGE,"E787");Q102=makeQuery(id+"F12.imprint","IMPRINT",FACE,{"disambiguationData":[TD([[makeQuery(id+"F12.imprint","IMPRINT",EDGE,{"derivedFrom":subQ5}),1.0]])]});}
            var Q103;
            Q103=makeQuery(id+"F12.imprint","IMPRINT",FACE,{"disambiguationData":[TD([[makeQuery(id+"F12.imprint","IMPRINT",EDGE,{"derivedFrom":sQuery(id+"F12.wireOp",EDGE,"E793")}),1.0]])]});
            var Q104;
            Q104=makeQuery(id+"F12.imprint","IMPRINT",FACE,{"disambiguationData":[TD([[makeQuery(id+"F12.imprint","IMPRINT",EDGE,{"derivedFrom":sQuery(id+"F12.wireOp",EDGE,"E795")}),-1.0]])]});
            var Q105;
            Q105=makeQuery(id+"F12.imprint","IMPRINT",FACE,{"disambiguationData":[TD([[makeQuery(id+"F12.imprint","IMPRINT",EDGE,{"derivedFrom":sQuery(id+"F12.wireOp",EDGE,"E803")}),-1.0]])]});
            var Q106;
            Q106=makeQuery(id+"F12.imprint","IMPRINT",FACE,{"disambiguationData":[TD([[makeQuery(id+"F12.imprint","IMPRINT",EDGE,{"derivedFrom":sQuery(id+"F12.wireOp",EDGE,"E779")}),1.0]])]});
            var Q107;
            Q107=makeQuery(id+"F12.imprint","IMPRINT",FACE,{"disambiguationData":[TD([[makeQuery(id+"F12.imprint","IMPRINT",EDGE,{"derivedFrom":sQuery(id+"F12.wireOp",EDGE,"E825")}),1.0]])]});
            var Q108;
            {var subQ0=sQuery(id+"F12.wireOp",EDGE,"E785");var subQ1=sQuery(id+"F12.wireOp",EDGE,"E781");var subQ2=makeQuery(id+"F12.imprint","INTERSECT",VERTEX,{"derivedFrom":[subQ1,subQ0]});Q108=makeQuery(id+"F12.imprint","IMPRINT",FACE,{"disambiguationData":[TD([[makeQuery(id+"F12.imprint","IMPRINT",EDGE,{"disambiguationData":[TD([[subQ2,-1.0]])],"derivedFrom":subQ1}),-1.0]])]});}
            var Q109;
            Q109=makeQuery(id+"F11.imprint","IMPRINT",FACE,{"disambiguationData":[TD([[makeQuery(id+"F11.imprint","IMPRINT",EDGE,{"derivedFrom":sQuery(id+"F11.wireOp",EDGE,"E437")}),-1.0]])]});
            var Q110;
            Q110=makeQuery(id+"F11.imprint","IMPRINT",FACE,{"disambiguationData":[TD([[makeQuery(id+"F11.imprint","IMPRINT",EDGE,{"derivedFrom":sQuery(id+"F11.wireOp",EDGE,"E549")}),-1.0]])]});
            var Q111;
            Q111=makeQuery(id+"F11.imprint","IMPRINT",FACE,{"disambiguationData":[TD([[makeQuery(id+"F11.imprint","IMPRINT",EDGE,{"derivedFrom":sQuery(id+"F11.wireOp",EDGE,"E614")}),-1.0]])]});
            var Q112;
            {var subQ0=sQuery(id+"F12.wireOp",EDGE,"E846");Q112=makeQuery(id+"F12.imprint","IMPRINT",FACE,{"disambiguationData":[TD([[makeQuery(id+"F12.imprint","IMPRINT",EDGE,{"derivedFrom":subQ0}),-1.0]])]});}
            extrude(context, id + "F13", {"entities" : qUnion([Q0, Q1, Q2, Q3, Q4, Q5, Q6, Q7, Q8, Q9, Q10, Q11, Q12, Q13, Q14, Q15, Q16, Q17, Q18, Q19, Q20, Q21, Q22, Q23, Q24, Q25, Q26, Q27, Q28, Q29, Q30, Q31, Q32, Q33, Q34, Q35, Q36, Q37, Q38, Q39, Q40, Q41, Q42, Q43, Q44, Q45, Q46, Q47, Q48, Q49, Q50, Q51, Q52, Q53, Q54, Q55, Q56, Q57, Q58, Q59, Q60, Q61, Q62, Q63, Q64, Q65, Q66, Q67, Q68, Q69, Q70, Q71, Q72, Q73, Q74, Q75, Q76, Q77, Q78, Q79, Q80, Q81, Q82, Q83, Q84, Q85, Q86, Q87, Q88, Q89, Q90, Q91, Q92, Q93, Q94, Q95, Q96, Q97, Q98, Q99, Q100, Q101, Q102, Q103, Q104, Q105, Q106, Q107, Q108, Q109, Q110, Q111, Q112]), "operationType" : NewBodyOperationType.REMOVE, "oppositeDirection" : true, "depth" : 25.4 * mm});
        }
    });
